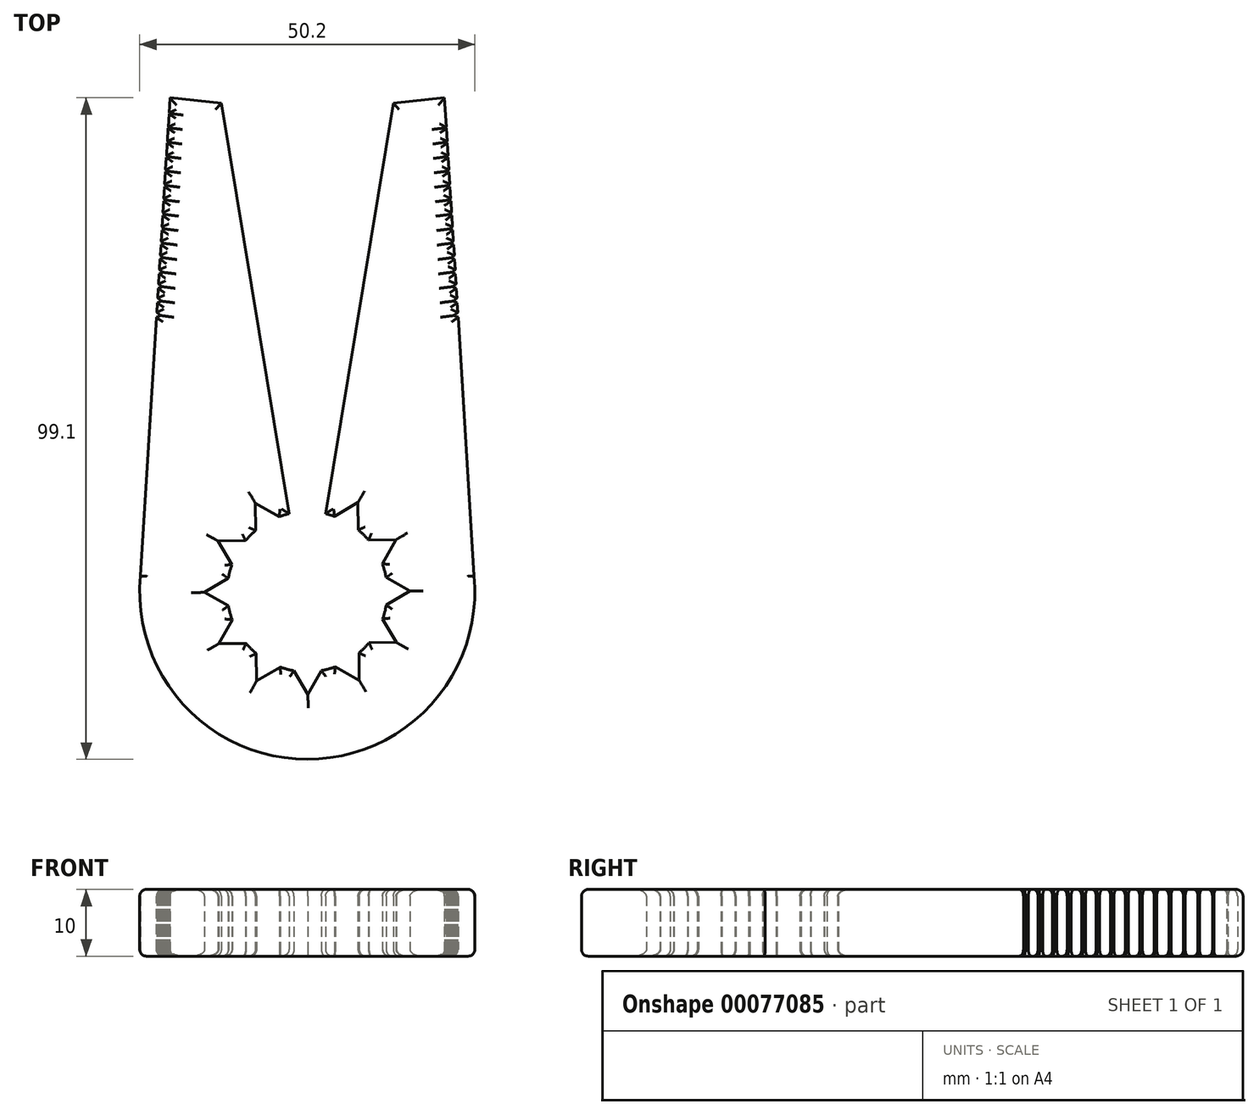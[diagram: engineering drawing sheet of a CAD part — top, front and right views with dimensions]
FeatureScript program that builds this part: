
annotation { "Feature Type Name" : "Feature", "Feature Type Description" : "" }
export const myFeature = defineFeature(function(context is Context, id is Id, definition is map)
    precondition{}
    {
        {
            var Q0;
            Q0=qCreatedBy(makeId("Top.planeOp"),FACE);
            var sketch = newSketch(context, id + "F0", { "sketchPlane" : qUnion([Q0])});
            skLineSegment(sketch, "E0", {"start": v(-12.9, 73.17) * mm, "end": v(-20.56, 74) * mm});
            skLineSegment(sketch, "E1", {"start": v(-20.56, 74) * mm, "end": v(-21.27, 62.5) * mm});
            skLineSegment(sketch, "E2", {"start": v(0, 72.49) * mm, "end": v(0, 12) * mm, "construction": true});
            skArc(sketch, "E3.trimOffspring", {"start": v(-25, 2.38) * mm, "mid": v(-18.57, -16.89) * mm, "end": v(0, -25.1) * mm});
            skArc(sketch, "E4.MirrorCS", {"start": v(25, 2.38) * mm, "mid": v(18.57, -16.89) * mm, "end": v(0, -25.1) * mm});
            skLineSegment(sketch, "E5.MirrorCS", {"start": v(20.56, 74) * mm, "end": v(21.27, 62.5) * mm});
            skLineSegment(sketch, "E6.MirrorCS", {"start": v(12.9, 73.17) * mm, "end": v(20.56, 74) * mm});
            skLineSegment(sketch, "E7.MirrorCS", {"start": v(2.74, 11.68) * mm, "end": v(12.9, 73.17) * mm});
            skLineSegment(sketch, "E8.trimOffspring", {"start": v(-22.3, 45.9) * mm, "end": v(-25, 2.38) * mm});
            skLineSegment(sketch, "E9.trimOffspring", {"start": v(22.3, 45.9) * mm, "end": v(25, 2.38) * mm});
            skLineSegment(sketch, "E10", {"start": v(-2.74, 11.68) * mm, "end": v(-12.9, 73.17) * mm});
            skPoint(sketch, "E11.orphan", {"position": v(3.63, 13.56) * mm});
            skLineSegment(sketch, "E12.trimOffspring", {"start": v(0, 10.98) * mm, "end": v(0, -73.22) * mm, "construction": true});
            skArc(sketch, "E13", {"start": v(-7.74, 9.17) * mm, "mid": v(-8.53, 8.44) * mm, "end": v(-9.25, 7.64) * mm});
            skLineSegment(sketch, "E14.0", {"start": v(-15.38, -0.1) * mm, "end": v(-11.83, 2) * mm});
            skLineSegment(sketch, "E14.2", {"start": v(-11.81, -2.12) * mm, "end": v(-15.38, -0.1) * mm});
            skPoint(sketch, "E14.0.midPoint", {"position": v(-10.66, 2.69) * mm});
            skPoint(sketch, "E14.1.start.orphan", {"position": v(-5.94, 5.48) * mm});
            skPoint(sketch, "E15.1.0", {"position": v(-10.58, -3) * mm});
            skLineSegment(sketch, "E15.1.1", {"start": v(-13.27, -7.78) * mm, "end": v(-11.25, -4.19) * mm});
            skLineSegment(sketch, "E15.1.2", {"start": v(-9.17, -7.74) * mm, "end": v(-13.27, -7.78) * mm});
            skPoint(sketch, "E15.2.0", {"position": v(-7.66, -7.89) * mm});
            skLineSegment(sketch, "E15.2.1", {"start": v(-7.6, -13.37) * mm, "end": v(-7.64, -9.25) * mm});
            skLineSegment(sketch, "E15.2.2", {"start": v(-4.07, -11.29) * mm, "end": v(-7.6, -13.37) * mm});
            skPoint(sketch, "E15.3.0", {"position": v(-2.69, -10.66) * mm});
            skLineSegment(sketch, "E15.3.1", {"start": v(0.1, -15.38) * mm, "end": v(-2, -11.83) * mm});
            skLineSegment(sketch, "E15.3.2", {"start": v(2.12, -11.81) * mm, "end": v(0.1, -15.38) * mm});
            skPoint(sketch, "E15.4.0", {"position": v(3, -10.58) * mm});
            skLineSegment(sketch, "E15.4.1", {"start": v(7.78, -13.27) * mm, "end": v(4.19, -11.25) * mm});
            skLineSegment(sketch, "E15.4.2", {"start": v(7.74, -9.17) * mm, "end": v(7.78, -13.27) * mm});
            skPoint(sketch, "E15.5.0", {"position": v(7.89, -7.66) * mm});
            skLineSegment(sketch, "E15.5.1", {"start": v(13.37, -7.6) * mm, "end": v(9.25, -7.64) * mm});
            skLineSegment(sketch, "E15.5.2", {"start": v(11.29, -4.07) * mm, "end": v(13.37, -7.6) * mm});
            skPoint(sketch, "E15.6.0", {"position": v(10.66, -2.69) * mm});
            skLineSegment(sketch, "E15.6.1", {"start": v(15.38, 0.1) * mm, "end": v(11.83, -2) * mm});
            skLineSegment(sketch, "E15.6.2", {"start": v(11.81, 2.12) * mm, "end": v(15.38, 0.1) * mm});
            skPoint(sketch, "E15.7.0", {"position": v(10.58, 3) * mm});
            skLineSegment(sketch, "E15.7.1", {"start": v(13.27, 7.78) * mm, "end": v(11.25, 4.19) * mm});
            skLineSegment(sketch, "E15.7.2", {"start": v(9.17, 7.74) * mm, "end": v(13.27, 7.78) * mm});
            skPoint(sketch, "E15.8.0", {"position": v(7.66, 7.89) * mm});
            skLineSegment(sketch, "E15.8.1", {"start": v(7.6, 13.37) * mm, "end": v(7.64, 9.25) * mm});
            skLineSegment(sketch, "E15.8.2", {"start": v(4.07, 11.29) * mm, "end": v(7.6, 13.37) * mm});
            skPoint(sketch, "E15.9.0", {"position": v(2.69, 10.66) * mm});
            skLineSegment(sketch, "E15.9.1", {"start": v(-0.1, 15.38) * mm, "end": v(0, 15.2) * mm});
            skPoint(sketch, "E15.10.0", {"position": v(-3, 10.58) * mm});
            skLineSegment(sketch, "E15.10.1", {"start": v(-7.78, 13.27) * mm, "end": v(-4.19, 11.25) * mm});
            skLineSegment(sketch, "E15.10.2", {"start": v(-7.74, 9.17) * mm, "end": v(-7.78, 13.27) * mm});
            skPoint(sketch, "E15.11.0", {"position": v(-7.89, 7.66) * mm});
            skLineSegment(sketch, "E15.11.1", {"start": v(-13.37, 7.6) * mm, "end": v(-9.25, 7.64) * mm});
            skLineSegment(sketch, "E15.11.2", {"start": v(-11.29, 4.07) * mm, "end": v(-13.37, 7.6) * mm});
            skArc(sketch, "E16.trimOffspring", {"start": v(-11.29, 4.07) * mm, "mid": v(-11.6, 3.05) * mm, "end": v(-11.83, 2) * mm});
            skArc(sketch, "E17.trimOffspring", {"start": v(-11.81, -2.12) * mm, "mid": v(-11.58, -3.16) * mm, "end": v(-11.25, -4.19) * mm});
            skArc(sketch, "E18.trimOffspring", {"start": v(-9.17, -7.74) * mm, "mid": v(-8.44, -8.53) * mm, "end": v(-7.64, -9.25) * mm});
            skArc(sketch, "E19.trimOffspring", {"start": v(-4.07, -11.29) * mm, "mid": v(-3.05, -11.6) * mm, "end": v(-2, -11.83) * mm});
            skArc(sketch, "E20.trimOffspring", {"start": v(2.12, -11.81) * mm, "mid": v(3.16, -11.58) * mm, "end": v(4.19, -11.25) * mm});
            skArc(sketch, "E21.trimOffspring", {"start": v(7.74, -9.17) * mm, "mid": v(8.53, -8.44) * mm, "end": v(9.25, -7.64) * mm});
            skArc(sketch, "E22.trimOffspring", {"start": v(11.29, -4.07) * mm, "mid": v(11.6, -3.05) * mm, "end": v(11.83, -2) * mm});
            skArc(sketch, "E23.trimOffspring", {"start": v(11.81, 2.12) * mm, "mid": v(11.58, 3.16) * mm, "end": v(11.25, 4.19) * mm});
            skArc(sketch, "E24.trimOffspring", {"start": v(9.17, 7.74) * mm, "mid": v(8.44, 8.53) * mm, "end": v(7.64, 9.25) * mm});
            skArc(sketch, "E25.trimOffspring", {"start": v(4.07, 11.29) * mm, "mid": v(3.41, 11.5) * mm, "end": v(2.74, 11.68) * mm});
            skArc(sketch, "E26.trimOffspring", {"start": v(-2.74, 11.68) * mm, "mid": v(-3.47, 11.49) * mm, "end": v(-4.19, 11.25) * mm});
            skPoint(sketch, "E27.orphan", {"position": v(2, 11.83) * mm});
            skLineSegment(sketch, "E28", {"start": v(-21.27, 62.5) * mm, "end": v(-22.3, 45.9) * mm});
            skLineSegment(sketch, "E29", {"start": v(21.27, 62.5) * mm, "end": v(22.3, 45.9) * mm});
            skSolve(sketch);
        }
        {
            var Q0;
            Q0=makeQuery(id+"F0.imprint","IMPRINT",FACE,{"disambiguationData":[TD([[makeQuery(id+"F0.imprint","IMPRINT",EDGE,{"derivedFrom":sQuery(id+"F0.wireOp",EDGE,"E0")}),1.0]])]});
            extrude(context, id + "F1", {"entities" : qUnion([Q0]), "depth" : 10 * mm});
        }
        {
            var Q0;
            Q0=qCreatedBy(makeId("Top.planeOp"),FACE);
            var sketch = newSketch(context, id + "F2", { "sketchPlane" : qUnion([Q0])});
            skCircle(sketch, "E30.cCircle", {"center": v(-30.95, 42.52) * mm, "radius": 4.54 * mm, "construction": true});
            skLineSegment(sketch, "E30.0", {"start": v(-21.95, 41.38) * mm, "end": v(-36.45, 35.3) * mm});
            skLineSegment(sketch, "E30.1", {"start": v(-36.45, 35.3) * mm, "end": v(-34.46, 50.9) * mm});
            skLineSegment(sketch, "E30.2", {"start": v(-34.46, 50.9) * mm, "end": v(-21.95, 41.38) * mm});
            skPoint(sketch, "E30.0.midPoint", {"position": v(-29.2, 38.34) * mm});
            skLineSegment(sketch, "E31.1.0.0", {"start": v(-21.85, 43.54) * mm, "end": v(-36.35, 37.46) * mm});
            skCircle(sketch, "E31.1.0.1", {"center": v(-30.86, 44.69) * mm, "radius": 4.54 * mm, "construction": true});
            skPoint(sketch, "E31.1.0.2", {"position": v(-29.1, 40.5) * mm});
            skLineSegment(sketch, "E31.1.0.3", {"start": v(-34.37, 53.06) * mm, "end": v(-21.85, 43.54) * mm});
            skLineSegment(sketch, "E31.1.0.4", {"start": v(-36.35, 37.46) * mm, "end": v(-34.37, 53.06) * mm});
            skLineSegment(sketch, "E31.2.0.0", {"start": v(-21.75, 45.7) * mm, "end": v(-36.25, 39.62) * mm});
            skCircle(sketch, "E31.2.0.1", {"center": v(-30.76, 46.85) * mm, "radius": 4.54 * mm, "construction": true});
            skPoint(sketch, "E31.2.0.2", {"position": v(-29, 42.66) * mm});
            skLineSegment(sketch, "E31.2.0.3", {"start": v(-34.27, 55.22) * mm, "end": v(-21.75, 45.7) * mm});
            skLineSegment(sketch, "E31.2.0.4", {"start": v(-36.25, 39.62) * mm, "end": v(-34.27, 55.22) * mm});
            skLineSegment(sketch, "E31.3.0.0", {"start": v(-21.65, 47.87) * mm, "end": v(-36.16, 41.79) * mm});
            skCircle(sketch, "E31.3.0.1", {"center": v(-30.66, 49.01) * mm, "radius": 4.54 * mm, "construction": true});
            skPoint(sketch, "E31.3.0.2", {"position": v(-28.9, 44.83) * mm});
            skLineSegment(sketch, "E31.3.0.3", {"start": v(-34.17, 57.39) * mm, "end": v(-21.65, 47.87) * mm});
            skLineSegment(sketch, "E31.3.0.4", {"start": v(-36.16, 41.79) * mm, "end": v(-34.17, 57.39) * mm});
            skLineSegment(sketch, "E31.4.0.0", {"start": v(-21.55, 50.03) * mm, "end": v(-36.06, 43.95) * mm});
            skCircle(sketch, "E31.4.0.1", {"center": v(-30.56, 51.18) * mm, "radius": 4.54 * mm, "construction": true});
            skPoint(sketch, "E31.4.0.2", {"position": v(-28.8, 46.99) * mm});
            skLineSegment(sketch, "E31.4.0.3", {"start": v(-34.07, 59.55) * mm, "end": v(-21.55, 50.03) * mm});
            skLineSegment(sketch, "E31.4.0.4", {"start": v(-36.06, 43.95) * mm, "end": v(-34.07, 59.55) * mm});
            skLineSegment(sketch, "E31.5.0.0", {"start": v(-21.46, 52.2) * mm, "end": v(-35.96, 46.11) * mm});
            skCircle(sketch, "E31.5.0.1", {"center": v(-30.46, 53.34) * mm, "radius": 4.54 * mm, "construction": true});
            skPoint(sketch, "E31.5.0.2", {"position": v(-28.7, 49.15) * mm});
            skLineSegment(sketch, "E31.5.0.3", {"start": v(-33.98, 61.71) * mm, "end": v(-21.46, 52.2) * mm});
            skLineSegment(sketch, "E31.5.0.4", {"start": v(-35.96, 46.11) * mm, "end": v(-33.98, 61.71) * mm});
            skLineSegment(sketch, "E31.6.0.0", {"start": v(-21.36, 54.36) * mm, "end": v(-35.86, 48.27) * mm});
            skCircle(sketch, "E31.6.0.1", {"center": v(-30.37, 55.5) * mm, "radius": 4.54 * mm, "construction": true});
            skPoint(sketch, "E31.6.0.2", {"position": v(-28.61, 51.32) * mm});
            skLineSegment(sketch, "E31.6.0.3", {"start": v(-33.88, 63.88) * mm, "end": v(-21.36, 54.36) * mm});
            skLineSegment(sketch, "E31.6.0.4", {"start": v(-35.86, 48.27) * mm, "end": v(-33.88, 63.88) * mm});
            skLineSegment(sketch, "E31.7.0.0", {"start": v(-21.26, 56.52) * mm, "end": v(-35.76, 50.44) * mm});
            skCircle(sketch, "E31.7.0.1", {"center": v(-30.27, 57.67) * mm, "radius": 4.54 * mm, "construction": true});
            skPoint(sketch, "E31.7.0.2", {"position": v(-28.51, 53.48) * mm});
            skLineSegment(sketch, "E31.7.0.3", {"start": v(-33.78, 66.04) * mm, "end": v(-21.26, 56.52) * mm});
            skLineSegment(sketch, "E31.7.0.4", {"start": v(-35.76, 50.44) * mm, "end": v(-33.78, 66.04) * mm});
            skLineSegment(sketch, "E31.8.0.0", {"start": v(-21.16, 58.68) * mm, "end": v(-35.67, 52.6) * mm});
            skCircle(sketch, "E31.8.0.1", {"center": v(-30.17, 59.83) * mm, "radius": 4.54 * mm, "construction": true});
            skPoint(sketch, "E31.8.0.2", {"position": v(-28.41, 55.64) * mm});
            skLineSegment(sketch, "E31.8.0.3", {"start": v(-33.68, 68.2) * mm, "end": v(-21.16, 58.68) * mm});
            skLineSegment(sketch, "E31.8.0.4", {"start": v(-35.67, 52.6) * mm, "end": v(-33.68, 68.2) * mm});
            skLineSegment(sketch, "E31.9.0.0", {"start": v(-21.07, 60.85) * mm, "end": v(-35.57, 54.76) * mm});
            skCircle(sketch, "E31.9.0.1", {"center": v(-30.07, 62) * mm, "radius": 4.54 * mm, "construction": true});
            skPoint(sketch, "E31.9.0.2", {"position": v(-28.32, 57.8) * mm});
            skLineSegment(sketch, "E31.9.0.3", {"start": v(-33.58, 70.37) * mm, "end": v(-21.07, 60.85) * mm});
            skLineSegment(sketch, "E31.9.0.4", {"start": v(-35.57, 54.76) * mm, "end": v(-33.58, 70.37) * mm});
            skLineSegment(sketch, "E31.10.0.0", {"start": v(-20.97, 63.01) * mm, "end": v(-35.47, 56.93) * mm});
            skCircle(sketch, "E31.10.0.1", {"center": v(-29.98, 64.16) * mm, "radius": 4.54 * mm, "construction": true});
            skPoint(sketch, "E31.10.0.2", {"position": v(-28.22, 59.97) * mm});
            skLineSegment(sketch, "E31.10.0.3", {"start": v(-33.49, 72.53) * mm, "end": v(-20.97, 63.01) * mm});
            skLineSegment(sketch, "E31.10.0.4", {"start": v(-35.47, 56.93) * mm, "end": v(-33.49, 72.53) * mm});
            skLineSegment(sketch, "E31.11.0.0", {"start": v(-20.87, 65.17) * mm, "end": v(-35.37, 59.1) * mm});
            skCircle(sketch, "E31.11.0.1", {"center": v(-29.88, 66.32) * mm, "radius": 4.54 * mm, "construction": true});
            skPoint(sketch, "E31.11.0.2", {"position": v(-28.12, 62.13) * mm});
            skLineSegment(sketch, "E31.11.0.3", {"start": v(-33.39, 74.7) * mm, "end": v(-20.87, 65.17) * mm});
            skLineSegment(sketch, "E31.11.0.4", {"start": v(-35.37, 59.1) * mm, "end": v(-33.39, 74.7) * mm});
            skLineSegment(sketch, "E31.12.0.0", {"start": v(-20.77, 67.34) * mm, "end": v(-35.28, 61.25) * mm});
            skCircle(sketch, "E31.12.0.1", {"center": v(-29.78, 68.48) * mm, "radius": 4.54 * mm, "construction": true});
            skPoint(sketch, "E31.12.0.2", {"position": v(-28.02, 64.3) * mm});
            skLineSegment(sketch, "E31.12.0.3", {"start": v(-33.3, 76.86) * mm, "end": v(-20.77, 67.34) * mm});
            skLineSegment(sketch, "E31.12.0.4", {"start": v(-35.28, 61.25) * mm, "end": v(-33.3, 76.86) * mm});
            skLineSegment(sketch, "E31.13.0.0", {"start": v(-20.67, 69.5) * mm, "end": v(-35.18, 63.42) * mm});
            skCircle(sketch, "E31.13.0.1", {"center": v(-29.68, 70.65) * mm, "radius": 4.54 * mm, "construction": true});
            skPoint(sketch, "E31.13.0.2", {"position": v(-27.93, 66.46) * mm});
            skLineSegment(sketch, "E31.13.0.3", {"start": v(-33.2, 79.02) * mm, "end": v(-20.67, 69.5) * mm});
            skLineSegment(sketch, "E31.13.0.4", {"start": v(-35.18, 63.42) * mm, "end": v(-33.2, 79.02) * mm});
            skLineSegment(sketch, "E31.14.0.0", {"start": v(-20.58, 71.66) * mm, "end": v(-35.08, 65.58) * mm});
            skCircle(sketch, "E31.14.0.1", {"center": v(-29.58, 72.8) * mm, "radius": 4.54 * mm, "construction": true});
            skPoint(sketch, "E31.14.0.2", {"position": v(-27.83, 68.62) * mm});
            skLineSegment(sketch, "E31.14.0.3", {"start": v(-33.1, 81.18) * mm, "end": v(-20.58, 71.66) * mm});
            skLineSegment(sketch, "E31.14.0.4", {"start": v(-35.08, 65.58) * mm, "end": v(-33.1, 81.18) * mm});
            skLineSegment(sketch, "E31.direction1", {"start": v(-36.45, 35.3) * mm, "end": v(-36.35, 37.46) * mm, "construction": true});
            skLineSegment(sketch, "E32.MirrorCS", {"start": v(36.45, 35.3) * mm, "end": v(36.35, 37.46) * mm, "construction": true});
            skLineSegment(sketch, "E33.MirrorCS", {"start": v(36.25, 39.62) * mm, "end": v(34.27, 55.22) * mm});
            skLineSegment(sketch, "E34.MirrorCS", {"start": v(36.35, 37.46) * mm, "end": v(34.37, 53.06) * mm});
            skLineSegment(sketch, "E35.MirrorCS", {"start": v(36.16, 41.79) * mm, "end": v(34.17, 57.39) * mm});
            skLineSegment(sketch, "E36.MirrorCS", {"start": v(35.96, 46.11) * mm, "end": v(33.98, 61.71) * mm});
            skLineSegment(sketch, "E37.MirrorCS", {"start": v(35.57, 54.76) * mm, "end": v(33.58, 70.37) * mm});
            skLineSegment(sketch, "E38.MirrorCS", {"start": v(35.18, 63.42) * mm, "end": v(33.2, 79.02) * mm});
            skLineSegment(sketch, "E39.MirrorCS", {"start": v(35.28, 61.25) * mm, "end": v(33.3, 76.86) * mm});
            skLineSegment(sketch, "E40.MirrorCS", {"start": v(36.06, 43.95) * mm, "end": v(34.07, 59.55) * mm});
            skLineSegment(sketch, "E41.MirrorCS", {"start": v(35.67, 52.6) * mm, "end": v(33.68, 68.2) * mm});
            skLineSegment(sketch, "E42.MirrorCS", {"start": v(35.37, 59.1) * mm, "end": v(33.39, 74.7) * mm});
            skLineSegment(sketch, "E43.MirrorCS", {"start": v(35.76, 50.44) * mm, "end": v(33.78, 66.04) * mm});
            skLineSegment(sketch, "E44.MirrorCS", {"start": v(35.47, 56.93) * mm, "end": v(33.49, 72.53) * mm});
            skLineSegment(sketch, "E45.MirrorCS", {"start": v(35.86, 48.27) * mm, "end": v(33.88, 63.88) * mm});
            skLineSegment(sketch, "E46.MirrorCS", {"start": v(36.45, 35.3) * mm, "end": v(34.46, 50.9) * mm});
            skPoint(sketch, "E47.MirrorP", {"position": v(28.32, 57.8) * mm});
            skPoint(sketch, "E48.MirrorP", {"position": v(29.2, 38.34) * mm});
            skPoint(sketch, "E49.MirrorP", {"position": v(28.41, 55.64) * mm});
            skLineSegment(sketch, "E50.MirrorCS", {"start": v(33.88, 63.88) * mm, "end": v(21.36, 54.36) * mm});
            skLineSegment(sketch, "E51.MirrorCS", {"start": v(33.49, 72.53) * mm, "end": v(20.97, 63.01) * mm});
            skPoint(sketch, "E52.MirrorP", {"position": v(28.61, 51.32) * mm});
            skPoint(sketch, "E53.MirrorP", {"position": v(27.83, 68.62) * mm});
            skLineSegment(sketch, "E54.MirrorCS", {"start": v(21.65, 47.87) * mm, "end": v(36.16, 41.79) * mm});
            skCircle(sketch, "E55.MirrorC", {"center": v(30.37, 55.5) * mm, "radius": 4.54 * mm, "construction": true});
            skCircle(sketch, "E56.MirrorC", {"center": v(29.98, 64.16) * mm, "radius": 4.54 * mm, "construction": true});
            skCircle(sketch, "E57.MirrorC", {"center": v(29.58, 72.8) * mm, "radius": 4.54 * mm, "construction": true});
            skLineSegment(sketch, "E58.MirrorCS", {"start": v(34.27, 55.22) * mm, "end": v(21.75, 45.7) * mm});
            skCircle(sketch, "E59.MirrorC", {"center": v(30.76, 46.85) * mm, "radius": 4.54 * mm, "construction": true});
            skLineSegment(sketch, "E60.MirrorCS", {"start": v(21.75, 45.7) * mm, "end": v(36.25, 39.62) * mm});
            skLineSegment(sketch, "E61.MirrorCS", {"start": v(34.37, 53.06) * mm, "end": v(21.85, 43.54) * mm});
            skCircle(sketch, "E62.MirrorC", {"center": v(30.86, 44.69) * mm, "radius": 4.54 * mm, "construction": true});
            skLineSegment(sketch, "E63.MirrorCS", {"start": v(21.85, 43.54) * mm, "end": v(36.35, 37.46) * mm});
            skLineSegment(sketch, "E64.MirrorCS", {"start": v(34.46, 50.9) * mm, "end": v(21.95, 41.38) * mm});
            skLineSegment(sketch, "E65.MirrorCS", {"start": v(21.95, 41.38) * mm, "end": v(36.45, 35.3) * mm});
            skCircle(sketch, "E66.MirrorC", {"center": v(30.95, 42.52) * mm, "radius": 4.54 * mm, "construction": true});
            skLineSegment(sketch, "E67.MirrorCS", {"start": v(34.17, 57.39) * mm, "end": v(21.65, 47.87) * mm});
            skCircle(sketch, "E68.MirrorC", {"center": v(30.66, 49.01) * mm, "radius": 4.54 * mm, "construction": true});
            skLineSegment(sketch, "E69.MirrorCS", {"start": v(21.36, 54.36) * mm, "end": v(35.86, 48.27) * mm});
            skLineSegment(sketch, "E70.MirrorCS", {"start": v(20.97, 63.01) * mm, "end": v(35.47, 56.93) * mm});
            skPoint(sketch, "E71.MirrorP", {"position": v(28.7, 49.15) * mm});
            skPoint(sketch, "E72.MirrorP", {"position": v(27.93, 66.46) * mm});
            skLineSegment(sketch, "E73.MirrorCS", {"start": v(33.2, 79.02) * mm, "end": v(20.67, 69.5) * mm});
            skLineSegment(sketch, "E74.MirrorCS", {"start": v(33.98, 61.71) * mm, "end": v(21.46, 52.2) * mm});
            skLineSegment(sketch, "E75.MirrorCS", {"start": v(33.58, 70.37) * mm, "end": v(21.07, 60.85) * mm});
            skCircle(sketch, "E76.MirrorC", {"center": v(29.68, 70.65) * mm, "radius": 4.54 * mm, "construction": true});
            skCircle(sketch, "E77.MirrorC", {"center": v(30.46, 53.34) * mm, "radius": 4.54 * mm, "construction": true});
            skCircle(sketch, "E78.MirrorC", {"center": v(30.07, 62) * mm, "radius": 4.54 * mm, "construction": true});
            skPoint(sketch, "E79.MirrorP", {"position": v(28.8, 46.99) * mm});
            skPoint(sketch, "E80.MirrorP", {"position": v(28.02, 64.3) * mm});
            skLineSegment(sketch, "E81.MirrorCS", {"start": v(20.67, 69.5) * mm, "end": v(35.18, 63.42) * mm});
            skLineSegment(sketch, "E82.MirrorCS", {"start": v(21.46, 52.2) * mm, "end": v(35.96, 46.11) * mm});
            skLineSegment(sketch, "E83.MirrorCS", {"start": v(21.07, 60.85) * mm, "end": v(35.57, 54.76) * mm});
            skPoint(sketch, "E84.MirrorP", {"position": v(28.9, 44.83) * mm});
            skPoint(sketch, "E85.MirrorP", {"position": v(28.12, 62.13) * mm});
            skLineSegment(sketch, "E86.MirrorCS", {"start": v(33.3, 76.86) * mm, "end": v(20.77, 67.34) * mm});
            skLineSegment(sketch, "E87.MirrorCS", {"start": v(34.07, 59.55) * mm, "end": v(21.55, 50.03) * mm});
            skLineSegment(sketch, "E88.MirrorCS", {"start": v(33.68, 68.2) * mm, "end": v(21.16, 58.68) * mm});
            skCircle(sketch, "E89.MirrorC", {"center": v(29.78, 68.48) * mm, "radius": 4.54 * mm, "construction": true});
            skCircle(sketch, "E90.MirrorC", {"center": v(30.56, 51.18) * mm, "radius": 4.54 * mm, "construction": true});
            skCircle(sketch, "E91.MirrorC", {"center": v(30.17, 59.83) * mm, "radius": 4.54 * mm, "construction": true});
            skPoint(sketch, "E92.MirrorP", {"position": v(29, 42.66) * mm});
            skPoint(sketch, "E93.MirrorP", {"position": v(28.22, 59.97) * mm});
            skLineSegment(sketch, "E94.MirrorCS", {"start": v(21.55, 50.03) * mm, "end": v(36.06, 43.95) * mm});
            skLineSegment(sketch, "E95.MirrorCS", {"start": v(21.16, 58.68) * mm, "end": v(35.67, 52.6) * mm});
            skLineSegment(sketch, "E96.MirrorCS", {"start": v(20.77, 67.34) * mm, "end": v(35.28, 61.25) * mm});
            skPoint(sketch, "E97.MirrorP", {"position": v(29.1, 40.5) * mm});
            skLineSegment(sketch, "E98.MirrorCS", {"start": v(33.39, 74.7) * mm, "end": v(20.87, 65.17) * mm});
            skLineSegment(sketch, "E99.MirrorCS", {"start": v(33.78, 66.04) * mm, "end": v(21.26, 56.52) * mm});
            skLineSegment(sketch, "E100.MirrorCS", {"start": v(21.26, 56.52) * mm, "end": v(35.76, 50.44) * mm});
            skLineSegment(sketch, "E101.MirrorCS", {"start": v(20.87, 65.17) * mm, "end": v(35.37, 59.1) * mm});
            skPoint(sketch, "E102.MirrorP", {"position": v(28.51, 53.48) * mm});
            skCircle(sketch, "E103.MirrorC", {"center": v(29.88, 66.32) * mm, "radius": 4.54 * mm, "construction": true});
            skLineSegment(sketch, "E104.MirrorCS", {"start": v(35.08, 65.58) * mm, "end": v(33.1, 81.18) * mm});
            skCircle(sketch, "E105.MirrorC", {"center": v(30.27, 57.67) * mm, "radius": 4.54 * mm, "construction": true});
            skSolve(sketch);
        }
        {
            var Q0;
            {var subQ0=sQuery(id+"F2.wireOp",EDGE,"E31.14.0.0");var subQ1=sQuery(id+"F2.wireOp",EDGE,"E31.11.0.3");var subQ2=makeQuery(id+"F2.imprint","INTERSECT",VERTEX,{"derivedFrom":[subQ1,subQ0]});Q0=makeQuery(id+"F2.imprint","IMPRINT",FACE,{"disambiguationData":[TD([[makeQuery(id+"F2.imprint","IMPRINT",EDGE,{"disambiguationData":[TD([[subQ2,-1.0]])],"derivedFrom":subQ1}),1.0]])]});}
            var Q1;
            {var subQ0=sQuery(id+"F2.wireOp",EDGE,"E31.9.0.0");var subQ1=sQuery(id+"F2.wireOp",EDGE,"E31.6.0.3");var subQ2=makeQuery(id+"F2.imprint","INTERSECT",VERTEX,{"derivedFrom":[subQ1,subQ0]});Q1=makeQuery(id+"F2.imprint","IMPRINT",FACE,{"disambiguationData":[TD([[makeQuery(id+"F2.imprint","IMPRINT",EDGE,{"disambiguationData":[TD([[subQ2,-1.0]])],"derivedFrom":subQ1}),1.0]])]});}
            var Q2;
            {var subQ0=sQuery(id+"F2.wireOp",EDGE,"E31.5.0.0");var subQ1=sQuery(id+"F2.wireOp",EDGE,"E31.2.0.3");var subQ2=makeQuery(id+"F2.imprint","INTERSECT",VERTEX,{"derivedFrom":[subQ1,subQ0]});Q2=makeQuery(id+"F2.imprint","IMPRINT",FACE,{"disambiguationData":[TD([[makeQuery(id+"F2.imprint","IMPRINT",EDGE,{"disambiguationData":[TD([[subQ2,-1.0]])],"derivedFrom":subQ1}),1.0]])]});}
            var Q3;
            {var subQ0=sQuery(id+"F2.wireOp",EDGE,"E31.7.0.0");var subQ1=sQuery(id+"F2.wireOp",EDGE,"E31.4.0.3");var subQ2=makeQuery(id+"F2.imprint","INTERSECT",VERTEX,{"derivedFrom":[subQ1,subQ0]});Q3=makeQuery(id+"F2.imprint","IMPRINT",FACE,{"disambiguationData":[TD([[makeQuery(id+"F2.imprint","IMPRINT",EDGE,{"disambiguationData":[TD([[subQ2,-1.0]])],"derivedFrom":subQ1}),1.0]])]});}
            var Q4;
            {var subQ0=sQuery(id+"F2.wireOp",EDGE,"E31.5.0.0");var subQ1=sQuery(id+"F2.wireOp",EDGE,"E31.4.0.3");var subQ2=makeQuery(id+"F2.imprint","INTERSECT",VERTEX,{"derivedFrom":[subQ1,subQ0]});Q4=makeQuery(id+"F2.imprint","IMPRINT",FACE,{"disambiguationData":[TD([[makeQuery(id+"F2.imprint","IMPRINT",EDGE,{"disambiguationData":[TD([[subQ2,1.0]])],"derivedFrom":subQ1}),1.0]])]});}
            var Q5;
            {var subQ0=sQuery(id+"F2.wireOp",EDGE,"E31.11.0.0");var subQ1=sQuery(id+"F2.wireOp",EDGE,"E31.8.0.3");var subQ2=makeQuery(id+"F2.imprint","INTERSECT",VERTEX,{"derivedFrom":[subQ1,subQ0]});Q5=makeQuery(id+"F2.imprint","IMPRINT",FACE,{"disambiguationData":[TD([[makeQuery(id+"F2.imprint","IMPRINT",EDGE,{"disambiguationData":[TD([[subQ2,-1.0]])],"derivedFrom":subQ1}),1.0]])]});}
            var Q6;
            {var subQ0=sQuery(id+"F2.wireOp",EDGE,"E31.12.0.0");var subQ1=sQuery(id+"F2.wireOp",EDGE,"E31.11.0.3");var subQ2=makeQuery(id+"F2.imprint","INTERSECT",VERTEX,{"derivedFrom":[subQ1,subQ0]});Q6=makeQuery(id+"F2.imprint","IMPRINT",FACE,{"disambiguationData":[TD([[makeQuery(id+"F2.imprint","IMPRINT",EDGE,{"disambiguationData":[TD([[subQ2,1.0]])],"derivedFrom":subQ1}),1.0]])]});}
            var Q7;
            {var subQ0=sQuery(id+"F2.wireOp",EDGE,"E31.12.0.4");var subQ1=sQuery(id+"F2.wireOp",EDGE,"E31.12.0.3");var subQ2=makeQuery(id+"F2.imprint","INTERSECT",VERTEX,{"derivedFrom":[subQ1,subQ0]});Q7=makeQuery(id+"F2.imprint","IMPRINT",FACE,{"disambiguationData":[TD([[makeQuery(id+"F2.imprint","IMPRINT",EDGE,{"disambiguationData":[TD([[subQ2,-1.0]])],"derivedFrom":subQ1}),1.0]])]});}
            var Q8;
            {var subQ0=sQuery(id+"F2.wireOp",EDGE,"E31.13.0.0");var subQ1=sQuery(id+"F2.wireOp",EDGE,"E31.12.0.3");var subQ2=makeQuery(id+"F2.imprint","INTERSECT",VERTEX,{"derivedFrom":[subQ1,subQ0]});Q8=makeQuery(id+"F2.imprint","IMPRINT",FACE,{"disambiguationData":[TD([[makeQuery(id+"F2.imprint","IMPRINT",EDGE,{"disambiguationData":[TD([[subQ2,1.0]])],"derivedFrom":subQ1}),1.0]])]});}
            var Q9;
            {var subQ0=sQuery(id+"F2.wireOp",EDGE,"E31.8.0.0");var subQ1=sQuery(id+"F2.wireOp",EDGE,"E31.5.0.3");var subQ2=makeQuery(id+"F2.imprint","INTERSECT",VERTEX,{"derivedFrom":[subQ1,subQ0]});Q9=makeQuery(id+"F2.imprint","IMPRINT",FACE,{"disambiguationData":[TD([[makeQuery(id+"F2.imprint","IMPRINT",EDGE,{"disambiguationData":[TD([[subQ2,-1.0]])],"derivedFrom":subQ1}),1.0]])]});}
            var Q10;
            {var subQ0=sQuery(id+"F2.wireOp",EDGE,"E31.6.0.0");var subQ1=sQuery(id+"F2.wireOp",EDGE,"E31.3.0.3");var subQ2=makeQuery(id+"F2.imprint","INTERSECT",VERTEX,{"derivedFrom":[subQ1,subQ0]});Q10=makeQuery(id+"F2.imprint","IMPRINT",FACE,{"disambiguationData":[TD([[makeQuery(id+"F2.imprint","IMPRINT",EDGE,{"disambiguationData":[TD([[subQ2,-1.0]])],"derivedFrom":subQ1}),1.0]])]});}
            var Q11;
            {var subQ0=sQuery(id+"F2.wireOp",EDGE,"E31.12.0.0");var subQ1=sQuery(id+"F2.wireOp",EDGE,"E31.9.0.3");var subQ2=makeQuery(id+"F2.imprint","INTERSECT",VERTEX,{"derivedFrom":[subQ1,subQ0]});Q11=makeQuery(id+"F2.imprint","IMPRINT",FACE,{"disambiguationData":[TD([[makeQuery(id+"F2.imprint","IMPRINT",EDGE,{"disambiguationData":[TD([[subQ2,-1.0]])],"derivedFrom":subQ1}),1.0]])]});}
            var Q12;
            {var subQ0=sQuery(id+"F2.wireOp",EDGE,"E30.0");Q12=makeQuery(id+"F2.imprint","IMPRINT",FACE,{"disambiguationData":[TD([[makeQuery(id+"F2.imprint","IMPRINT",EDGE,{"derivedFrom":subQ0}),-1.0]])]});}
            var Q13;
            {var subQ0=sQuery(id+"F2.wireOp",EDGE,"E31.14.0.3");Q13=makeQuery(id+"F2.imprint","IMPRINT",FACE,{"disambiguationData":[TD([[makeQuery(id+"F2.imprint","IMPRINT",EDGE,{"derivedFrom":subQ0}),-1.0]])]});}
            var Q14;
            {var subQ0=sQuery(id+"F2.wireOp",EDGE,"E31.4.0.0");var subQ1=sQuery(id+"F2.wireOp",EDGE,"E30.2");var subQ2=makeQuery(id+"F2.imprint","INTERSECT",VERTEX,{"derivedFrom":[subQ1,subQ0]});Q14=makeQuery(id+"F2.imprint","IMPRINT",FACE,{"disambiguationData":[TD([[makeQuery(id+"F2.imprint","IMPRINT",EDGE,{"disambiguationData":[TD([[subQ2,-1.0]])],"derivedFrom":subQ1}),1.0]])]});}
            var Q15;
            {var subQ0=sQuery(id+"F2.wireOp",EDGE,"E31.12.0.0");var subQ1=sQuery(id+"F2.wireOp",EDGE,"E31.8.0.3");var subQ2=makeQuery(id+"F2.imprint","INTERSECT",VERTEX,{"derivedFrom":[subQ1,subQ0]});Q15=makeQuery(id+"F2.imprint","IMPRINT",FACE,{"disambiguationData":[TD([[makeQuery(id+"F2.imprint","IMPRINT",EDGE,{"disambiguationData":[TD([[subQ2,-1.0]])],"derivedFrom":subQ1}),1.0]])]});}
            var Q16;
            {var subQ0=sQuery(id+"F2.wireOp",EDGE,"E31.10.0.0");var subQ1=sQuery(id+"F2.wireOp",EDGE,"E31.9.0.3");var subQ2=makeQuery(id+"F2.imprint","INTERSECT",VERTEX,{"derivedFrom":[subQ1,subQ0]});Q16=makeQuery(id+"F2.imprint","IMPRINT",FACE,{"disambiguationData":[TD([[makeQuery(id+"F2.imprint","IMPRINT",EDGE,{"disambiguationData":[TD([[subQ2,1.0]])],"derivedFrom":subQ1}),1.0]])]});}
            var Q17;
            {var subQ0=sQuery(id+"F2.wireOp",EDGE,"E31.4.0.4");var subQ1=sQuery(id+"F2.wireOp",EDGE,"E31.4.0.3");var subQ2=makeQuery(id+"F2.imprint","INTERSECT",VERTEX,{"derivedFrom":[subQ1,subQ0]});Q17=makeQuery(id+"F2.imprint","IMPRINT",FACE,{"disambiguationData":[TD([[makeQuery(id+"F2.imprint","IMPRINT",EDGE,{"disambiguationData":[TD([[subQ2,-1.0]])],"derivedFrom":subQ1}),1.0]])]});}
            var Q18;
            {var subQ8=sQuery(id+"F2.wireOp",EDGE,"E31.6.0.3");var subQ10=sQuery(id+"F2.wireOp",EDGE,"E31.6.0.4");var subQ11=makeQuery(id+"F2.imprint","INTERSECT",VERTEX,{"derivedFrom":[subQ8,subQ10]});Q18=makeQuery(id+"F2.imprint","IMPRINT",FACE,{"disambiguationData":[TD([[makeQuery(id+"F2.imprint","IMPRINT",EDGE,{"disambiguationData":[TD([[subQ11,-1.0]])],"derivedFrom":subQ8}),1.0]])]});}
            var Q19;
            {var subQ6=sQuery(id+"F2.wireOp",EDGE,"E31.11.0.4");var subQ7=sQuery(id+"F2.wireOp",EDGE,"E31.11.0.3");var subQ8=makeQuery(id+"F2.imprint","INTERSECT",VERTEX,{"derivedFrom":[subQ7,subQ6]});Q19=makeQuery(id+"F2.imprint","IMPRINT",FACE,{"disambiguationData":[TD([[makeQuery(id+"F2.imprint","IMPRINT",EDGE,{"disambiguationData":[TD([[subQ8,-1.0]])],"derivedFrom":subQ7}),1.0]])]});}
            var Q20;
            {var subQ0=sQuery(id+"F2.wireOp",EDGE,"E31.11.0.0");var subQ1=sQuery(id+"F2.wireOp",EDGE,"E31.10.0.3");var subQ2=makeQuery(id+"F2.imprint","INTERSECT",VERTEX,{"derivedFrom":[subQ1,subQ0]});Q20=makeQuery(id+"F2.imprint","IMPRINT",FACE,{"disambiguationData":[TD([[makeQuery(id+"F2.imprint","IMPRINT",EDGE,{"disambiguationData":[TD([[subQ2,1.0]])],"derivedFrom":subQ1}),1.0]])]});}
            var Q21;
            {var subQ7=sQuery(id+"F2.wireOp",EDGE,"E31.5.0.4");var subQ8=sQuery(id+"F2.wireOp",EDGE,"E31.5.0.3");var subQ9=makeQuery(id+"F2.imprint","INTERSECT",VERTEX,{"derivedFrom":[subQ8,subQ7]});Q21=makeQuery(id+"F2.imprint","IMPRINT",FACE,{"disambiguationData":[TD([[makeQuery(id+"F2.imprint","IMPRINT",EDGE,{"disambiguationData":[TD([[subQ9,-1.0]])],"derivedFrom":subQ8}),1.0]])]});}
            var Q22;
            {var subQ5=sQuery(id+"F2.wireOp",EDGE,"E31.3.0.4");var subQ6=sQuery(id+"F2.wireOp",EDGE,"E31.3.0.3");var subQ7=makeQuery(id+"F2.imprint","INTERSECT",VERTEX,{"derivedFrom":[subQ6,subQ5]});Q22=makeQuery(id+"F2.imprint","IMPRINT",FACE,{"disambiguationData":[TD([[makeQuery(id+"F2.imprint","IMPRINT",EDGE,{"disambiguationData":[TD([[subQ7,-1.0]])],"derivedFrom":subQ6}),1.0]])]});}
            var Q23;
            {var subQ0=sQuery(id+"F2.wireOp",EDGE,"E31.8.0.0");var subQ1=sQuery(id+"F2.wireOp",EDGE,"E31.4.0.3");var subQ2=makeQuery(id+"F2.imprint","INTERSECT",VERTEX,{"derivedFrom":[subQ1,subQ0]});Q23=makeQuery(id+"F2.imprint","IMPRINT",FACE,{"disambiguationData":[TD([[makeQuery(id+"F2.imprint","IMPRINT",EDGE,{"disambiguationData":[TD([[subQ2,-1.0]])],"derivedFrom":subQ1}),1.0]])]});}
            var Q24;
            {var subQ0=sQuery(id+"F2.wireOp",EDGE,"E31.10.0.0");var subQ1=sQuery(id+"F2.wireOp",EDGE,"E31.6.0.3");var subQ2=makeQuery(id+"F2.imprint","INTERSECT",VERTEX,{"derivedFrom":[subQ1,subQ0]});Q24=makeQuery(id+"F2.imprint","IMPRINT",FACE,{"disambiguationData":[TD([[makeQuery(id+"F2.imprint","IMPRINT",EDGE,{"disambiguationData":[TD([[subQ2,-1.0]])],"derivedFrom":subQ1}),1.0]])]});}
            var Q25;
            {var subQ0=sQuery(id+"F2.wireOp",EDGE,"E31.13.0.0");var subQ1=sQuery(id+"F2.wireOp",EDGE,"E31.10.0.3");var subQ2=makeQuery(id+"F2.imprint","INTERSECT",VERTEX,{"derivedFrom":[subQ1,subQ0]});Q25=makeQuery(id+"F2.imprint","IMPRINT",FACE,{"disambiguationData":[TD([[makeQuery(id+"F2.imprint","IMPRINT",EDGE,{"disambiguationData":[TD([[subQ2,-1.0]])],"derivedFrom":subQ1}),1.0]])]});}
            var Q26;
            {var subQ0=sQuery(id+"F2.wireOp",EDGE,"E31.5.0.0");var subQ1=sQuery(id+"F2.wireOp",EDGE,"E30.1");var subQ2=makeQuery(id+"F2.imprint","INTERSECT",VERTEX,{"derivedFrom":[subQ1,subQ0]});Q26=makeQuery(id+"F2.imprint","IMPRINT",FACE,{"disambiguationData":[TD([[makeQuery(id+"F2.imprint","IMPRINT",EDGE,{"disambiguationData":[TD([[subQ2,-1.0]])],"derivedFrom":subQ1}),-1.0]])]});}
            var Q27;
            {var subQ0=sQuery(id+"F2.wireOp",EDGE,"E31.6.0.0");var subQ1=sQuery(id+"F2.wireOp",EDGE,"E31.2.0.3");var subQ2=makeQuery(id+"F2.imprint","INTERSECT",VERTEX,{"derivedFrom":[subQ1,subQ0]});Q27=makeQuery(id+"F2.imprint","IMPRINT",FACE,{"disambiguationData":[TD([[makeQuery(id+"F2.imprint","IMPRINT",EDGE,{"disambiguationData":[TD([[subQ2,-1.0]])],"derivedFrom":subQ1}),1.0]])]});}
            var Q28;
            {var subQ0=sQuery(id+"F2.wireOp",EDGE,"E31.9.0.0");var subQ1=sQuery(id+"F2.wireOp",EDGE,"E31.4.0.3");var subQ2=makeQuery(id+"F2.imprint","INTERSECT",VERTEX,{"derivedFrom":[subQ1,subQ0]});Q28=makeQuery(id+"F2.imprint","IMPRINT",FACE,{"disambiguationData":[TD([[makeQuery(id+"F2.imprint","IMPRINT",EDGE,{"disambiguationData":[TD([[subQ2,-1.0]])],"derivedFrom":subQ1}),1.0]])]});}
            var Q29;
            {var subQ0=sQuery(id+"F2.wireOp",EDGE,"E31.11.0.0");var subQ1=sQuery(id+"F2.wireOp",EDGE,"E31.6.0.3");var subQ2=makeQuery(id+"F2.imprint","INTERSECT",VERTEX,{"derivedFrom":[subQ1,subQ0]});Q29=makeQuery(id+"F2.imprint","IMPRINT",FACE,{"disambiguationData":[TD([[makeQuery(id+"F2.imprint","IMPRINT",EDGE,{"disambiguationData":[TD([[subQ2,-1.0]])],"derivedFrom":subQ1}),1.0]])]});}
            var Q30;
            {var subQ0=sQuery(id+"F2.wireOp",EDGE,"E31.14.0.0");var subQ1=sQuery(id+"F2.wireOp",EDGE,"E31.10.0.3");var subQ2=makeQuery(id+"F2.imprint","INTERSECT",VERTEX,{"derivedFrom":[subQ1,subQ0]});Q30=makeQuery(id+"F2.imprint","IMPRINT",FACE,{"disambiguationData":[TD([[makeQuery(id+"F2.imprint","IMPRINT",EDGE,{"disambiguationData":[TD([[subQ2,-1.0]])],"derivedFrom":subQ1}),1.0]])]});}
            var Q31;
            {var subQ0=sQuery(id+"F2.wireOp",EDGE,"E31.9.0.0");var subQ1=sQuery(id+"F2.wireOp",EDGE,"E31.8.0.3");var subQ2=makeQuery(id+"F2.imprint","INTERSECT",VERTEX,{"derivedFrom":[subQ1,subQ0]});Q31=makeQuery(id+"F2.imprint","IMPRINT",FACE,{"disambiguationData":[TD([[makeQuery(id+"F2.imprint","IMPRINT",EDGE,{"disambiguationData":[TD([[subQ2,1.0]])],"derivedFrom":subQ1}),1.0]])]});}
            var Q32;
            {var subQ0=sQuery(id+"F2.wireOp",EDGE,"E31.3.0.0");var subQ1=sQuery(id+"F2.wireOp",EDGE,"E30.2");var subQ2=makeQuery(id+"F2.imprint","INTERSECT",VERTEX,{"derivedFrom":[subQ1,subQ0]});Q32=makeQuery(id+"F2.imprint","IMPRINT",FACE,{"disambiguationData":[TD([[makeQuery(id+"F2.imprint","IMPRINT",EDGE,{"disambiguationData":[TD([[subQ2,-1.0]])],"derivedFrom":subQ1}),1.0]])]});}
            var Q33;
            {var subQ0=sQuery(id+"F2.wireOp",EDGE,"E31.6.0.0");var subQ1=sQuery(id+"F2.wireOp",EDGE,"E31.5.0.3");var subQ2=makeQuery(id+"F2.imprint","INTERSECT",VERTEX,{"derivedFrom":[subQ1,subQ0]});Q33=makeQuery(id+"F2.imprint","IMPRINT",FACE,{"disambiguationData":[TD([[makeQuery(id+"F2.imprint","IMPRINT",EDGE,{"disambiguationData":[TD([[subQ2,1.0]])],"derivedFrom":subQ1}),1.0]])]});}
            var Q34;
            {var subQ0=sQuery(id+"F2.wireOp",EDGE,"E31.11.0.0");var subQ1=sQuery(id+"F2.wireOp",EDGE,"E31.5.0.3");var subQ2=makeQuery(id+"F2.imprint","INTERSECT",VERTEX,{"derivedFrom":[subQ1,subQ0]});Q34=makeQuery(id+"F2.imprint","IMPRINT",FACE,{"disambiguationData":[TD([[makeQuery(id+"F2.imprint","IMPRINT",EDGE,{"disambiguationData":[TD([[subQ2,-1.0]])],"derivedFrom":subQ1}),1.0]])]});}
            var Q35;
            {var subQ0=sQuery(id+"F2.wireOp",EDGE,"E31.12.0.0");var subQ1=sQuery(id+"F2.wireOp",EDGE,"E31.7.0.3");var subQ2=makeQuery(id+"F2.imprint","INTERSECT",VERTEX,{"derivedFrom":[subQ1,subQ0]});Q35=makeQuery(id+"F2.imprint","IMPRINT",FACE,{"disambiguationData":[TD([[makeQuery(id+"F2.imprint","IMPRINT",EDGE,{"disambiguationData":[TD([[subQ2,-1.0]])],"derivedFrom":subQ1}),1.0]])]});}
            var Q36;
            {var subQ0=sQuery(id+"F2.wireOp",EDGE,"E31.10.0.0");var subQ1=sQuery(id+"F2.wireOp",EDGE,"E31.5.0.3");var subQ2=makeQuery(id+"F2.imprint","INTERSECT",VERTEX,{"derivedFrom":[subQ1,subQ0]});Q36=makeQuery(id+"F2.imprint","IMPRINT",FACE,{"disambiguationData":[TD([[makeQuery(id+"F2.imprint","IMPRINT",EDGE,{"disambiguationData":[TD([[subQ2,-1.0]])],"derivedFrom":subQ1}),1.0]])]});}
            var Q37;
            {var subQ0=sQuery(id+"F2.wireOp",EDGE,"E31.11.0.0");var subQ1=sQuery(id+"F2.wireOp",EDGE,"E31.7.0.3");var subQ2=makeQuery(id+"F2.imprint","INTERSECT",VERTEX,{"derivedFrom":[subQ1,subQ0]});Q37=makeQuery(id+"F2.imprint","IMPRINT",FACE,{"disambiguationData":[TD([[makeQuery(id+"F2.imprint","IMPRINT",EDGE,{"disambiguationData":[TD([[subQ2,-1.0]])],"derivedFrom":subQ1}),1.0]])]});}
            var Q38;
            {var subQ0=sQuery(id+"F2.wireOp",EDGE,"E31.9.0.0");var subQ1=sQuery(id+"F2.wireOp",EDGE,"E31.5.0.3");var subQ2=makeQuery(id+"F2.imprint","INTERSECT",VERTEX,{"derivedFrom":[subQ1,subQ0]});Q38=makeQuery(id+"F2.imprint","IMPRINT",FACE,{"disambiguationData":[TD([[makeQuery(id+"F2.imprint","IMPRINT",EDGE,{"disambiguationData":[TD([[subQ2,-1.0]])],"derivedFrom":subQ1}),1.0]])]});}
            var Q39;
            {var subQ0=sQuery(id+"F2.wireOp",EDGE,"E31.10.0.0");var subQ1=sQuery(id+"F2.wireOp",EDGE,"E31.7.0.3");var subQ2=makeQuery(id+"F2.imprint","INTERSECT",VERTEX,{"derivedFrom":[subQ1,subQ0]});Q39=makeQuery(id+"F2.imprint","IMPRINT",FACE,{"disambiguationData":[TD([[makeQuery(id+"F2.imprint","IMPRINT",EDGE,{"disambiguationData":[TD([[subQ2,-1.0]])],"derivedFrom":subQ1}),1.0]])]});}
            var Q40;
            {var subQ0=sQuery(id+"F2.wireOp",EDGE,"E31.4.0.0");var subQ1=sQuery(id+"F2.wireOp",EDGE,"E31.1.0.3");var subQ2=makeQuery(id+"F2.imprint","INTERSECT",VERTEX,{"derivedFrom":[subQ1,subQ0]});Q40=makeQuery(id+"F2.imprint","IMPRINT",FACE,{"disambiguationData":[TD([[makeQuery(id+"F2.imprint","IMPRINT",EDGE,{"disambiguationData":[TD([[subQ2,-1.0]])],"derivedFrom":subQ1}),1.0]])]});}
            var Q41;
            {var subQ0=sQuery(id+"F2.wireOp",EDGE,"E31.1.0.0");var subQ1=sQuery(id+"F2.wireOp",EDGE,"E30.1");var subQ2=makeQuery(id+"F2.imprint","INTERSECT",VERTEX,{"derivedFrom":[subQ1,subQ0]});Q41=makeQuery(id+"F2.imprint","IMPRINT",FACE,{"disambiguationData":[TD([[makeQuery(id+"F2.imprint","IMPRINT",EDGE,{"disambiguationData":[TD([[subQ2,-1.0]])],"derivedFrom":subQ1}),-1.0]])]});}
            var Q42;
            {var subQ0=sQuery(id+"F2.wireOp",EDGE,"E31.7.0.0");var subQ1=sQuery(id+"F2.wireOp",EDGE,"E31.6.0.3");var subQ2=makeQuery(id+"F2.imprint","INTERSECT",VERTEX,{"derivedFrom":[subQ1,subQ0]});Q42=makeQuery(id+"F2.imprint","IMPRINT",FACE,{"disambiguationData":[TD([[makeQuery(id+"F2.imprint","IMPRINT",EDGE,{"disambiguationData":[TD([[subQ2,1.0]])],"derivedFrom":subQ1}),1.0]])]});}
            var Q43;
            {var subQ0=sQuery(id+"F2.wireOp",EDGE,"E31.2.0.0");var subQ1=sQuery(id+"F2.wireOp",EDGE,"E30.1");var subQ2=makeQuery(id+"F2.imprint","INTERSECT",VERTEX,{"derivedFrom":[subQ1,subQ0]});Q43=makeQuery(id+"F2.imprint","IMPRINT",FACE,{"disambiguationData":[TD([[makeQuery(id+"F2.imprint","IMPRINT",EDGE,{"disambiguationData":[TD([[subQ2,-1.0]])],"derivedFrom":subQ1}),-1.0]])]});}
            var Q44;
            {var subQ0=sQuery(id+"F2.wireOp",EDGE,"E31.3.0.0");var subQ1=sQuery(id+"F2.wireOp",EDGE,"E30.1");var subQ2=makeQuery(id+"F2.imprint","INTERSECT",VERTEX,{"derivedFrom":[subQ1,subQ0]});Q44=makeQuery(id+"F2.imprint","IMPRINT",FACE,{"disambiguationData":[TD([[makeQuery(id+"F2.imprint","IMPRINT",EDGE,{"disambiguationData":[TD([[subQ2,-1.0]])],"derivedFrom":subQ1}),-1.0]])]});}
            var Q45;
            {var subQ0=sQuery(id+"F2.wireOp",EDGE,"E31.8.0.0");var subQ1=sQuery(id+"F2.wireOp",EDGE,"E31.7.0.3");var subQ2=makeQuery(id+"F2.imprint","INTERSECT",VERTEX,{"derivedFrom":[subQ1,subQ0]});Q45=makeQuery(id+"F2.imprint","IMPRINT",FACE,{"disambiguationData":[TD([[makeQuery(id+"F2.imprint","IMPRINT",EDGE,{"disambiguationData":[TD([[subQ2,1.0]])],"derivedFrom":subQ1}),1.0]])]});}
            var Q46;
            {var subQ5=sQuery(id+"F2.wireOp",EDGE,"E30.2");var subQ6=sQuery(id+"F2.wireOp",EDGE,"E30.1");var subQ7=makeQuery(id+"F2.imprint","INTERSECT",VERTEX,{"derivedFrom":[subQ6,subQ5]});Q46=makeQuery(id+"F2.imprint","IMPRINT",FACE,{"disambiguationData":[TD([[makeQuery(id+"F2.imprint","IMPRINT",EDGE,{"disambiguationData":[TD([[subQ7,1.0]])],"derivedFrom":subQ6}),1.0]])]});}
            var Q47;
            {var subQ0=sQuery(id+"F2.wireOp",EDGE,"E31.4.0.0");var subQ1=sQuery(id+"F2.wireOp",EDGE,"E30.1");var subQ2=makeQuery(id+"F2.imprint","INTERSECT",VERTEX,{"derivedFrom":[subQ1,subQ0]});Q47=makeQuery(id+"F2.imprint","IMPRINT",FACE,{"disambiguationData":[TD([[makeQuery(id+"F2.imprint","IMPRINT",EDGE,{"disambiguationData":[TD([[subQ2,-1.0]])],"derivedFrom":subQ1}),-1.0]])]});}
            var Q48;
            {var subQ0=sQuery(id+"F2.wireOp",EDGE,"E31.4.0.0");var subQ1=sQuery(id+"F2.wireOp",EDGE,"E31.3.0.3");var subQ2=makeQuery(id+"F2.imprint","INTERSECT",VERTEX,{"derivedFrom":[subQ1,subQ0]});Q48=makeQuery(id+"F2.imprint","IMPRINT",FACE,{"disambiguationData":[TD([[makeQuery(id+"F2.imprint","IMPRINT",EDGE,{"disambiguationData":[TD([[subQ2,1.0]])],"derivedFrom":subQ1}),1.0]])]});}
            var Q49;
            {var subQ0=sQuery(id+"F2.wireOp",EDGE,"E31.1.0.0");var subQ1=sQuery(id+"F2.wireOp",EDGE,"E30.2");var subQ2=makeQuery(id+"F2.imprint","INTERSECT",VERTEX,{"derivedFrom":[subQ1,subQ0]});Q49=makeQuery(id+"F2.imprint","IMPRINT",FACE,{"disambiguationData":[TD([[makeQuery(id+"F2.imprint","IMPRINT",EDGE,{"disambiguationData":[TD([[subQ2,1.0]])],"derivedFrom":subQ1}),1.0]])]});}
            var Q50;
            {var subQ0=sQuery(id+"F2.wireOp",EDGE,"E31.2.0.0");var subQ1=sQuery(id+"F2.wireOp",EDGE,"E31.1.0.3");var subQ2=makeQuery(id+"F2.imprint","INTERSECT",VERTEX,{"derivedFrom":[subQ1,subQ0]});Q50=makeQuery(id+"F2.imprint","IMPRINT",FACE,{"disambiguationData":[TD([[makeQuery(id+"F2.imprint","IMPRINT",EDGE,{"disambiguationData":[TD([[subQ2,1.0]])],"derivedFrom":subQ1}),1.0]])]});}
            var Q51;
            {var subQ0=sQuery(id+"F2.wireOp",EDGE,"E31.3.0.0");var subQ1=sQuery(id+"F2.wireOp",EDGE,"E31.2.0.3");var subQ2=makeQuery(id+"F2.imprint","INTERSECT",VERTEX,{"derivedFrom":[subQ1,subQ0]});Q51=makeQuery(id+"F2.imprint","IMPRINT",FACE,{"disambiguationData":[TD([[makeQuery(id+"F2.imprint","IMPRINT",EDGE,{"disambiguationData":[TD([[subQ2,1.0]])],"derivedFrom":subQ1}),1.0]])]});}
            var Q52;
            {var subQ0=sQuery(id+"F2.wireOp",EDGE,"E31.5.0.0");var subQ1=sQuery(id+"F2.wireOp",EDGE,"E30.2");var subQ2=makeQuery(id+"F2.imprint","INTERSECT",VERTEX,{"derivedFrom":[subQ1,subQ0]});Q52=makeQuery(id+"F2.imprint","IMPRINT",FACE,{"disambiguationData":[TD([[makeQuery(id+"F2.imprint","IMPRINT",EDGE,{"disambiguationData":[TD([[subQ2,-1.0]])],"derivedFrom":subQ1}),1.0]])]});}
            var Q53;
            {var subQ0=sQuery(id+"F2.wireOp",EDGE,"E31.6.0.0");var subQ1=sQuery(id+"F2.wireOp",EDGE,"E30.2");var subQ2=makeQuery(id+"F2.imprint","INTERSECT",VERTEX,{"derivedFrom":[subQ1,subQ0]});Q53=makeQuery(id+"F2.imprint","IMPRINT",FACE,{"disambiguationData":[TD([[makeQuery(id+"F2.imprint","IMPRINT",EDGE,{"disambiguationData":[TD([[subQ2,-1.0]])],"derivedFrom":subQ1}),1.0]])]});}
            var Q54;
            {var subQ0=sQuery(id+"F2.wireOp",EDGE,"E31.13.0.0");var subQ1=sQuery(id+"F2.wireOp",EDGE,"E31.8.0.3");var subQ2=makeQuery(id+"F2.imprint","INTERSECT",VERTEX,{"derivedFrom":[subQ1,subQ0]});Q54=makeQuery(id+"F2.imprint","IMPRINT",FACE,{"disambiguationData":[TD([[makeQuery(id+"F2.imprint","IMPRINT",EDGE,{"disambiguationData":[TD([[subQ2,-1.0]])],"derivedFrom":subQ1}),1.0]])]});}
            var Q55;
            {var subQ8=sQuery(id+"F2.wireOp",EDGE,"E31.2.0.4");var subQ9=sQuery(id+"F2.wireOp",EDGE,"E31.2.0.3");var subQ10=makeQuery(id+"F2.imprint","INTERSECT",VERTEX,{"derivedFrom":[subQ9,subQ8]});Q55=makeQuery(id+"F2.imprint","IMPRINT",FACE,{"disambiguationData":[TD([[makeQuery(id+"F2.imprint","IMPRINT",EDGE,{"disambiguationData":[TD([[subQ10,-1.0]])],"derivedFrom":subQ9}),1.0]])]});}
            var Q56;
            {var subQ0=sQuery(id+"F2.wireOp",EDGE,"E31.14.0.0");var subQ1=sQuery(id+"F2.wireOp",EDGE,"E31.8.0.3");var subQ2=makeQuery(id+"F2.imprint","INTERSECT",VERTEX,{"derivedFrom":[subQ1,subQ0]});Q56=makeQuery(id+"F2.imprint","IMPRINT",FACE,{"disambiguationData":[TD([[makeQuery(id+"F2.imprint","IMPRINT",EDGE,{"disambiguationData":[TD([[subQ2,-1.0]])],"derivedFrom":subQ1}),1.0]])]});}
            var Q57;
            {var subQ0=sQuery(id+"F2.wireOp",EDGE,"E31.7.0.0");var subQ1=sQuery(id+"F2.wireOp",EDGE,"E31.2.0.3");var subQ2=makeQuery(id+"F2.imprint","INTERSECT",VERTEX,{"derivedFrom":[subQ1,subQ0]});Q57=makeQuery(id+"F2.imprint","IMPRINT",FACE,{"disambiguationData":[TD([[makeQuery(id+"F2.imprint","IMPRINT",EDGE,{"disambiguationData":[TD([[subQ2,-1.0]])],"derivedFrom":subQ1}),1.0]])]});}
            var Q58;
            {var subQ5=sQuery(id+"F2.wireOp",EDGE,"E31.7.0.4");var subQ6=sQuery(id+"F2.wireOp",EDGE,"E31.7.0.3");var subQ7=makeQuery(id+"F2.imprint","INTERSECT",VERTEX,{"derivedFrom":[subQ6,subQ5]});Q58=makeQuery(id+"F2.imprint","IMPRINT",FACE,{"disambiguationData":[TD([[makeQuery(id+"F2.imprint","IMPRINT",EDGE,{"disambiguationData":[TD([[subQ7,-1.0]])],"derivedFrom":subQ6}),1.0]])]});}
            var Q59;
            {var subQ0=sQuery(id+"F2.wireOp",EDGE,"E31.5.0.4");var subQ1=sQuery(id+"F2.wireOp",EDGE,"E31.5.0.3");var subQ2=makeQuery(id+"F2.imprint","INTERSECT",VERTEX,{"derivedFrom":[subQ1,subQ0]});Q59=makeQuery(id+"F2.imprint","IMPRINT",FACE,{"disambiguationData":[TD([[makeQuery(id+"F2.imprint","IMPRINT",EDGE,{"disambiguationData":[TD([[subQ2,-1.0]])],"derivedFrom":subQ1}),-1.0]])]});}
            var Q60;
            {var subQ0=sQuery(id+"F2.wireOp",EDGE,"E31.9.0.0");var subQ1=sQuery(id+"F2.wireOp",EDGE,"E31.3.0.3");var subQ2=makeQuery(id+"F2.imprint","INTERSECT",VERTEX,{"derivedFrom":[subQ1,subQ0]});Q60=makeQuery(id+"F2.imprint","IMPRINT",FACE,{"disambiguationData":[TD([[makeQuery(id+"F2.imprint","IMPRINT",EDGE,{"disambiguationData":[TD([[subQ2,-1.0]])],"derivedFrom":subQ1}),1.0]])]});}
            var Q61;
            {var subQ0=sQuery(id+"F2.wireOp",EDGE,"E31.7.0.0");var subQ1=sQuery(id+"F2.wireOp",EDGE,"E31.1.0.3");var subQ2=makeQuery(id+"F2.imprint","INTERSECT",VERTEX,{"derivedFrom":[subQ1,subQ0]});Q61=makeQuery(id+"F2.imprint","IMPRINT",FACE,{"disambiguationData":[TD([[makeQuery(id+"F2.imprint","IMPRINT",EDGE,{"disambiguationData":[TD([[subQ2,-1.0]])],"derivedFrom":subQ1}),1.0]])]});}
            var Q62;
            {var subQ0=sQuery(id+"F2.wireOp",EDGE,"E31.13.0.0");var subQ1=sQuery(id+"F2.wireOp",EDGE,"E31.7.0.3");var subQ2=makeQuery(id+"F2.imprint","INTERSECT",VERTEX,{"derivedFrom":[subQ1,subQ0]});Q62=makeQuery(id+"F2.imprint","IMPRINT",FACE,{"disambiguationData":[TD([[makeQuery(id+"F2.imprint","IMPRINT",EDGE,{"disambiguationData":[TD([[subQ2,-1.0]])],"derivedFrom":subQ1}),1.0]])]});}
            var Q63;
            {var subQ0=sQuery(id+"F2.wireOp",EDGE,"E31.8.0.0");var subQ1=sQuery(id+"F2.wireOp",EDGE,"E31.3.0.3");var subQ2=makeQuery(id+"F2.imprint","INTERSECT",VERTEX,{"derivedFrom":[subQ1,subQ0]});Q63=makeQuery(id+"F2.imprint","IMPRINT",FACE,{"disambiguationData":[TD([[makeQuery(id+"F2.imprint","IMPRINT",EDGE,{"disambiguationData":[TD([[subQ2,-1.0]])],"derivedFrom":subQ1}),1.0]])]});}
            var Q64;
            {var subQ0=sQuery(id+"F2.wireOp",EDGE,"E31.6.0.0");var subQ1=sQuery(id+"F2.wireOp",EDGE,"E31.1.0.3");var subQ2=makeQuery(id+"F2.imprint","INTERSECT",VERTEX,{"derivedFrom":[subQ1,subQ0]});Q64=makeQuery(id+"F2.imprint","IMPRINT",FACE,{"disambiguationData":[TD([[makeQuery(id+"F2.imprint","IMPRINT",EDGE,{"disambiguationData":[TD([[subQ2,-1.0]])],"derivedFrom":subQ1}),1.0]])]});}
            var Q65;
            {var subQ6=sQuery(id+"F2.wireOp",EDGE,"E31.9.0.4");var subQ7=sQuery(id+"F2.wireOp",EDGE,"E31.9.0.3");var subQ8=makeQuery(id+"F2.imprint","INTERSECT",VERTEX,{"derivedFrom":[subQ7,subQ6]});Q65=makeQuery(id+"F2.imprint","IMPRINT",FACE,{"disambiguationData":[TD([[makeQuery(id+"F2.imprint","IMPRINT",EDGE,{"disambiguationData":[TD([[subQ8,-1.0]])],"derivedFrom":subQ7}),1.0]])]});}
            var Q66;
            {var subQ0=sQuery(id+"F2.wireOp",EDGE,"E31.7.0.0");var subQ1=sQuery(id+"F2.wireOp",EDGE,"E31.3.0.3");var subQ2=makeQuery(id+"F2.imprint","INTERSECT",VERTEX,{"derivedFrom":[subQ1,subQ0]});Q66=makeQuery(id+"F2.imprint","IMPRINT",FACE,{"disambiguationData":[TD([[makeQuery(id+"F2.imprint","IMPRINT",EDGE,{"disambiguationData":[TD([[subQ2,-1.0]])],"derivedFrom":subQ1}),1.0]])]});}
            var Q67;
            {var subQ0=sQuery(id+"F2.wireOp",EDGE,"E31.5.0.0");var subQ1=sQuery(id+"F2.wireOp",EDGE,"E31.1.0.3");var subQ2=makeQuery(id+"F2.imprint","INTERSECT",VERTEX,{"derivedFrom":[subQ1,subQ0]});Q67=makeQuery(id+"F2.imprint","IMPRINT",FACE,{"disambiguationData":[TD([[makeQuery(id+"F2.imprint","IMPRINT",EDGE,{"disambiguationData":[TD([[subQ2,-1.0]])],"derivedFrom":subQ1}),1.0]])]});}
            var Q68;
            {var subQ0=sQuery(id+"F2.wireOp",EDGE,"E31.14.0.0");var subQ1=sQuery(id+"F2.wireOp",EDGE,"E31.9.0.3");var subQ2=makeQuery(id+"F2.imprint","INTERSECT",VERTEX,{"derivedFrom":[subQ1,subQ0]});Q68=makeQuery(id+"F2.imprint","IMPRINT",FACE,{"disambiguationData":[TD([[makeQuery(id+"F2.imprint","IMPRINT",EDGE,{"disambiguationData":[TD([[subQ2,-1.0]])],"derivedFrom":subQ1}),1.0]])]});}
            var Q69;
            {var subQ0=sQuery(id+"F2.wireOp",EDGE,"E31.13.0.0");var subQ1=sQuery(id+"F2.wireOp",EDGE,"E31.9.0.3");var subQ2=makeQuery(id+"F2.imprint","INTERSECT",VERTEX,{"derivedFrom":[subQ1,subQ0]});Q69=makeQuery(id+"F2.imprint","IMPRINT",FACE,{"disambiguationData":[TD([[makeQuery(id+"F2.imprint","IMPRINT",EDGE,{"disambiguationData":[TD([[subQ2,-1.0]])],"derivedFrom":subQ1}),1.0]])]});}
            var Q70;
            {var subQ0=sQuery(id+"F2.wireOp",EDGE,"E31.7.0.4");var subQ1=sQuery(id+"F2.wireOp",EDGE,"E31.7.0.3");var subQ2=makeQuery(id+"F2.imprint","INTERSECT",VERTEX,{"derivedFrom":[subQ1,subQ0]});Q70=makeQuery(id+"F2.imprint","IMPRINT",FACE,{"disambiguationData":[TD([[makeQuery(id+"F2.imprint","IMPRINT",EDGE,{"disambiguationData":[TD([[subQ2,-1.0]])],"derivedFrom":subQ1}),-1.0]])]});}
            var Q71;
            {var subQ6=sQuery(id+"F2.wireOp",EDGE,"E31.8.0.4");var subQ7=sQuery(id+"F2.wireOp",EDGE,"E31.8.0.3");var subQ8=makeQuery(id+"F2.imprint","INTERSECT",VERTEX,{"derivedFrom":[subQ7,subQ6]});Q71=makeQuery(id+"F2.imprint","IMPRINT",FACE,{"disambiguationData":[TD([[makeQuery(id+"F2.imprint","IMPRINT",EDGE,{"disambiguationData":[TD([[subQ8,-1.0]])],"derivedFrom":subQ7}),1.0]])]});}
            var Q72;
            {var subQ0=sQuery(id+"F2.wireOp",EDGE,"E31.12.0.0");var subQ1=sQuery(id+"F2.wireOp",EDGE,"E31.6.0.3");var subQ2=makeQuery(id+"F2.imprint","INTERSECT",VERTEX,{"derivedFrom":[subQ1,subQ0]});Q72=makeQuery(id+"F2.imprint","IMPRINT",FACE,{"disambiguationData":[TD([[makeQuery(id+"F2.imprint","IMPRINT",EDGE,{"disambiguationData":[TD([[subQ2,-1.0]])],"derivedFrom":subQ1}),1.0]])]});}
            var Q73;
            {var subQ0=sQuery(id+"F2.wireOp",EDGE,"E31.10.0.0");var subQ1=sQuery(id+"F2.wireOp",EDGE,"E31.4.0.3");var subQ2=makeQuery(id+"F2.imprint","INTERSECT",VERTEX,{"derivedFrom":[subQ1,subQ0]});Q73=makeQuery(id+"F2.imprint","IMPRINT",FACE,{"disambiguationData":[TD([[makeQuery(id+"F2.imprint","IMPRINT",EDGE,{"disambiguationData":[TD([[subQ2,-1.0]])],"derivedFrom":subQ1}),1.0]])]});}
            var Q74;
            {var subQ0=sQuery(id+"F2.wireOp",EDGE,"E31.8.0.0");var subQ1=sQuery(id+"F2.wireOp",EDGE,"E31.2.0.3");var subQ2=makeQuery(id+"F2.imprint","INTERSECT",VERTEX,{"derivedFrom":[subQ1,subQ0]});Q74=makeQuery(id+"F2.imprint","IMPRINT",FACE,{"disambiguationData":[TD([[makeQuery(id+"F2.imprint","IMPRINT",EDGE,{"disambiguationData":[TD([[subQ2,-1.0]])],"derivedFrom":subQ1}),1.0]])]});}
            var Q75;
            {var subQ0=sQuery(id+"F2.wireOp",EDGE,"E31.10.0.4");var subQ1=sQuery(id+"F2.wireOp",EDGE,"E31.10.0.3");var subQ2=makeQuery(id+"F2.imprint","INTERSECT",VERTEX,{"derivedFrom":[subQ1,subQ0]});Q75=makeQuery(id+"F2.imprint","IMPRINT",FACE,{"disambiguationData":[TD([[makeQuery(id+"F2.imprint","IMPRINT",EDGE,{"disambiguationData":[TD([[subQ2,-1.0]])],"derivedFrom":subQ1}),1.0]])]});}
            var Q76;
            {var subQ5=sQuery(id+"F2.wireOp",EDGE,"E31.1.0.4");var subQ10=sQuery(id+"F2.wireOp",EDGE,"E31.1.0.3");var subQ11=makeQuery(id+"F2.imprint","INTERSECT",VERTEX,{"derivedFrom":[subQ10,subQ5]});Q76=makeQuery(id+"F2.imprint","IMPRINT",FACE,{"disambiguationData":[TD([[makeQuery(id+"F2.imprint","IMPRINT",EDGE,{"disambiguationData":[TD([[subQ11,-1.0]])],"derivedFrom":subQ10}),1.0]])]});}
            var Q77;
            {var subQ0=sQuery(id+"F2.wireOp",EDGE,"E30.2");var subQ1=sQuery(id+"F2.wireOp",EDGE,"E30.1");var subQ2=makeQuery(id+"F2.imprint","INTERSECT",VERTEX,{"derivedFrom":[subQ1,subQ0]});Q77=makeQuery(id+"F2.imprint","IMPRINT",FACE,{"disambiguationData":[TD([[makeQuery(id+"F2.imprint","IMPRINT",EDGE,{"disambiguationData":[TD([[subQ2,1.0]])],"derivedFrom":subQ1}),-1.0]])]});}
            var Q78;
            {var subQ0=sQuery(id+"F2.wireOp",EDGE,"E31.1.0.4");var subQ1=sQuery(id+"F2.wireOp",EDGE,"E31.1.0.3");var subQ2=makeQuery(id+"F2.imprint","INTERSECT",VERTEX,{"derivedFrom":[subQ1,subQ0]});Q78=makeQuery(id+"F2.imprint","IMPRINT",FACE,{"disambiguationData":[TD([[makeQuery(id+"F2.imprint","IMPRINT",EDGE,{"disambiguationData":[TD([[subQ2,-1.0]])],"derivedFrom":subQ1}),-1.0]])]});}
            var Q79;
            {var subQ0=sQuery(id+"F2.wireOp",EDGE,"E31.11.0.0");var subQ1=sQuery(id+"F2.wireOp",EDGE,"E31.10.0.4");var subQ2=makeQuery(id+"F2.imprint","INTERSECT",VERTEX,{"derivedFrom":[subQ1,subQ0]});Q79=makeQuery(id+"F2.imprint","IMPRINT",FACE,{"disambiguationData":[TD([[makeQuery(id+"F2.imprint","IMPRINT",EDGE,{"disambiguationData":[TD([[subQ2,-1.0]])],"derivedFrom":subQ1}),1.0]])]});}
            var Q80;
            {var subQ0=sQuery(id+"F2.wireOp",EDGE,"E31.4.0.4");var subQ1=sQuery(id+"F2.wireOp",EDGE,"E31.4.0.3");var subQ2=makeQuery(id+"F2.imprint","INTERSECT",VERTEX,{"derivedFrom":[subQ1,subQ0]});Q80=makeQuery(id+"F2.imprint","IMPRINT",FACE,{"disambiguationData":[TD([[makeQuery(id+"F2.imprint","IMPRINT",EDGE,{"disambiguationData":[TD([[subQ2,-1.0]])],"derivedFrom":subQ1}),-1.0]])]});}
            var Q81;
            {var subQ0=sQuery(id+"F2.wireOp",EDGE,"E31.6.0.4");var subQ1=sQuery(id+"F2.wireOp",EDGE,"E31.6.0.3");var subQ2=makeQuery(id+"F2.imprint","INTERSECT",VERTEX,{"derivedFrom":[subQ1,subQ0]});Q81=makeQuery(id+"F2.imprint","IMPRINT",FACE,{"disambiguationData":[TD([[makeQuery(id+"F2.imprint","IMPRINT",EDGE,{"disambiguationData":[TD([[subQ2,-1.0]])],"derivedFrom":subQ1}),-1.0]])]});}
            var Q82;
            {var subQ0=sQuery(id+"F2.wireOp",EDGE,"E31.7.0.0");var subQ1=sQuery(id+"F2.wireOp",EDGE,"E31.6.0.4");var subQ2=makeQuery(id+"F2.imprint","INTERSECT",VERTEX,{"derivedFrom":[subQ1,subQ0]});Q82=makeQuery(id+"F2.imprint","IMPRINT",FACE,{"disambiguationData":[TD([[makeQuery(id+"F2.imprint","IMPRINT",EDGE,{"disambiguationData":[TD([[subQ2,-1.0]])],"derivedFrom":subQ1}),1.0]])]});}
            var Q83;
            {var subQ0=sQuery(id+"F2.wireOp",EDGE,"E31.8.0.0");var subQ1=sQuery(id+"F2.wireOp",EDGE,"E31.7.0.4");var subQ2=makeQuery(id+"F2.imprint","INTERSECT",VERTEX,{"derivedFrom":[subQ1,subQ0]});Q83=makeQuery(id+"F2.imprint","IMPRINT",FACE,{"disambiguationData":[TD([[makeQuery(id+"F2.imprint","IMPRINT",EDGE,{"disambiguationData":[TD([[subQ2,-1.0]])],"derivedFrom":subQ1}),1.0]])]});}
            var Q84;
            {var subQ0=sQuery(id+"F2.wireOp",EDGE,"E31.8.0.4");var subQ1=sQuery(id+"F2.wireOp",EDGE,"E31.8.0.3");var subQ2=makeQuery(id+"F2.imprint","INTERSECT",VERTEX,{"derivedFrom":[subQ1,subQ0]});Q84=makeQuery(id+"F2.imprint","IMPRINT",FACE,{"disambiguationData":[TD([[makeQuery(id+"F2.imprint","IMPRINT",EDGE,{"disambiguationData":[TD([[subQ2,-1.0]])],"derivedFrom":subQ1}),-1.0]])]});}
            var Q85;
            {var subQ0=sQuery(id+"F2.wireOp",EDGE,"E31.3.0.4");var subQ1=sQuery(id+"F2.wireOp",EDGE,"E31.3.0.3");var subQ2=makeQuery(id+"F2.imprint","INTERSECT",VERTEX,{"derivedFrom":[subQ1,subQ0]});Q85=makeQuery(id+"F2.imprint","IMPRINT",FACE,{"disambiguationData":[TD([[makeQuery(id+"F2.imprint","IMPRINT",EDGE,{"disambiguationData":[TD([[subQ2,-1.0]])],"derivedFrom":subQ1}),-1.0]])]});}
            var Q86;
            {var subQ0=sQuery(id+"F2.wireOp",EDGE,"E31.1.0.0");var subQ1=sQuery(id+"F2.wireOp",EDGE,"E30.1");var subQ2=makeQuery(id+"F2.imprint","INTERSECT",VERTEX,{"derivedFrom":[subQ1,subQ0]});Q86=makeQuery(id+"F2.imprint","IMPRINT",FACE,{"disambiguationData":[TD([[makeQuery(id+"F2.imprint","IMPRINT",EDGE,{"disambiguationData":[TD([[subQ2,-1.0]])],"derivedFrom":subQ1}),1.0]])]});}
            var Q87;
            {var subQ0=sQuery(id+"F2.wireOp",EDGE,"E31.2.0.4");var subQ1=sQuery(id+"F2.wireOp",EDGE,"E31.2.0.3");var subQ2=makeQuery(id+"F2.imprint","INTERSECT",VERTEX,{"derivedFrom":[subQ1,subQ0]});Q87=makeQuery(id+"F2.imprint","IMPRINT",FACE,{"disambiguationData":[TD([[makeQuery(id+"F2.imprint","IMPRINT",EDGE,{"disambiguationData":[TD([[subQ2,-1.0]])],"derivedFrom":subQ1}),-1.0]])]});}
            var Q88;
            {var subQ0=sQuery(id+"F2.wireOp",EDGE,"E31.5.0.0");var subQ1=sQuery(id+"F2.wireOp",EDGE,"E30.1");var subQ2=makeQuery(id+"F2.imprint","INTERSECT",VERTEX,{"derivedFrom":[subQ1,subQ0]});Q88=makeQuery(id+"F2.imprint","IMPRINT",FACE,{"disambiguationData":[TD([[makeQuery(id+"F2.imprint","IMPRINT",EDGE,{"disambiguationData":[TD([[subQ2,-1.0]])],"derivedFrom":subQ1}),1.0]])]});}
            var Q89;
            {var subQ0=sQuery(id+"F2.wireOp",EDGE,"E31.6.0.0");var subQ1=sQuery(id+"F2.wireOp",EDGE,"E31.2.0.4");var subQ2=makeQuery(id+"F2.imprint","INTERSECT",VERTEX,{"derivedFrom":[subQ1,subQ0]});Q89=makeQuery(id+"F2.imprint","IMPRINT",FACE,{"disambiguationData":[TD([[makeQuery(id+"F2.imprint","IMPRINT",EDGE,{"disambiguationData":[TD([[subQ2,-1.0]])],"derivedFrom":subQ1}),1.0]])]});}
            var Q90;
            {var subQ0=sQuery(id+"F2.wireOp",EDGE,"E31.5.0.0");var subQ1=sQuery(id+"F2.wireOp",EDGE,"E31.4.0.4");var subQ2=makeQuery(id+"F2.imprint","INTERSECT",VERTEX,{"derivedFrom":[subQ1,subQ0]});Q90=makeQuery(id+"F2.imprint","IMPRINT",FACE,{"disambiguationData":[TD([[makeQuery(id+"F2.imprint","IMPRINT",EDGE,{"disambiguationData":[TD([[subQ2,-1.0]])],"derivedFrom":subQ1}),1.0]])]});}
            var Q91;
            {var subQ0=sQuery(id+"F2.wireOp",EDGE,"E31.7.0.0");var subQ1=sQuery(id+"F2.wireOp",EDGE,"E31.4.0.4");var subQ2=makeQuery(id+"F2.imprint","INTERSECT",VERTEX,{"derivedFrom":[subQ1,subQ0]});Q91=makeQuery(id+"F2.imprint","IMPRINT",FACE,{"disambiguationData":[TD([[makeQuery(id+"F2.imprint","IMPRINT",EDGE,{"disambiguationData":[TD([[subQ2,-1.0]])],"derivedFrom":subQ1}),1.0]])]});}
            var Q92;
            {var subQ0=sQuery(id+"F2.wireOp",EDGE,"E31.10.0.0");var subQ1=sQuery(id+"F2.wireOp",EDGE,"E31.8.0.4");var subQ2=makeQuery(id+"F2.imprint","INTERSECT",VERTEX,{"derivedFrom":[subQ1,subQ0]});Q92=makeQuery(id+"F2.imprint","IMPRINT",FACE,{"disambiguationData":[TD([[makeQuery(id+"F2.imprint","IMPRINT",EDGE,{"disambiguationData":[TD([[subQ2,-1.0]])],"derivedFrom":subQ1}),1.0]])]});}
            var Q93;
            {var subQ0=sQuery(id+"F2.wireOp",EDGE,"E31.5.0.0");var subQ1=sQuery(id+"F2.wireOp",EDGE,"E31.2.0.4");var subQ2=makeQuery(id+"F2.imprint","INTERSECT",VERTEX,{"derivedFrom":[subQ1,subQ0]});Q93=makeQuery(id+"F2.imprint","IMPRINT",FACE,{"disambiguationData":[TD([[makeQuery(id+"F2.imprint","IMPRINT",EDGE,{"disambiguationData":[TD([[subQ2,-1.0]])],"derivedFrom":subQ1}),1.0]])]});}
            var Q94;
            {var subQ0=sQuery(id+"F2.wireOp",EDGE,"E31.6.0.0");var subQ1=sQuery(id+"F2.wireOp",EDGE,"E31.4.0.4");var subQ2=makeQuery(id+"F2.imprint","INTERSECT",VERTEX,{"derivedFrom":[subQ1,subQ0]});Q94=makeQuery(id+"F2.imprint","IMPRINT",FACE,{"disambiguationData":[TD([[makeQuery(id+"F2.imprint","IMPRINT",EDGE,{"disambiguationData":[TD([[subQ2,-1.0]])],"derivedFrom":subQ1}),1.0]])]});}
            var Q95;
            {var subQ0=sQuery(id+"F2.wireOp",EDGE,"E31.8.0.0");var subQ1=sQuery(id+"F2.wireOp",EDGE,"E31.6.0.4");var subQ2=makeQuery(id+"F2.imprint","INTERSECT",VERTEX,{"derivedFrom":[subQ1,subQ0]});Q95=makeQuery(id+"F2.imprint","IMPRINT",FACE,{"disambiguationData":[TD([[makeQuery(id+"F2.imprint","IMPRINT",EDGE,{"disambiguationData":[TD([[subQ2,-1.0]])],"derivedFrom":subQ1}),1.0]])]});}
            var Q96;
            {var subQ0=sQuery(id+"F2.wireOp",EDGE,"E31.4.0.0");var subQ1=sQuery(id+"F2.wireOp",EDGE,"E31.2.0.4");var subQ2=makeQuery(id+"F2.imprint","INTERSECT",VERTEX,{"derivedFrom":[subQ1,subQ0]});Q96=makeQuery(id+"F2.imprint","IMPRINT",FACE,{"disambiguationData":[TD([[makeQuery(id+"F2.imprint","IMPRINT",EDGE,{"disambiguationData":[TD([[subQ2,-1.0]])],"derivedFrom":subQ1}),1.0]])]});}
            var Q97;
            {var subQ0=sQuery(id+"F2.wireOp",EDGE,"E31.10.0.0");var subQ1=sQuery(id+"F2.wireOp",EDGE,"E31.9.0.4");var subQ2=makeQuery(id+"F2.imprint","INTERSECT",VERTEX,{"derivedFrom":[subQ1,subQ0]});Q97=makeQuery(id+"F2.imprint","IMPRINT",FACE,{"disambiguationData":[TD([[makeQuery(id+"F2.imprint","IMPRINT",EDGE,{"disambiguationData":[TD([[subQ2,-1.0]])],"derivedFrom":subQ1}),1.0]])]});}
            var Q98;
            {var subQ0=sQuery(id+"F2.wireOp",EDGE,"E31.9.0.0");var subQ1=sQuery(id+"F2.wireOp",EDGE,"E31.8.0.4");var subQ2=makeQuery(id+"F2.imprint","INTERSECT",VERTEX,{"derivedFrom":[subQ1,subQ0]});Q98=makeQuery(id+"F2.imprint","IMPRINT",FACE,{"disambiguationData":[TD([[makeQuery(id+"F2.imprint","IMPRINT",EDGE,{"disambiguationData":[TD([[subQ2,-1.0]])],"derivedFrom":subQ1}),1.0]])]});}
            var Q99;
            {var subQ0=sQuery(id+"F2.wireOp",EDGE,"E31.4.0.0");var subQ1=sQuery(id+"F2.wireOp",EDGE,"E30.1");var subQ2=makeQuery(id+"F2.imprint","INTERSECT",VERTEX,{"derivedFrom":[subQ1,subQ0]});Q99=makeQuery(id+"F2.imprint","IMPRINT",FACE,{"disambiguationData":[TD([[makeQuery(id+"F2.imprint","IMPRINT",EDGE,{"disambiguationData":[TD([[subQ2,-1.0]])],"derivedFrom":subQ1}),1.0]])]});}
            var Q100;
            {var subQ0=sQuery(id+"F2.wireOp",EDGE,"E31.12.0.0");var subQ1=sQuery(id+"F2.wireOp",EDGE,"E31.8.0.4");var subQ2=makeQuery(id+"F2.imprint","INTERSECT",VERTEX,{"derivedFrom":[subQ1,subQ0]});Q100=makeQuery(id+"F2.imprint","IMPRINT",FACE,{"disambiguationData":[TD([[makeQuery(id+"F2.imprint","IMPRINT",EDGE,{"disambiguationData":[TD([[subQ2,-1.0]])],"derivedFrom":subQ1}),1.0]])]});}
            var Q101;
            {var subQ0=sQuery(id+"F2.wireOp",EDGE,"E31.11.0.0");var subQ1=sQuery(id+"F2.wireOp",EDGE,"E31.6.0.4");var subQ2=makeQuery(id+"F2.imprint","INTERSECT",VERTEX,{"derivedFrom":[subQ1,subQ0]});Q101=makeQuery(id+"F2.imprint","IMPRINT",FACE,{"disambiguationData":[TD([[makeQuery(id+"F2.imprint","IMPRINT",EDGE,{"disambiguationData":[TD([[subQ2,-1.0]])],"derivedFrom":subQ1}),1.0]])]});}
            var Q102;
            {var subQ0=sQuery(id+"F2.wireOp",EDGE,"E31.9.0.0");var subQ1=sQuery(id+"F2.wireOp",EDGE,"E31.4.0.4");var subQ2=makeQuery(id+"F2.imprint","INTERSECT",VERTEX,{"derivedFrom":[subQ1,subQ0]});Q102=makeQuery(id+"F2.imprint","IMPRINT",FACE,{"disambiguationData":[TD([[makeQuery(id+"F2.imprint","IMPRINT",EDGE,{"disambiguationData":[TD([[subQ2,-1.0]])],"derivedFrom":subQ1}),1.0]])]});}
            var Q103;
            {var subQ0=sQuery(id+"F2.wireOp",EDGE,"E31.13.0.0");var subQ1=sQuery(id+"F2.wireOp",EDGE,"E31.8.0.4");var subQ2=makeQuery(id+"F2.imprint","INTERSECT",VERTEX,{"derivedFrom":[subQ1,subQ0]});Q103=makeQuery(id+"F2.imprint","IMPRINT",FACE,{"disambiguationData":[TD([[makeQuery(id+"F2.imprint","IMPRINT",EDGE,{"disambiguationData":[TD([[subQ2,-1.0]])],"derivedFrom":subQ1}),1.0]])]});}
            var Q104;
            {var subQ0=sQuery(id+"F2.wireOp",EDGE,"E31.7.0.0");var subQ1=sQuery(id+"F2.wireOp",EDGE,"E31.5.0.4");var subQ2=makeQuery(id+"F2.imprint","INTERSECT",VERTEX,{"derivedFrom":[subQ1,subQ0]});Q104=makeQuery(id+"F2.imprint","IMPRINT",FACE,{"disambiguationData":[TD([[makeQuery(id+"F2.imprint","IMPRINT",EDGE,{"disambiguationData":[TD([[subQ2,-1.0]])],"derivedFrom":subQ1}),1.0]])]});}
            var Q105;
            {var subQ0=sQuery(id+"F2.wireOp",EDGE,"E31.3.0.0");var subQ1=sQuery(id+"F2.wireOp",EDGE,"E31.1.0.4");var subQ2=makeQuery(id+"F2.imprint","INTERSECT",VERTEX,{"derivedFrom":[subQ1,subQ0]});Q105=makeQuery(id+"F2.imprint","IMPRINT",FACE,{"disambiguationData":[TD([[makeQuery(id+"F2.imprint","IMPRINT",EDGE,{"disambiguationData":[TD([[subQ2,-1.0]])],"derivedFrom":subQ1}),1.0]])]});}
            var Q106;
            {var subQ0=sQuery(id+"F2.wireOp",EDGE,"E31.2.0.0");var subQ1=sQuery(id+"F2.wireOp",EDGE,"E30.1");var subQ2=makeQuery(id+"F2.imprint","INTERSECT",VERTEX,{"derivedFrom":[subQ1,subQ0]});Q106=makeQuery(id+"F2.imprint","IMPRINT",FACE,{"disambiguationData":[TD([[makeQuery(id+"F2.imprint","IMPRINT",EDGE,{"disambiguationData":[TD([[subQ2,-1.0]])],"derivedFrom":subQ1}),1.0]])]});}
            var Q107;
            {var subQ0=sQuery(id+"F2.wireOp",EDGE,"E31.12.0.0");var subQ1=sQuery(id+"F2.wireOp",EDGE,"E31.7.0.4");var subQ2=makeQuery(id+"F2.imprint","INTERSECT",VERTEX,{"derivedFrom":[subQ1,subQ0]});Q107=makeQuery(id+"F2.imprint","IMPRINT",FACE,{"disambiguationData":[TD([[makeQuery(id+"F2.imprint","IMPRINT",EDGE,{"disambiguationData":[TD([[subQ2,-1.0]])],"derivedFrom":subQ1}),1.0]])]});}
            var Q108;
            {var subQ0=sQuery(id+"F2.wireOp",EDGE,"E31.10.0.0");var subQ1=sQuery(id+"F2.wireOp",EDGE,"E31.5.0.4");var subQ2=makeQuery(id+"F2.imprint","INTERSECT",VERTEX,{"derivedFrom":[subQ1,subQ0]});Q108=makeQuery(id+"F2.imprint","IMPRINT",FACE,{"disambiguationData":[TD([[makeQuery(id+"F2.imprint","IMPRINT",EDGE,{"disambiguationData":[TD([[subQ2,-1.0]])],"derivedFrom":subQ1}),1.0]])]});}
            var Q109;
            {var subQ0=sQuery(id+"F2.wireOp",EDGE,"E31.12.0.0");var subQ1=sQuery(id+"F2.wireOp",EDGE,"E31.10.0.4");var subQ2=makeQuery(id+"F2.imprint","INTERSECT",VERTEX,{"derivedFrom":[subQ1,subQ0]});Q109=makeQuery(id+"F2.imprint","IMPRINT",FACE,{"disambiguationData":[TD([[makeQuery(id+"F2.imprint","IMPRINT",EDGE,{"disambiguationData":[TD([[subQ2,-1.0]])],"derivedFrom":subQ1}),1.0]])]});}
            var Q110;
            {var subQ0=sQuery(id+"F2.wireOp",EDGE,"E31.10.0.0");var subQ1=sQuery(id+"F2.wireOp",EDGE,"E31.6.0.4");var subQ2=makeQuery(id+"F2.imprint","INTERSECT",VERTEX,{"derivedFrom":[subQ1,subQ0]});Q110=makeQuery(id+"F2.imprint","IMPRINT",FACE,{"disambiguationData":[TD([[makeQuery(id+"F2.imprint","IMPRINT",EDGE,{"disambiguationData":[TD([[subQ2,-1.0]])],"derivedFrom":subQ1}),1.0]])]});}
            var Q111;
            {var subQ0=sQuery(id+"F2.wireOp",EDGE,"E31.11.0.0");var subQ1=sQuery(id+"F2.wireOp",EDGE,"E31.8.0.4");var subQ2=makeQuery(id+"F2.imprint","INTERSECT",VERTEX,{"derivedFrom":[subQ1,subQ0]});Q111=makeQuery(id+"F2.imprint","IMPRINT",FACE,{"disambiguationData":[TD([[makeQuery(id+"F2.imprint","IMPRINT",EDGE,{"disambiguationData":[TD([[subQ2,-1.0]])],"derivedFrom":subQ1}),1.0]])]});}
            var Q112;
            {var subQ0=sQuery(id+"F2.wireOp",EDGE,"E31.8.0.0");var subQ1=sQuery(id+"F2.wireOp",EDGE,"E31.4.0.4");var subQ2=makeQuery(id+"F2.imprint","INTERSECT",VERTEX,{"derivedFrom":[subQ1,subQ0]});Q112=makeQuery(id+"F2.imprint","IMPRINT",FACE,{"disambiguationData":[TD([[makeQuery(id+"F2.imprint","IMPRINT",EDGE,{"disambiguationData":[TD([[subQ2,-1.0]])],"derivedFrom":subQ1}),1.0]])]});}
            var Q113;
            {var subQ0=sQuery(id+"F2.wireOp",EDGE,"E31.9.0.0");var subQ1=sQuery(id+"F2.wireOp",EDGE,"E31.6.0.4");var subQ2=makeQuery(id+"F2.imprint","INTERSECT",VERTEX,{"derivedFrom":[subQ1,subQ0]});Q113=makeQuery(id+"F2.imprint","IMPRINT",FACE,{"disambiguationData":[TD([[makeQuery(id+"F2.imprint","IMPRINT",EDGE,{"disambiguationData":[TD([[subQ2,-1.0]])],"derivedFrom":subQ1}),1.0]])]});}
            var Q114;
            {var subQ0=sQuery(id+"F2.wireOp",EDGE,"E31.13.0.0");var subQ1=sQuery(id+"F2.wireOp",EDGE,"E31.10.0.4");var subQ2=makeQuery(id+"F2.imprint","INTERSECT",VERTEX,{"derivedFrom":[subQ1,subQ0]});Q114=makeQuery(id+"F2.imprint","IMPRINT",FACE,{"disambiguationData":[TD([[makeQuery(id+"F2.imprint","IMPRINT",EDGE,{"disambiguationData":[TD([[subQ2,-1.0]])],"derivedFrom":subQ1}),1.0]])]});}
            var Q115;
            {var subQ0=sQuery(id+"F2.wireOp",EDGE,"E31.7.0.0");var subQ1=sQuery(id+"F2.wireOp",EDGE,"E31.2.0.4");var subQ2=makeQuery(id+"F2.imprint","INTERSECT",VERTEX,{"derivedFrom":[subQ1,subQ0]});Q115=makeQuery(id+"F2.imprint","IMPRINT",FACE,{"disambiguationData":[TD([[makeQuery(id+"F2.imprint","IMPRINT",EDGE,{"disambiguationData":[TD([[subQ2,-1.0]])],"derivedFrom":subQ1}),1.0]])]});}
            var Q116;
            {var subQ0=sQuery(id+"F2.wireOp",EDGE,"E31.6.0.0");var subQ1=sQuery(id+"F2.wireOp",EDGE,"E31.5.0.4");var subQ2=makeQuery(id+"F2.imprint","INTERSECT",VERTEX,{"derivedFrom":[subQ1,subQ0]});Q116=makeQuery(id+"F2.imprint","IMPRINT",FACE,{"disambiguationData":[TD([[makeQuery(id+"F2.imprint","IMPRINT",EDGE,{"disambiguationData":[TD([[subQ2,-1.0]])],"derivedFrom":subQ1}),1.0]])]});}
            var Q117;
            {var subQ0=sQuery(id+"F2.wireOp",EDGE,"E31.9.0.0");var subQ1=sQuery(id+"F2.wireOp",EDGE,"E31.7.0.4");var subQ2=makeQuery(id+"F2.imprint","INTERSECT",VERTEX,{"derivedFrom":[subQ1,subQ0]});Q117=makeQuery(id+"F2.imprint","IMPRINT",FACE,{"disambiguationData":[TD([[makeQuery(id+"F2.imprint","IMPRINT",EDGE,{"disambiguationData":[TD([[subQ2,-1.0]])],"derivedFrom":subQ1}),1.0]])]});}
            var Q118;
            {var subQ0=sQuery(id+"F2.wireOp",EDGE,"E31.5.0.0");var subQ1=sQuery(id+"F2.wireOp",EDGE,"E31.3.0.4");var subQ2=makeQuery(id+"F2.imprint","INTERSECT",VERTEX,{"derivedFrom":[subQ1,subQ0]});Q118=makeQuery(id+"F2.imprint","IMPRINT",FACE,{"disambiguationData":[TD([[makeQuery(id+"F2.imprint","IMPRINT",EDGE,{"disambiguationData":[TD([[subQ2,-1.0]])],"derivedFrom":subQ1}),1.0]])]});}
            var Q119;
            {var subQ0=sQuery(id+"F2.wireOp",EDGE,"E31.6.0.0");var subQ1=sQuery(id+"F2.wireOp",EDGE,"E31.3.0.4");var subQ2=makeQuery(id+"F2.imprint","INTERSECT",VERTEX,{"derivedFrom":[subQ1,subQ0]});Q119=makeQuery(id+"F2.imprint","IMPRINT",FACE,{"disambiguationData":[TD([[makeQuery(id+"F2.imprint","IMPRINT",EDGE,{"disambiguationData":[TD([[subQ2,-1.0]])],"derivedFrom":subQ1}),1.0]])]});}
            var Q120;
            {var subQ0=sQuery(id+"F2.wireOp",EDGE,"E31.4.0.0");var subQ1=sQuery(id+"F2.wireOp",EDGE,"E31.1.0.4");var subQ2=makeQuery(id+"F2.imprint","INTERSECT",VERTEX,{"derivedFrom":[subQ1,subQ0]});Q120=makeQuery(id+"F2.imprint","IMPRINT",FACE,{"disambiguationData":[TD([[makeQuery(id+"F2.imprint","IMPRINT",EDGE,{"disambiguationData":[TD([[subQ2,-1.0]])],"derivedFrom":subQ1}),1.0]])]});}
            var Q121;
            {var subQ0=sQuery(id+"F2.wireOp",EDGE,"E31.11.0.0");var subQ1=sQuery(id+"F2.wireOp",EDGE,"E31.7.0.4");var subQ2=makeQuery(id+"F2.imprint","INTERSECT",VERTEX,{"derivedFrom":[subQ1,subQ0]});Q121=makeQuery(id+"F2.imprint","IMPRINT",FACE,{"disambiguationData":[TD([[makeQuery(id+"F2.imprint","IMPRINT",EDGE,{"disambiguationData":[TD([[subQ2,-1.0]])],"derivedFrom":subQ1}),1.0]])]});}
            var Q122;
            {var subQ0=sQuery(id+"F2.wireOp",EDGE,"E31.5.0.0");var subQ1=sQuery(id+"F2.wireOp",EDGE,"E31.1.0.4");var subQ2=makeQuery(id+"F2.imprint","INTERSECT",VERTEX,{"derivedFrom":[subQ1,subQ0]});Q122=makeQuery(id+"F2.imprint","IMPRINT",FACE,{"disambiguationData":[TD([[makeQuery(id+"F2.imprint","IMPRINT",EDGE,{"disambiguationData":[TD([[subQ2,-1.0]])],"derivedFrom":subQ1}),1.0]])]});}
            var Q123;
            {var subQ0=sQuery(id+"F2.wireOp",EDGE,"E31.3.0.0");var subQ1=sQuery(id+"F2.wireOp",EDGE,"E30.1");var subQ2=makeQuery(id+"F2.imprint","INTERSECT",VERTEX,{"derivedFrom":[subQ1,subQ0]});Q123=makeQuery(id+"F2.imprint","IMPRINT",FACE,{"disambiguationData":[TD([[makeQuery(id+"F2.imprint","IMPRINT",EDGE,{"disambiguationData":[TD([[subQ2,-1.0]])],"derivedFrom":subQ1}),1.0]])]});}
            var Q124;
            {var subQ0=sQuery(id+"F2.wireOp",EDGE,"E31.13.0.0");var subQ1=sQuery(id+"F2.wireOp",EDGE,"E31.9.0.4");var subQ2=makeQuery(id+"F2.imprint","INTERSECT",VERTEX,{"derivedFrom":[subQ1,subQ0]});Q124=makeQuery(id+"F2.imprint","IMPRINT",FACE,{"disambiguationData":[TD([[makeQuery(id+"F2.imprint","IMPRINT",EDGE,{"disambiguationData":[TD([[subQ2,-1.0]])],"derivedFrom":subQ1}),1.0]])]});}
            var Q125;
            {var subQ0=sQuery(id+"F2.wireOp",EDGE,"E31.4.0.0");var subQ1=sQuery(id+"F2.wireOp",EDGE,"E31.3.0.4");var subQ2=makeQuery(id+"F2.imprint","INTERSECT",VERTEX,{"derivedFrom":[subQ1,subQ0]});Q125=makeQuery(id+"F2.imprint","IMPRINT",FACE,{"disambiguationData":[TD([[makeQuery(id+"F2.imprint","IMPRINT",EDGE,{"disambiguationData":[TD([[subQ2,-1.0]])],"derivedFrom":subQ1}),1.0]])]});}
            var Q126;
            {var subQ0=sQuery(id+"F2.wireOp",EDGE,"E31.2.0.0");var subQ1=sQuery(id+"F2.wireOp",EDGE,"E31.1.0.4");var subQ2=makeQuery(id+"F2.imprint","INTERSECT",VERTEX,{"derivedFrom":[subQ1,subQ0]});Q126=makeQuery(id+"F2.imprint","IMPRINT",FACE,{"disambiguationData":[TD([[makeQuery(id+"F2.imprint","IMPRINT",EDGE,{"disambiguationData":[TD([[subQ2,-1.0]])],"derivedFrom":subQ1}),1.0]])]});}
            var Q127;
            {var subQ0=sQuery(id+"F2.wireOp",EDGE,"E31.13.0.0");var subQ1=sQuery(id+"F2.wireOp",EDGE,"E31.11.0.4");var subQ2=makeQuery(id+"F2.imprint","INTERSECT",VERTEX,{"derivedFrom":[subQ1,subQ0]});Q127=makeQuery(id+"F2.imprint","IMPRINT",FACE,{"disambiguationData":[TD([[makeQuery(id+"F2.imprint","IMPRINT",EDGE,{"disambiguationData":[TD([[subQ2,-1.0]])],"derivedFrom":subQ1}),1.0]])]});}
            var Q128;
            {var subQ0=sQuery(id+"F2.wireOp",EDGE,"E31.12.0.0");var subQ1=sQuery(id+"F2.wireOp",EDGE,"E31.11.0.4");var subQ2=makeQuery(id+"F2.imprint","INTERSECT",VERTEX,{"derivedFrom":[subQ1,subQ0]});Q128=makeQuery(id+"F2.imprint","IMPRINT",FACE,{"disambiguationData":[TD([[makeQuery(id+"F2.imprint","IMPRINT",EDGE,{"disambiguationData":[TD([[subQ2,-1.0]])],"derivedFrom":subQ1}),1.0]])]});}
            var Q129;
            {var subQ0=sQuery(id+"F2.wireOp",EDGE,"E31.10.0.0");var subQ1=sQuery(id+"F2.wireOp",EDGE,"E31.7.0.4");var subQ2=makeQuery(id+"F2.imprint","INTERSECT",VERTEX,{"derivedFrom":[subQ1,subQ0]});Q129=makeQuery(id+"F2.imprint","IMPRINT",FACE,{"disambiguationData":[TD([[makeQuery(id+"F2.imprint","IMPRINT",EDGE,{"disambiguationData":[TD([[subQ2,-1.0]])],"derivedFrom":subQ1}),1.0]])]});}
            var Q130;
            {var subQ0=sQuery(id+"F2.wireOp",EDGE,"E31.8.0.0");var subQ1=sQuery(id+"F2.wireOp",EDGE,"E31.5.0.4");var subQ2=makeQuery(id+"F2.imprint","INTERSECT",VERTEX,{"derivedFrom":[subQ1,subQ0]});Q130=makeQuery(id+"F2.imprint","IMPRINT",FACE,{"disambiguationData":[TD([[makeQuery(id+"F2.imprint","IMPRINT",EDGE,{"disambiguationData":[TD([[subQ2,-1.0]])],"derivedFrom":subQ1}),1.0]])]});}
            var Q131;
            {var subQ0=sQuery(id+"F2.wireOp",EDGE,"E31.11.0.0");var subQ1=sQuery(id+"F2.wireOp",EDGE,"E31.9.0.4");var subQ2=makeQuery(id+"F2.imprint","INTERSECT",VERTEX,{"derivedFrom":[subQ1,subQ0]});Q131=makeQuery(id+"F2.imprint","IMPRINT",FACE,{"disambiguationData":[TD([[makeQuery(id+"F2.imprint","IMPRINT",EDGE,{"disambiguationData":[TD([[subQ2,-1.0]])],"derivedFrom":subQ1}),1.0]])]});}
            var Q132;
            {var subQ0=sQuery(id+"F2.wireOp",EDGE,"E31.9.0.0");var subQ1=sQuery(id+"F2.wireOp",EDGE,"E31.5.0.4");var subQ2=makeQuery(id+"F2.imprint","INTERSECT",VERTEX,{"derivedFrom":[subQ1,subQ0]});Q132=makeQuery(id+"F2.imprint","IMPRINT",FACE,{"disambiguationData":[TD([[makeQuery(id+"F2.imprint","IMPRINT",EDGE,{"disambiguationData":[TD([[subQ2,-1.0]])],"derivedFrom":subQ1}),1.0]])]});}
            var Q133;
            {var subQ0=sQuery(id+"F2.wireOp",EDGE,"E31.7.0.0");var subQ1=sQuery(id+"F2.wireOp",EDGE,"E31.3.0.4");var subQ2=makeQuery(id+"F2.imprint","INTERSECT",VERTEX,{"derivedFrom":[subQ1,subQ0]});Q133=makeQuery(id+"F2.imprint","IMPRINT",FACE,{"disambiguationData":[TD([[makeQuery(id+"F2.imprint","IMPRINT",EDGE,{"disambiguationData":[TD([[subQ2,-1.0]])],"derivedFrom":subQ1}),1.0]])]});}
            var Q134;
            {var subQ0=sQuery(id+"F2.wireOp",EDGE,"E31.6.0.0");var subQ1=sQuery(id+"F2.wireOp",EDGE,"E31.1.0.4");var subQ2=makeQuery(id+"F2.imprint","INTERSECT",VERTEX,{"derivedFrom":[subQ1,subQ0]});Q134=makeQuery(id+"F2.imprint","IMPRINT",FACE,{"disambiguationData":[TD([[makeQuery(id+"F2.imprint","IMPRINT",EDGE,{"disambiguationData":[TD([[subQ2,-1.0]])],"derivedFrom":subQ1}),1.0]])]});}
            var Q135;
            {var subQ0=sQuery(id+"F2.wireOp",EDGE,"E31.3.0.0");var subQ1=sQuery(id+"F2.wireOp",EDGE,"E31.2.0.4");var subQ2=makeQuery(id+"F2.imprint","INTERSECT",VERTEX,{"derivedFrom":[subQ1,subQ0]});Q135=makeQuery(id+"F2.imprint","IMPRINT",FACE,{"disambiguationData":[TD([[makeQuery(id+"F2.imprint","IMPRINT",EDGE,{"disambiguationData":[TD([[subQ2,-1.0]])],"derivedFrom":subQ1}),1.0]])]});}
            var Q136;
            {var subQ0=sQuery(id+"F2.wireOp",EDGE,"E31.13.0.0");var subQ1=sQuery(id+"F2.wireOp",EDGE,"E31.12.0.4");var subQ2=makeQuery(id+"F2.imprint","INTERSECT",VERTEX,{"derivedFrom":[subQ1,subQ0]});Q136=makeQuery(id+"F2.imprint","IMPRINT",FACE,{"disambiguationData":[TD([[makeQuery(id+"F2.imprint","IMPRINT",EDGE,{"disambiguationData":[TD([[subQ2,-1.0]])],"derivedFrom":subQ1}),1.0]])]});}
            var Q137;
            {var subQ0=sQuery(id+"F2.wireOp",EDGE,"E31.12.0.0");var subQ1=sQuery(id+"F2.wireOp",EDGE,"E31.9.0.4");var subQ2=makeQuery(id+"F2.imprint","INTERSECT",VERTEX,{"derivedFrom":[subQ1,subQ0]});Q137=makeQuery(id+"F2.imprint","IMPRINT",FACE,{"disambiguationData":[TD([[makeQuery(id+"F2.imprint","IMPRINT",EDGE,{"disambiguationData":[TD([[subQ2,-1.0]])],"derivedFrom":subQ1}),1.0]])]});}
            var Q138;
            {var subQ0=sQuery(id+"F2.wireOp",EDGE,"E31.8.0.0");var subQ1=sQuery(id+"F2.wireOp",EDGE,"E31.3.0.4");var subQ2=makeQuery(id+"F2.imprint","INTERSECT",VERTEX,{"derivedFrom":[subQ1,subQ0]});Q138=makeQuery(id+"F2.imprint","IMPRINT",FACE,{"disambiguationData":[TD([[makeQuery(id+"F2.imprint","IMPRINT",EDGE,{"disambiguationData":[TD([[subQ2,-1.0]])],"derivedFrom":subQ1}),1.0]])]});}
            var Q139;
            {var subQ0=sQuery(id+"F2.wireOp",EDGE,"E75.MirrorCS");var subQ1=sQuery(id+"F2.wireOp",EDGE,"E70.MirrorCS");var subQ2=makeQuery(id+"F2.imprint","INTERSECT",VERTEX,{"derivedFrom":[subQ1,subQ0]});Q139=makeQuery(id+"F2.imprint","IMPRINT",FACE,{"disambiguationData":[TD([[makeQuery(id+"F2.imprint","IMPRINT",EDGE,{"disambiguationData":[TD([[subQ2,-1.0]])],"derivedFrom":subQ1}),1.0]])]});}
            var Q140;
            {var subQ0=sQuery(id+"F2.wireOp",EDGE,"E69.MirrorCS");var subQ1=sQuery(id+"F2.wireOp",EDGE,"E67.MirrorCS");var subQ2=makeQuery(id+"F2.imprint","INTERSECT",VERTEX,{"derivedFrom":[subQ1,subQ0]});Q140=makeQuery(id+"F2.imprint","IMPRINT",FACE,{"disambiguationData":[TD([[makeQuery(id+"F2.imprint","IMPRINT",EDGE,{"disambiguationData":[TD([[subQ2,-1.0]])],"derivedFrom":subQ1}),-1.0]])]});}
            var Q141;
            {var subQ0=sQuery(id+"F2.wireOp",EDGE,"E61.MirrorCS");var subQ1=sQuery(id+"F2.wireOp",EDGE,"E60.MirrorCS");var subQ2=makeQuery(id+"F2.imprint","INTERSECT",VERTEX,{"derivedFrom":[subQ1,subQ0]});Q141=makeQuery(id+"F2.imprint","IMPRINT",FACE,{"disambiguationData":[TD([[makeQuery(id+"F2.imprint","IMPRINT",EDGE,{"disambiguationData":[TD([[subQ2,-1.0]])],"derivedFrom":subQ1}),-1.0]])]});}
            var Q142;
            {var subQ0=sQuery(id+"F2.wireOp",EDGE,"E74.MirrorCS");var subQ1=sQuery(id+"F2.wireOp",EDGE,"E69.MirrorCS");var subQ2=makeQuery(id+"F2.imprint","INTERSECT",VERTEX,{"derivedFrom":[subQ1,subQ0]});Q142=makeQuery(id+"F2.imprint","IMPRINT",FACE,{"disambiguationData":[TD([[makeQuery(id+"F2.imprint","IMPRINT",EDGE,{"disambiguationData":[TD([[subQ2,-1.0]])],"derivedFrom":subQ1}),1.0]])]});}
            var Q143;
            {var subQ0=sQuery(id+"F2.wireOp",EDGE,"E63.MirrorCS");var subQ1=sQuery(id+"F2.wireOp",EDGE,"E46.MirrorCS");var subQ2=makeQuery(id+"F2.imprint","INTERSECT",VERTEX,{"derivedFrom":[subQ1,subQ0]});Q143=makeQuery(id+"F2.imprint","IMPRINT",FACE,{"disambiguationData":[TD([[makeQuery(id+"F2.imprint","IMPRINT",EDGE,{"disambiguationData":[TD([[subQ2,-1.0]])],"derivedFrom":subQ1}),1.0]])]});}
            var Q144;
            {var subQ0=sQuery(id+"F2.wireOp",EDGE,"E70.MirrorCS");var subQ1=sQuery(id+"F2.wireOp",EDGE,"E51.MirrorCS");var subQ2=makeQuery(id+"F2.imprint","INTERSECT",VERTEX,{"derivedFrom":[subQ1,subQ0]});Q144=makeQuery(id+"F2.imprint","IMPRINT",FACE,{"disambiguationData":[TD([[makeQuery(id+"F2.imprint","IMPRINT",EDGE,{"disambiguationData":[TD([[subQ2,1.0]])],"derivedFrom":subQ1}),1.0]])]});}
            var Q145;
            {var subQ0=sQuery(id+"F2.wireOp",EDGE,"E101.MirrorCS");var subQ1=sQuery(id+"F2.wireOp",EDGE,"E51.MirrorCS");var subQ2=makeQuery(id+"F2.imprint","INTERSECT",VERTEX,{"derivedFrom":[subQ1,subQ0]});Q145=makeQuery(id+"F2.imprint","IMPRINT",FACE,{"disambiguationData":[TD([[makeQuery(id+"F2.imprint","IMPRINT",EDGE,{"disambiguationData":[TD([[subQ2,1.0]])],"derivedFrom":subQ1}),-1.0]])]});}
            var Q146;
            {var subQ0=sQuery(id+"F2.wireOp",EDGE,"E88.MirrorCS");var subQ1=sQuery(id+"F2.wireOp",EDGE,"E70.MirrorCS");var subQ2=makeQuery(id+"F2.imprint","INTERSECT",VERTEX,{"derivedFrom":[subQ1,subQ0]});Q146=makeQuery(id+"F2.imprint","IMPRINT",FACE,{"disambiguationData":[TD([[makeQuery(id+"F2.imprint","IMPRINT",EDGE,{"disambiguationData":[TD([[subQ2,-1.0]])],"derivedFrom":subQ1}),-1.0]])]});}
            var Q147;
            {var subQ0=sQuery(id+"F2.wireOp",EDGE,"E100.MirrorCS");var subQ1=sQuery(id+"F2.wireOp",EDGE,"E50.MirrorCS");var subQ2=makeQuery(id+"F2.imprint","INTERSECT",VERTEX,{"derivedFrom":[subQ1,subQ0]});Q147=makeQuery(id+"F2.imprint","IMPRINT",FACE,{"disambiguationData":[TD([[makeQuery(id+"F2.imprint","IMPRINT",EDGE,{"disambiguationData":[TD([[subQ2,1.0]])],"derivedFrom":subQ1}),1.0]])]});}
            var Q148;
            {var subQ4=sQuery(id+"F2.wireOp",EDGE,"E38.MirrorCS");Q148=makeQuery(id+"F2.imprint","IMPRINT",FACE,{"disambiguationData":[TD([[makeQuery(id+"F2.imprint","IMPRINT",EDGE,{"derivedFrom":subQ4}),1.0]])]});}
            var Q149;
            {var subQ0=sQuery(id+"F2.wireOp",EDGE,"E65.MirrorCS");Q149=makeQuery(id+"F2.imprint","IMPRINT",FACE,{"disambiguationData":[TD([[makeQuery(id+"F2.imprint","IMPRINT",EDGE,{"derivedFrom":subQ0}),1.0]])]});}
            var Q150;
            {var subQ0=sQuery(id+"F2.wireOp",EDGE,"E67.MirrorCS");var subQ1=sQuery(id+"F2.wireOp",EDGE,"E54.MirrorCS");var subQ2=makeQuery(id+"F2.imprint","INTERSECT",VERTEX,{"derivedFrom":[subQ1,subQ0]});Q150=makeQuery(id+"F2.imprint","IMPRINT",FACE,{"disambiguationData":[TD([[makeQuery(id+"F2.imprint","IMPRINT",EDGE,{"disambiguationData":[TD([[subQ2,-1.0]])],"derivedFrom":subQ1}),1.0]])]});}
            var Q151;
            {var subQ0=sQuery(id+"F2.wireOp",EDGE,"E94.MirrorCS");var subQ1=sQuery(id+"F2.wireOp",EDGE,"E67.MirrorCS");var subQ2=makeQuery(id+"F2.imprint","INTERSECT",VERTEX,{"derivedFrom":[subQ1,subQ0]});Q151=makeQuery(id+"F2.imprint","IMPRINT",FACE,{"disambiguationData":[TD([[makeQuery(id+"F2.imprint","IMPRINT",EDGE,{"disambiguationData":[TD([[subQ2,1.0]])],"derivedFrom":subQ1}),-1.0]])]});}
            var Q152;
            {var subQ0=sQuery(id+"F2.wireOp",EDGE,"E101.MirrorCS");var subQ1=sQuery(id+"F2.wireOp",EDGE,"E51.MirrorCS");var subQ2=makeQuery(id+"F2.imprint","INTERSECT",VERTEX,{"derivedFrom":[subQ1,subQ0]});Q152=makeQuery(id+"F2.imprint","IMPRINT",FACE,{"disambiguationData":[TD([[makeQuery(id+"F2.imprint","IMPRINT",EDGE,{"disambiguationData":[TD([[subQ2,1.0]])],"derivedFrom":subQ1}),1.0]])]});}
            var Q153;
            {var subQ0=sQuery(id+"F2.wireOp",EDGE,"E60.MirrorCS");var subQ1=sQuery(id+"F2.wireOp",EDGE,"E46.MirrorCS");var subQ2=makeQuery(id+"F2.imprint","INTERSECT",VERTEX,{"derivedFrom":[subQ1,subQ0]});Q153=makeQuery(id+"F2.imprint","IMPRINT",FACE,{"disambiguationData":[TD([[makeQuery(id+"F2.imprint","IMPRINT",EDGE,{"disambiguationData":[TD([[subQ2,-1.0]])],"derivedFrom":subQ1}),1.0]])]});}
            var Q154;
            {var subQ0=sQuery(id+"F2.wireOp",EDGE,"E61.MirrorCS");var subQ1=sQuery(id+"F2.wireOp",EDGE,"E54.MirrorCS");var subQ2=makeQuery(id+"F2.imprint","INTERSECT",VERTEX,{"derivedFrom":[subQ1,subQ0]});Q154=makeQuery(id+"F2.imprint","IMPRINT",FACE,{"disambiguationData":[TD([[makeQuery(id+"F2.imprint","IMPRINT",EDGE,{"disambiguationData":[TD([[subQ2,-1.0]])],"derivedFrom":subQ1}),-1.0]])]});}
            var Q155;
            {var subQ0=sQuery(id+"F2.wireOp",EDGE,"E58.MirrorCS");var subQ1=sQuery(id+"F2.wireOp",EDGE,"E54.MirrorCS");var subQ2=makeQuery(id+"F2.imprint","INTERSECT",VERTEX,{"derivedFrom":[subQ1,subQ0]});Q155=makeQuery(id+"F2.imprint","IMPRINT",FACE,{"disambiguationData":[TD([[makeQuery(id+"F2.imprint","IMPRINT",EDGE,{"disambiguationData":[TD([[subQ2,-1.0]])],"derivedFrom":subQ1}),-1.0]])]});}
            var Q156;
            {var subQ0=sQuery(id+"F2.wireOp",EDGE,"E100.MirrorCS");var subQ1=sQuery(id+"F2.wireOp",EDGE,"E67.MirrorCS");var subQ2=makeQuery(id+"F2.imprint","INTERSECT",VERTEX,{"derivedFrom":[subQ1,subQ0]});Q156=makeQuery(id+"F2.imprint","IMPRINT",FACE,{"disambiguationData":[TD([[makeQuery(id+"F2.imprint","IMPRINT",EDGE,{"disambiguationData":[TD([[subQ2,-1.0]])],"derivedFrom":subQ1}),-1.0]])]});}
            var Q157;
            {var subQ0=sQuery(id+"F2.wireOp",EDGE,"E81.MirrorCS");var subQ1=sQuery(id+"F2.wireOp",EDGE,"E51.MirrorCS");var subQ2=makeQuery(id+"F2.imprint","INTERSECT",VERTEX,{"derivedFrom":[subQ1,subQ0]});Q157=makeQuery(id+"F2.imprint","IMPRINT",FACE,{"disambiguationData":[TD([[makeQuery(id+"F2.imprint","IMPRINT",EDGE,{"disambiguationData":[TD([[subQ2,-1.0]])],"derivedFrom":subQ1}),-1.0]])]});}
            var Q158;
            {var subQ0=sQuery(id+"F2.wireOp",EDGE,"E54.MirrorCS");var subQ1=sQuery(id+"F2.wireOp",EDGE,"E46.MirrorCS");var subQ2=makeQuery(id+"F2.imprint","INTERSECT",VERTEX,{"derivedFrom":[subQ1,subQ0]});Q158=makeQuery(id+"F2.imprint","IMPRINT",FACE,{"disambiguationData":[TD([[makeQuery(id+"F2.imprint","IMPRINT",EDGE,{"disambiguationData":[TD([[subQ2,-1.0]])],"derivedFrom":subQ1}),1.0]])]});}
            var Q159;
            {var subQ0=sQuery(id+"F2.wireOp",EDGE,"E75.MirrorCS");var subQ1=sQuery(id+"F2.wireOp",EDGE,"E37.MirrorCS");var subQ2=makeQuery(id+"F2.imprint","INTERSECT",VERTEX,{"derivedFrom":[subQ1,subQ0]});Q159=makeQuery(id+"F2.imprint","IMPRINT",FACE,{"disambiguationData":[TD([[makeQuery(id+"F2.imprint","IMPRINT",EDGE,{"disambiguationData":[TD([[subQ2,1.0]])],"derivedFrom":subQ1}),1.0]])]});}
            var Q160;
            {var subQ0=sQuery(id+"F2.wireOp",EDGE,"E74.MirrorCS");var subQ1=sQuery(id+"F2.wireOp",EDGE,"E69.MirrorCS");var subQ2=makeQuery(id+"F2.imprint","INTERSECT",VERTEX,{"derivedFrom":[subQ1,subQ0]});Q160=makeQuery(id+"F2.imprint","IMPRINT",FACE,{"disambiguationData":[TD([[makeQuery(id+"F2.imprint","IMPRINT",EDGE,{"disambiguationData":[TD([[subQ2,-1.0]])],"derivedFrom":subQ1}),-1.0]])]});}
            var Q161;
            {var subQ0=sQuery(id+"F2.wireOp",EDGE,"E94.MirrorCS");var subQ1=sQuery(id+"F2.wireOp",EDGE,"E46.MirrorCS");var subQ2=makeQuery(id+"F2.imprint","INTERSECT",VERTEX,{"derivedFrom":[subQ1,subQ0]});Q161=makeQuery(id+"F2.imprint","IMPRINT",FACE,{"disambiguationData":[TD([[makeQuery(id+"F2.imprint","IMPRINT",EDGE,{"disambiguationData":[TD([[subQ2,-1.0]])],"derivedFrom":subQ1}),1.0]])]});}
            var Q162;
            {var subQ0=sQuery(id+"F2.wireOp",EDGE,"E82.MirrorCS");var subQ1=sQuery(id+"F2.wireOp",EDGE,"E46.MirrorCS");var subQ2=makeQuery(id+"F2.imprint","INTERSECT",VERTEX,{"derivedFrom":[subQ1,subQ0]});Q162=makeQuery(id+"F2.imprint","IMPRINT",FACE,{"disambiguationData":[TD([[makeQuery(id+"F2.imprint","IMPRINT",EDGE,{"disambiguationData":[TD([[subQ2,-1.0]])],"derivedFrom":subQ1}),1.0]])]});}
            var Q163;
            {var subQ1=sQuery(id+"F2.wireOp",EDGE,"E39.MirrorCS");var subQ5=sQuery(id+"F2.wireOp",EDGE,"E86.MirrorCS");var subQ6=makeQuery(id+"F2.imprint","INTERSECT",VERTEX,{"derivedFrom":[subQ1,subQ5]});Q163=makeQuery(id+"F2.imprint","IMPRINT",FACE,{"disambiguationData":[TD([[makeQuery(id+"F2.imprint","IMPRINT",EDGE,{"disambiguationData":[TD([[subQ6,1.0]])],"derivedFrom":subQ1}),1.0]])]});}
            var Q164;
            {var subQ3=sQuery(id+"F2.wireOp",EDGE,"E69.MirrorCS");var subQ10=sQuery(id+"F2.wireOp",EDGE,"E34.MirrorCS");var subQ11=makeQuery(id+"F2.imprint","INTERSECT",VERTEX,{"derivedFrom":[subQ10,subQ3]});Q164=makeQuery(id+"F2.imprint","IMPRINT",FACE,{"disambiguationData":[TD([[makeQuery(id+"F2.imprint","IMPRINT",EDGE,{"disambiguationData":[TD([[subQ11,-1.0]])],"derivedFrom":subQ10}),1.0]])]});}
            var Q165;
            {var subQ0=sQuery(id+"F2.wireOp",EDGE,"E88.MirrorCS");var subQ1=sQuery(id+"F2.wireOp",EDGE,"E83.MirrorCS");var subQ2=makeQuery(id+"F2.imprint","INTERSECT",VERTEX,{"derivedFrom":[subQ1,subQ0]});Q165=makeQuery(id+"F2.imprint","IMPRINT",FACE,{"disambiguationData":[TD([[makeQuery(id+"F2.imprint","IMPRINT",EDGE,{"disambiguationData":[TD([[subQ2,-1.0]])],"derivedFrom":subQ1}),-1.0]])]});}
            var Q166;
            {var subQ0=sQuery(id+"F2.wireOp",EDGE,"E95.MirrorCS");var subQ1=sQuery(id+"F2.wireOp",EDGE,"E74.MirrorCS");var subQ2=makeQuery(id+"F2.imprint","INTERSECT",VERTEX,{"derivedFrom":[subQ1,subQ0]});Q166=makeQuery(id+"F2.imprint","IMPRINT",FACE,{"disambiguationData":[TD([[makeQuery(id+"F2.imprint","IMPRINT",EDGE,{"disambiguationData":[TD([[subQ2,-1.0]])],"derivedFrom":subQ1}),1.0]])]});}
            var Q167;
            {var subQ0=sQuery(id+"F2.wireOp",EDGE,"E88.MirrorCS");var subQ1=sQuery(id+"F2.wireOp",EDGE,"E81.MirrorCS");var subQ2=makeQuery(id+"F2.imprint","INTERSECT",VERTEX,{"derivedFrom":[subQ1,subQ0]});Q167=makeQuery(id+"F2.imprint","IMPRINT",FACE,{"disambiguationData":[TD([[makeQuery(id+"F2.imprint","IMPRINT",EDGE,{"disambiguationData":[TD([[subQ2,-1.0]])],"derivedFrom":subQ1}),-1.0]])]});}
            var Q168;
            {var subQ0=sQuery(id+"F2.wireOp",EDGE,"E82.MirrorCS");var subQ1=sQuery(id+"F2.wireOp",EDGE,"E58.MirrorCS");var subQ2=makeQuery(id+"F2.imprint","INTERSECT",VERTEX,{"derivedFrom":[subQ1,subQ0]});Q168=makeQuery(id+"F2.imprint","IMPRINT",FACE,{"disambiguationData":[TD([[makeQuery(id+"F2.imprint","IMPRINT",EDGE,{"disambiguationData":[TD([[subQ2,-1.0]])],"derivedFrom":subQ1}),-1.0]])]});}
            var Q169;
            {var subQ0=sQuery(id+"F2.wireOp",EDGE,"E83.MirrorCS");var subQ1=sQuery(id+"F2.wireOp",EDGE,"E50.MirrorCS");var subQ2=makeQuery(id+"F2.imprint","INTERSECT",VERTEX,{"derivedFrom":[subQ1,subQ0]});Q169=makeQuery(id+"F2.imprint","IMPRINT",FACE,{"disambiguationData":[TD([[makeQuery(id+"F2.imprint","IMPRINT",EDGE,{"disambiguationData":[TD([[subQ2,-1.0]])],"derivedFrom":subQ1}),1.0]])]});}
            var Q170;
            {var subQ0=sQuery(id+"F2.wireOp",EDGE,"E100.MirrorCS");var subQ1=sQuery(id+"F2.wireOp",EDGE,"E50.MirrorCS");var subQ2=makeQuery(id+"F2.imprint","INTERSECT",VERTEX,{"derivedFrom":[subQ1,subQ0]});Q170=makeQuery(id+"F2.imprint","IMPRINT",FACE,{"disambiguationData":[TD([[makeQuery(id+"F2.imprint","IMPRINT",EDGE,{"disambiguationData":[TD([[subQ2,1.0]])],"derivedFrom":subQ1}),-1.0]])]});}
            var Q171;
            {var subQ0=sQuery(id+"F2.wireOp",EDGE,"E83.MirrorCS");var subQ1=sQuery(id+"F2.wireOp",EDGE,"E50.MirrorCS");var subQ2=makeQuery(id+"F2.imprint","INTERSECT",VERTEX,{"derivedFrom":[subQ1,subQ0]});Q171=makeQuery(id+"F2.imprint","IMPRINT",FACE,{"disambiguationData":[TD([[makeQuery(id+"F2.imprint","IMPRINT",EDGE,{"disambiguationData":[TD([[subQ2,-1.0]])],"derivedFrom":subQ1}),-1.0]])]});}
            var Q172;
            {var subQ0=sQuery(id+"F2.wireOp",EDGE,"E69.MirrorCS");var subQ1=sQuery(id+"F2.wireOp",EDGE,"E50.MirrorCS");var subQ2=makeQuery(id+"F2.imprint","INTERSECT",VERTEX,{"derivedFrom":[subQ1,subQ0]});Q172=makeQuery(id+"F2.imprint","IMPRINT",FACE,{"disambiguationData":[TD([[makeQuery(id+"F2.imprint","IMPRINT",EDGE,{"disambiguationData":[TD([[subQ2,1.0]])],"derivedFrom":subQ1}),1.0]])]});}
            var Q173;
            {var subQ0=sQuery(id+"F2.wireOp",EDGE,"E58.MirrorCS");var subQ1=sQuery(id+"F2.wireOp",EDGE,"E54.MirrorCS");var subQ2=makeQuery(id+"F2.imprint","INTERSECT",VERTEX,{"derivedFrom":[subQ1,subQ0]});Q173=makeQuery(id+"F2.imprint","IMPRINT",FACE,{"disambiguationData":[TD([[makeQuery(id+"F2.imprint","IMPRINT",EDGE,{"disambiguationData":[TD([[subQ2,-1.0]])],"derivedFrom":subQ1}),1.0]])]});}
            var Q174;
            {var subQ0=sQuery(id+"F2.wireOp",EDGE,"E95.MirrorCS");var subQ1=sQuery(id+"F2.wireOp",EDGE,"E67.MirrorCS");var subQ2=makeQuery(id+"F2.imprint","INTERSECT",VERTEX,{"derivedFrom":[subQ1,subQ0]});Q174=makeQuery(id+"F2.imprint","IMPRINT",FACE,{"disambiguationData":[TD([[makeQuery(id+"F2.imprint","IMPRINT",EDGE,{"disambiguationData":[TD([[subQ2,-1.0]])],"derivedFrom":subQ1}),-1.0]])]});}
            var Q175;
            {var subQ0=sQuery(id+"F2.wireOp",EDGE,"E81.MirrorCS");var subQ1=sQuery(id+"F2.wireOp",EDGE,"E51.MirrorCS");var subQ2=makeQuery(id+"F2.imprint","INTERSECT",VERTEX,{"derivedFrom":[subQ1,subQ0]});Q175=makeQuery(id+"F2.imprint","IMPRINT",FACE,{"disambiguationData":[TD([[makeQuery(id+"F2.imprint","IMPRINT",EDGE,{"disambiguationData":[TD([[subQ2,-1.0]])],"derivedFrom":subQ1}),1.0]])]});}
            var Q176;
            {var subQ0=sQuery(id+"F2.wireOp",EDGE,"E61.MirrorCS");var subQ1=sQuery(id+"F2.wireOp",EDGE,"E54.MirrorCS");var subQ2=makeQuery(id+"F2.imprint","INTERSECT",VERTEX,{"derivedFrom":[subQ1,subQ0]});Q176=makeQuery(id+"F2.imprint","IMPRINT",FACE,{"disambiguationData":[TD([[makeQuery(id+"F2.imprint","IMPRINT",EDGE,{"disambiguationData":[TD([[subQ2,-1.0]])],"derivedFrom":subQ1}),1.0]])]});}
            var Q177;
            {var subQ0=sQuery(id+"F2.wireOp",EDGE,"E95.MirrorCS");var subQ1=sQuery(id+"F2.wireOp",EDGE,"E58.MirrorCS");var subQ2=makeQuery(id+"F2.imprint","INTERSECT",VERTEX,{"derivedFrom":[subQ1,subQ0]});Q177=makeQuery(id+"F2.imprint","IMPRINT",FACE,{"disambiguationData":[TD([[makeQuery(id+"F2.imprint","IMPRINT",EDGE,{"disambiguationData":[TD([[subQ2,-1.0]])],"derivedFrom":subQ1}),-1.0]])]});}
            var Q178;
            {var subQ6=sQuery(id+"F2.wireOp",EDGE,"E75.MirrorCS");var subQ7=sQuery(id+"F2.wireOp",EDGE,"E37.MirrorCS");var subQ8=makeQuery(id+"F2.imprint","INTERSECT",VERTEX,{"derivedFrom":[subQ7,subQ6]});Q178=makeQuery(id+"F2.imprint","IMPRINT",FACE,{"disambiguationData":[TD([[makeQuery(id+"F2.imprint","IMPRINT",EDGE,{"disambiguationData":[TD([[subQ8,1.0]])],"derivedFrom":subQ7}),-1.0]])]});}
            var Q179;
            {var subQ3=sQuery(id+"F2.wireOp",EDGE,"E100.MirrorCS");var subQ10=sQuery(id+"F2.wireOp",EDGE,"E33.MirrorCS");var subQ11=makeQuery(id+"F2.imprint","INTERSECT",VERTEX,{"derivedFrom":[subQ10,subQ3]});Q179=makeQuery(id+"F2.imprint","IMPRINT",FACE,{"disambiguationData":[TD([[makeQuery(id+"F2.imprint","IMPRINT",EDGE,{"disambiguationData":[TD([[subQ11,-1.0]])],"derivedFrom":subQ10}),1.0]])]});}
            var Q180;
            {var subQ0=sQuery(id+"F2.wireOp",EDGE,"E88.MirrorCS");var subQ1=sQuery(id+"F2.wireOp",EDGE,"E70.MirrorCS");var subQ2=makeQuery(id+"F2.imprint","INTERSECT",VERTEX,{"derivedFrom":[subQ1,subQ0]});Q180=makeQuery(id+"F2.imprint","IMPRINT",FACE,{"disambiguationData":[TD([[makeQuery(id+"F2.imprint","IMPRINT",EDGE,{"disambiguationData":[TD([[subQ2,-1.0]])],"derivedFrom":subQ1}),1.0]])]});}
            var Q181;
            {var subQ0=sQuery(id+"F2.wireOp",EDGE,"E75.MirrorCS");var subQ1=sQuery(id+"F2.wireOp",EDGE,"E70.MirrorCS");var subQ2=makeQuery(id+"F2.imprint","INTERSECT",VERTEX,{"derivedFrom":[subQ1,subQ0]});Q181=makeQuery(id+"F2.imprint","IMPRINT",FACE,{"disambiguationData":[TD([[makeQuery(id+"F2.imprint","IMPRINT",EDGE,{"disambiguationData":[TD([[subQ2,-1.0]])],"derivedFrom":subQ1}),-1.0]])]});}
            var Q182;
            {var subQ0=sQuery(id+"F2.wireOp",EDGE,"E100.MirrorCS");var subQ1=sQuery(id+"F2.wireOp",EDGE,"E58.MirrorCS");var subQ2=makeQuery(id+"F2.imprint","INTERSECT",VERTEX,{"derivedFrom":[subQ1,subQ0]});Q182=makeQuery(id+"F2.imprint","IMPRINT",FACE,{"disambiguationData":[TD([[makeQuery(id+"F2.imprint","IMPRINT",EDGE,{"disambiguationData":[TD([[subQ2,-1.0]])],"derivedFrom":subQ1}),1.0]])]});}
            var Q183;
            {var subQ0=sQuery(id+"F2.wireOp",EDGE,"E74.MirrorCS");var subQ1=sQuery(id+"F2.wireOp",EDGE,"E70.MirrorCS");var subQ2=makeQuery(id+"F2.imprint","INTERSECT",VERTEX,{"derivedFrom":[subQ1,subQ0]});Q183=makeQuery(id+"F2.imprint","IMPRINT",FACE,{"disambiguationData":[TD([[makeQuery(id+"F2.imprint","IMPRINT",EDGE,{"disambiguationData":[TD([[subQ2,-1.0]])],"derivedFrom":subQ1}),-1.0]])]});}
            var Q184;
            {var subQ0=sQuery(id+"F2.wireOp",EDGE,"E86.MirrorCS");var subQ1=sQuery(id+"F2.wireOp",EDGE,"E81.MirrorCS");var subQ2=makeQuery(id+"F2.imprint","INTERSECT",VERTEX,{"derivedFrom":[subQ1,subQ0]});Q184=makeQuery(id+"F2.imprint","IMPRINT",FACE,{"disambiguationData":[TD([[makeQuery(id+"F2.imprint","IMPRINT",EDGE,{"disambiguationData":[TD([[subQ2,-1.0]])],"derivedFrom":subQ1}),-1.0]])]});}
            var Q185;
            {var subQ0=sQuery(id+"F2.wireOp",EDGE,"E100.MirrorCS");var subQ1=sQuery(id+"F2.wireOp",EDGE,"E58.MirrorCS");var subQ2=makeQuery(id+"F2.imprint","INTERSECT",VERTEX,{"derivedFrom":[subQ1,subQ0]});Q185=makeQuery(id+"F2.imprint","IMPRINT",FACE,{"disambiguationData":[TD([[makeQuery(id+"F2.imprint","IMPRINT",EDGE,{"disambiguationData":[TD([[subQ2,-1.0]])],"derivedFrom":subQ1}),-1.0]])]});}
            var Q186;
            {var subQ0=sQuery(id+"F2.wireOp",EDGE,"E96.MirrorCS");var subQ1=sQuery(id+"F2.wireOp",EDGE,"E50.MirrorCS");var subQ2=makeQuery(id+"F2.imprint","INTERSECT",VERTEX,{"derivedFrom":[subQ1,subQ0]});Q186=makeQuery(id+"F2.imprint","IMPRINT",FACE,{"disambiguationData":[TD([[makeQuery(id+"F2.imprint","IMPRINT",EDGE,{"disambiguationData":[TD([[subQ2,-1.0]])],"derivedFrom":subQ1}),-1.0]])]});}
            var Q187;
            {var subQ0=sQuery(id+"F2.wireOp",EDGE,"E83.MirrorCS");var subQ1=sQuery(id+"F2.wireOp",EDGE,"E74.MirrorCS");var subQ2=makeQuery(id+"F2.imprint","INTERSECT",VERTEX,{"derivedFrom":[subQ1,subQ0]});Q187=makeQuery(id+"F2.imprint","IMPRINT",FACE,{"disambiguationData":[TD([[makeQuery(id+"F2.imprint","IMPRINT",EDGE,{"disambiguationData":[TD([[subQ2,-1.0]])],"derivedFrom":subQ1}),1.0]])]});}
            var Q188;
            {var subQ0=sQuery(id+"F2.wireOp",EDGE,"E67.MirrorCS");var subQ1=sQuery(id+"F2.wireOp",EDGE,"E35.MirrorCS");var subQ2=makeQuery(id+"F2.imprint","INTERSECT",VERTEX,{"derivedFrom":[subQ1,subQ0]});Q188=makeQuery(id+"F2.imprint","IMPRINT",FACE,{"disambiguationData":[TD([[makeQuery(id+"F2.imprint","IMPRINT",EDGE,{"disambiguationData":[TD([[subQ2,1.0]])],"derivedFrom":subQ1}),-1.0]])]});}
            var Q189;
            {var subQ0=sQuery(id+"F2.wireOp",EDGE,"E69.MirrorCS");var subQ1=sQuery(id+"F2.wireOp",EDGE,"E58.MirrorCS");var subQ2=makeQuery(id+"F2.imprint","INTERSECT",VERTEX,{"derivedFrom":[subQ1,subQ0]});Q189=makeQuery(id+"F2.imprint","IMPRINT",FACE,{"disambiguationData":[TD([[makeQuery(id+"F2.imprint","IMPRINT",EDGE,{"disambiguationData":[TD([[subQ2,-1.0]])],"derivedFrom":subQ1}),1.0]])]});}
            var Q190;
            {var subQ0=sQuery(id+"F2.wireOp",EDGE,"E101.MirrorCS");var subQ1=sQuery(id+"F2.wireOp",EDGE,"E50.MirrorCS");var subQ2=makeQuery(id+"F2.imprint","INTERSECT",VERTEX,{"derivedFrom":[subQ1,subQ0]});Q190=makeQuery(id+"F2.imprint","IMPRINT",FACE,{"disambiguationData":[TD([[makeQuery(id+"F2.imprint","IMPRINT",EDGE,{"disambiguationData":[TD([[subQ2,-1.0]])],"derivedFrom":subQ1}),-1.0]])]});}
            var Q191;
            {var subQ0=sQuery(id+"F2.wireOp",EDGE,"E81.MirrorCS");var subQ1=sQuery(id+"F2.wireOp",EDGE,"E75.MirrorCS");var subQ2=makeQuery(id+"F2.imprint","INTERSECT",VERTEX,{"derivedFrom":[subQ1,subQ0]});Q191=makeQuery(id+"F2.imprint","IMPRINT",FACE,{"disambiguationData":[TD([[makeQuery(id+"F2.imprint","IMPRINT",EDGE,{"disambiguationData":[TD([[subQ2,-1.0]])],"derivedFrom":subQ1}),1.0]])]});}
            var Q192;
            {var subQ0=sQuery(id+"F2.wireOp",EDGE,"E69.MirrorCS");var subQ1=sQuery(id+"F2.wireOp",EDGE,"E58.MirrorCS");var subQ2=makeQuery(id+"F2.imprint","INTERSECT",VERTEX,{"derivedFrom":[subQ1,subQ0]});Q192=makeQuery(id+"F2.imprint","IMPRINT",FACE,{"disambiguationData":[TD([[makeQuery(id+"F2.imprint","IMPRINT",EDGE,{"disambiguationData":[TD([[subQ2,-1.0]])],"derivedFrom":subQ1}),-1.0]])]});}
            var Q193;
            {var subQ0=sQuery(id+"F2.wireOp",EDGE,"E101.MirrorCS");var subQ1=sQuery(id+"F2.wireOp",EDGE,"E50.MirrorCS");var subQ2=makeQuery(id+"F2.imprint","INTERSECT",VERTEX,{"derivedFrom":[subQ1,subQ0]});Q193=makeQuery(id+"F2.imprint","IMPRINT",FACE,{"disambiguationData":[TD([[makeQuery(id+"F2.imprint","IMPRINT",EDGE,{"disambiguationData":[TD([[subQ2,-1.0]])],"derivedFrom":subQ1}),1.0]])]});}
            var Q194;
            {var subQ0=sQuery(id+"F2.wireOp",EDGE,"E96.MirrorCS");var subQ1=sQuery(id+"F2.wireOp",EDGE,"E75.MirrorCS");var subQ2=makeQuery(id+"F2.imprint","INTERSECT",VERTEX,{"derivedFrom":[subQ1,subQ0]});Q194=makeQuery(id+"F2.imprint","IMPRINT",FACE,{"disambiguationData":[TD([[makeQuery(id+"F2.imprint","IMPRINT",EDGE,{"disambiguationData":[TD([[subQ2,-1.0]])],"derivedFrom":subQ1}),1.0]])]});}
            var Q195;
            {var subQ0=sQuery(id+"F2.wireOp",EDGE,"E82.MirrorCS");var subQ1=sQuery(id+"F2.wireOp",EDGE,"E58.MirrorCS");var subQ2=makeQuery(id+"F2.imprint","INTERSECT",VERTEX,{"derivedFrom":[subQ1,subQ0]});Q195=makeQuery(id+"F2.imprint","IMPRINT",FACE,{"disambiguationData":[TD([[makeQuery(id+"F2.imprint","IMPRINT",EDGE,{"disambiguationData":[TD([[subQ2,-1.0]])],"derivedFrom":subQ1}),1.0]])]});}
            var Q196;
            {var subQ0=sQuery(id+"F2.wireOp",EDGE,"E70.MirrorCS");var subQ1=sQuery(id+"F2.wireOp",EDGE,"E50.MirrorCS");var subQ2=makeQuery(id+"F2.imprint","INTERSECT",VERTEX,{"derivedFrom":[subQ1,subQ0]});Q196=makeQuery(id+"F2.imprint","IMPRINT",FACE,{"disambiguationData":[TD([[makeQuery(id+"F2.imprint","IMPRINT",EDGE,{"disambiguationData":[TD([[subQ2,-1.0]])],"derivedFrom":subQ1}),-1.0]])]});}
            var Q197;
            {var subQ0=sQuery(id+"F2.wireOp",EDGE,"E99.MirrorCS");var subQ1=sQuery(id+"F2.wireOp",EDGE,"E43.MirrorCS");var subQ2=makeQuery(id+"F2.imprint","INTERSECT",VERTEX,{"derivedFrom":[subQ1,subQ0]});Q197=makeQuery(id+"F2.imprint","IMPRINT",FACE,{"disambiguationData":[TD([[makeQuery(id+"F2.imprint","IMPRINT",EDGE,{"disambiguationData":[TD([[subQ2,1.0]])],"derivedFrom":subQ1}),1.0]])]});}
            var Q198;
            {var subQ3=sQuery(id+"F2.wireOp",EDGE,"E96.MirrorCS");var subQ6=sQuery(id+"F2.wireOp",EDGE,"E43.MirrorCS");var subQ11=makeQuery(id+"F2.imprint","INTERSECT",VERTEX,{"derivedFrom":[subQ6,subQ3]});Q198=makeQuery(id+"F2.imprint","IMPRINT",FACE,{"disambiguationData":[TD([[makeQuery(id+"F2.imprint","IMPRINT",EDGE,{"disambiguationData":[TD([[subQ11,-1.0]])],"derivedFrom":subQ6}),1.0]])]});}
            var Q199;
            {var subQ0=sQuery(id+"F2.wireOp",EDGE,"E70.MirrorCS");var subQ1=sQuery(id+"F2.wireOp",EDGE,"E50.MirrorCS");var subQ2=makeQuery(id+"F2.imprint","INTERSECT",VERTEX,{"derivedFrom":[subQ1,subQ0]});Q199=makeQuery(id+"F2.imprint","IMPRINT",FACE,{"disambiguationData":[TD([[makeQuery(id+"F2.imprint","IMPRINT",EDGE,{"disambiguationData":[TD([[subQ2,-1.0]])],"derivedFrom":subQ1}),1.0]])]});}
            var Q200;
            {var subQ1=sQuery(id+"F2.wireOp",EDGE,"E41.MirrorCS");var subQ5=sQuery(id+"F2.wireOp",EDGE,"E88.MirrorCS");var subQ6=makeQuery(id+"F2.imprint","INTERSECT",VERTEX,{"derivedFrom":[subQ1,subQ5]});Q200=makeQuery(id+"F2.imprint","IMPRINT",FACE,{"disambiguationData":[TD([[makeQuery(id+"F2.imprint","IMPRINT",EDGE,{"disambiguationData":[TD([[subQ6,1.0]])],"derivedFrom":subQ1}),1.0]])]});}
            var Q201;
            {var subQ0=sQuery(id+"F2.wireOp",EDGE,"E64.MirrorCS");var subQ1=sQuery(id+"F2.wireOp",EDGE,"E46.MirrorCS");var subQ2=makeQuery(id+"F2.imprint","INTERSECT",VERTEX,{"derivedFrom":[subQ1,subQ0]});Q201=makeQuery(id+"F2.imprint","IMPRINT",FACE,{"disambiguationData":[TD([[makeQuery(id+"F2.imprint","IMPRINT",EDGE,{"disambiguationData":[TD([[subQ2,1.0]])],"derivedFrom":subQ1}),1.0]])]});}
            var Q202;
            {var subQ0=sQuery(id+"F2.wireOp",EDGE,"E96.MirrorCS");var subQ1=sQuery(id+"F2.wireOp",EDGE,"E88.MirrorCS");var subQ2=makeQuery(id+"F2.imprint","INTERSECT",VERTEX,{"derivedFrom":[subQ1,subQ0]});Q202=makeQuery(id+"F2.imprint","IMPRINT",FACE,{"disambiguationData":[TD([[makeQuery(id+"F2.imprint","IMPRINT",EDGE,{"disambiguationData":[TD([[subQ2,-1.0]])],"derivedFrom":subQ1}),1.0]])]});}
            var Q203;
            {var subQ0=sQuery(id+"F2.wireOp",EDGE,"E69.MirrorCS");var subQ1=sQuery(id+"F2.wireOp",EDGE,"E61.MirrorCS");var subQ2=makeQuery(id+"F2.imprint","INTERSECT",VERTEX,{"derivedFrom":[subQ1,subQ0]});Q203=makeQuery(id+"F2.imprint","IMPRINT",FACE,{"disambiguationData":[TD([[makeQuery(id+"F2.imprint","IMPRINT",EDGE,{"disambiguationData":[TD([[subQ2,-1.0]])],"derivedFrom":subQ1}),1.0]])]});}
            var Q204;
            {var subQ0=sQuery(id+"F2.wireOp",EDGE,"E61.MirrorCS");var subQ1=sQuery(id+"F2.wireOp",EDGE,"E34.MirrorCS");var subQ2=makeQuery(id+"F2.imprint","INTERSECT",VERTEX,{"derivedFrom":[subQ1,subQ0]});Q204=makeQuery(id+"F2.imprint","IMPRINT",FACE,{"disambiguationData":[TD([[makeQuery(id+"F2.imprint","IMPRINT",EDGE,{"disambiguationData":[TD([[subQ2,1.0]])],"derivedFrom":subQ1}),1.0]])]});}
            var Q205;
            {var subQ6=sQuery(id+"F2.wireOp",EDGE,"E98.MirrorCS");var subQ8=sQuery(id+"F2.wireOp",EDGE,"E42.MirrorCS");var subQ9=makeQuery(id+"F2.imprint","INTERSECT",VERTEX,{"derivedFrom":[subQ8,subQ6]});Q205=makeQuery(id+"F2.imprint","IMPRINT",FACE,{"disambiguationData":[TD([[makeQuery(id+"F2.imprint","IMPRINT",EDGE,{"disambiguationData":[TD([[subQ9,1.0]])],"derivedFrom":subQ8}),1.0]])]});}
            var Q206;
            {var subQ0=sQuery(id+"F2.wireOp",EDGE,"E82.MirrorCS");var subQ1=sQuery(id+"F2.wireOp",EDGE,"E61.MirrorCS");var subQ2=makeQuery(id+"F2.imprint","INTERSECT",VERTEX,{"derivedFrom":[subQ1,subQ0]});Q206=makeQuery(id+"F2.imprint","IMPRINT",FACE,{"disambiguationData":[TD([[makeQuery(id+"F2.imprint","IMPRINT",EDGE,{"disambiguationData":[TD([[subQ2,-1.0]])],"derivedFrom":subQ1}),1.0]])]});}
            var Q207;
            {var subQ0=sQuery(id+"F2.wireOp",EDGE,"E83.MirrorCS");var subQ1=sQuery(id+"F2.wireOp",EDGE,"E67.MirrorCS");var subQ2=makeQuery(id+"F2.imprint","INTERSECT",VERTEX,{"derivedFrom":[subQ1,subQ0]});Q207=makeQuery(id+"F2.imprint","IMPRINT",FACE,{"disambiguationData":[TD([[makeQuery(id+"F2.imprint","IMPRINT",EDGE,{"disambiguationData":[TD([[subQ2,-1.0]])],"derivedFrom":subQ1}),-1.0]])]});}
            var Q208;
            {var subQ0=sQuery(id+"F2.wireOp",EDGE,"E94.MirrorCS");var subQ1=sQuery(id+"F2.wireOp",EDGE,"E34.MirrorCS");var subQ2=makeQuery(id+"F2.imprint","INTERSECT",VERTEX,{"derivedFrom":[subQ1,subQ0]});Q208=makeQuery(id+"F2.imprint","IMPRINT",FACE,{"disambiguationData":[TD([[makeQuery(id+"F2.imprint","IMPRINT",EDGE,{"disambiguationData":[TD([[subQ2,-1.0]])],"derivedFrom":subQ1}),1.0]])]});}
            var Q209;
            {var subQ0=sQuery(id+"F2.wireOp",EDGE,"E69.MirrorCS");var subQ1=sQuery(id+"F2.wireOp",EDGE,"E36.MirrorCS");var subQ2=makeQuery(id+"F2.imprint","INTERSECT",VERTEX,{"derivedFrom":[subQ1,subQ0]});Q209=makeQuery(id+"F2.imprint","IMPRINT",FACE,{"disambiguationData":[TD([[makeQuery(id+"F2.imprint","IMPRINT",EDGE,{"disambiguationData":[TD([[subQ2,-1.0]])],"derivedFrom":subQ1}),-1.0]])]});}
            var Q210;
            {var subQ0=sQuery(id+"F2.wireOp",EDGE,"E101.MirrorCS");var subQ1=sQuery(id+"F2.wireOp",EDGE,"E37.MirrorCS");var subQ2=makeQuery(id+"F2.imprint","INTERSECT",VERTEX,{"derivedFrom":[subQ1,subQ0]});Q210=makeQuery(id+"F2.imprint","IMPRINT",FACE,{"disambiguationData":[TD([[makeQuery(id+"F2.imprint","IMPRINT",EDGE,{"disambiguationData":[TD([[subQ2,-1.0]])],"derivedFrom":subQ1}),-1.0]])]});}
            var Q211;
            {var subQ0=sQuery(id+"F2.wireOp",EDGE,"E82.MirrorCS");var subQ1=sQuery(id+"F2.wireOp",EDGE,"E34.MirrorCS");var subQ2=makeQuery(id+"F2.imprint","INTERSECT",VERTEX,{"derivedFrom":[subQ1,subQ0]});Q211=makeQuery(id+"F2.imprint","IMPRINT",FACE,{"disambiguationData":[TD([[makeQuery(id+"F2.imprint","IMPRINT",EDGE,{"disambiguationData":[TD([[subQ2,-1.0]])],"derivedFrom":subQ1}),1.0]])]});}
            var Q212;
            {var subQ0=sQuery(id+"F2.wireOp",EDGE,"E74.MirrorCS");var subQ1=sQuery(id+"F2.wireOp",EDGE,"E36.MirrorCS");var subQ2=makeQuery(id+"F2.imprint","INTERSECT",VERTEX,{"derivedFrom":[subQ1,subQ0]});Q212=makeQuery(id+"F2.imprint","IMPRINT",FACE,{"disambiguationData":[TD([[makeQuery(id+"F2.imprint","IMPRINT",EDGE,{"disambiguationData":[TD([[subQ2,1.0]])],"derivedFrom":subQ1}),1.0]])]});}
            var Q213;
            {var subQ0=sQuery(id+"F2.wireOp",EDGE,"E54.MirrorCS");var subQ1=sQuery(id+"F2.wireOp",EDGE,"E34.MirrorCS");var subQ2=makeQuery(id+"F2.imprint","INTERSECT",VERTEX,{"derivedFrom":[subQ1,subQ0]});Q213=makeQuery(id+"F2.imprint","IMPRINT",FACE,{"disambiguationData":[TD([[makeQuery(id+"F2.imprint","IMPRINT",EDGE,{"disambiguationData":[TD([[subQ2,-1.0]])],"derivedFrom":subQ1}),1.0]])]});}
            var Q214;
            {var subQ0=sQuery(id+"F2.wireOp",EDGE,"E70.MirrorCS");var subQ1=sQuery(id+"F2.wireOp",EDGE,"E43.MirrorCS");var subQ2=makeQuery(id+"F2.imprint","INTERSECT",VERTEX,{"derivedFrom":[subQ1,subQ0]});Q214=makeQuery(id+"F2.imprint","IMPRINT",FACE,{"disambiguationData":[TD([[makeQuery(id+"F2.imprint","IMPRINT",EDGE,{"disambiguationData":[TD([[subQ2,-1.0]])],"derivedFrom":subQ1}),1.0]])]});}
            var Q215;
            {var subQ0=sQuery(id+"F2.wireOp",EDGE,"E82.MirrorCS");var subQ1=sQuery(id+"F2.wireOp",EDGE,"E36.MirrorCS");var subQ2=makeQuery(id+"F2.imprint","INTERSECT",VERTEX,{"derivedFrom":[subQ1,subQ0]});Q215=makeQuery(id+"F2.imprint","IMPRINT",FACE,{"disambiguationData":[TD([[makeQuery(id+"F2.imprint","IMPRINT",EDGE,{"disambiguationData":[TD([[subQ2,-1.0]])],"derivedFrom":subQ1}),1.0]])]});}
            var Q216;
            {var subQ0=sQuery(id+"F2.wireOp",EDGE,"E60.MirrorCS");var subQ1=sQuery(id+"F2.wireOp",EDGE,"E34.MirrorCS");var subQ2=makeQuery(id+"F2.imprint","INTERSECT",VERTEX,{"derivedFrom":[subQ1,subQ0]});Q216=makeQuery(id+"F2.imprint","IMPRINT",FACE,{"disambiguationData":[TD([[makeQuery(id+"F2.imprint","IMPRINT",EDGE,{"disambiguationData":[TD([[subQ2,-1.0]])],"derivedFrom":subQ1}),1.0]])]});}
            var Q217;
            {var subQ0=sQuery(id+"F2.wireOp",EDGE,"E69.MirrorCS");var subQ1=sQuery(id+"F2.wireOp",EDGE,"E35.MirrorCS");var subQ2=makeQuery(id+"F2.imprint","INTERSECT",VERTEX,{"derivedFrom":[subQ1,subQ0]});Q217=makeQuery(id+"F2.imprint","IMPRINT",FACE,{"disambiguationData":[TD([[makeQuery(id+"F2.imprint","IMPRINT",EDGE,{"disambiguationData":[TD([[subQ2,-1.0]])],"derivedFrom":subQ1}),-1.0]])]});}
            var Q218;
            {var subQ0=sQuery(id+"F2.wireOp",EDGE,"E96.MirrorCS");var subQ1=sQuery(id+"F2.wireOp",EDGE,"E39.MirrorCS");var subQ2=makeQuery(id+"F2.imprint","INTERSECT",VERTEX,{"derivedFrom":[subQ1,subQ0]});Q218=makeQuery(id+"F2.imprint","IMPRINT",FACE,{"disambiguationData":[TD([[makeQuery(id+"F2.imprint","IMPRINT",EDGE,{"disambiguationData":[TD([[subQ2,-1.0]])],"derivedFrom":subQ1}),1.0]])]});}
            var Q219;
            {var subQ0=sQuery(id+"F2.wireOp",EDGE,"E100.MirrorCS");var subQ1=sQuery(id+"F2.wireOp",EDGE,"E35.MirrorCS");var subQ2=makeQuery(id+"F2.imprint","INTERSECT",VERTEX,{"derivedFrom":[subQ1,subQ0]});Q219=makeQuery(id+"F2.imprint","IMPRINT",FACE,{"disambiguationData":[TD([[makeQuery(id+"F2.imprint","IMPRINT",EDGE,{"disambiguationData":[TD([[subQ2,-1.0]])],"derivedFrom":subQ1}),-1.0]])]});}
            var Q220;
            {var subQ0=sQuery(id+"F2.wireOp",EDGE,"E87.MirrorCS");var subQ1=sQuery(id+"F2.wireOp",EDGE,"E40.MirrorCS");var subQ2=makeQuery(id+"F2.imprint","INTERSECT",VERTEX,{"derivedFrom":[subQ1,subQ0]});Q220=makeQuery(id+"F2.imprint","IMPRINT",FACE,{"disambiguationData":[TD([[makeQuery(id+"F2.imprint","IMPRINT",EDGE,{"disambiguationData":[TD([[subQ2,1.0]])],"derivedFrom":subQ1}),1.0]])]});}
            var Q221;
            {var subQ0=sQuery(id+"F2.wireOp",EDGE,"E95.MirrorCS");var subQ1=sQuery(id+"F2.wireOp",EDGE,"E35.MirrorCS");var subQ2=makeQuery(id+"F2.imprint","INTERSECT",VERTEX,{"derivedFrom":[subQ1,subQ0]});Q221=makeQuery(id+"F2.imprint","IMPRINT",FACE,{"disambiguationData":[TD([[makeQuery(id+"F2.imprint","IMPRINT",EDGE,{"disambiguationData":[TD([[subQ2,-1.0]])],"derivedFrom":subQ1}),-1.0]])]});}
            var Q222;
            {var subQ5=sQuery(id+"F2.wireOp",EDGE,"E58.MirrorCS");var subQ6=sQuery(id+"F2.wireOp",EDGE,"E33.MirrorCS");var subQ7=makeQuery(id+"F2.imprint","INTERSECT",VERTEX,{"derivedFrom":[subQ6,subQ5]});Q222=makeQuery(id+"F2.imprint","IMPRINT",FACE,{"disambiguationData":[TD([[makeQuery(id+"F2.imprint","IMPRINT",EDGE,{"disambiguationData":[TD([[subQ7,1.0]])],"derivedFrom":subQ6}),-1.0]])]});}
            var Q223;
            {var subQ0=sQuery(id+"F2.wireOp",EDGE,"E70.MirrorCS");var subQ1=sQuery(id+"F2.wireOp",EDGE,"E36.MirrorCS");var subQ2=makeQuery(id+"F2.imprint","INTERSECT",VERTEX,{"derivedFrom":[subQ1,subQ0]});Q223=makeQuery(id+"F2.imprint","IMPRINT",FACE,{"disambiguationData":[TD([[makeQuery(id+"F2.imprint","IMPRINT",EDGE,{"disambiguationData":[TD([[subQ2,-1.0]])],"derivedFrom":subQ1}),1.0]])]});}
            var Q224;
            {var subQ0=sQuery(id+"F2.wireOp",EDGE,"E60.MirrorCS");var subQ1=sQuery(id+"F2.wireOp",EDGE,"E33.MirrorCS");var subQ2=makeQuery(id+"F2.imprint","INTERSECT",VERTEX,{"derivedFrom":[subQ1,subQ0]});Q224=makeQuery(id+"F2.imprint","IMPRINT",FACE,{"disambiguationData":[TD([[makeQuery(id+"F2.imprint","IMPRINT",EDGE,{"disambiguationData":[TD([[subQ2,-1.0]])],"derivedFrom":subQ1}),1.0]])]});}
            var Q225;
            {var subQ7=sQuery(id+"F2.wireOp",EDGE,"E36.MirrorCS");var subQ10=sQuery(id+"F2.wireOp",EDGE,"E74.MirrorCS");var subQ11=makeQuery(id+"F2.imprint","INTERSECT",VERTEX,{"derivedFrom":[subQ7,subQ10]});Q225=makeQuery(id+"F2.imprint","IMPRINT",FACE,{"disambiguationData":[TD([[makeQuery(id+"F2.imprint","IMPRINT",EDGE,{"disambiguationData":[TD([[subQ11,1.0]])],"derivedFrom":subQ7}),-1.0]])]});}
            var Q226;
            {var subQ0=sQuery(id+"F2.wireOp",EDGE,"E54.MirrorCS");var subQ1=sQuery(id+"F2.wireOp",EDGE,"E33.MirrorCS");var subQ2=makeQuery(id+"F2.imprint","INTERSECT",VERTEX,{"derivedFrom":[subQ1,subQ0]});Q226=makeQuery(id+"F2.imprint","IMPRINT",FACE,{"disambiguationData":[TD([[makeQuery(id+"F2.imprint","IMPRINT",EDGE,{"disambiguationData":[TD([[subQ2,-1.0]])],"derivedFrom":subQ1}),-1.0]])]});}
            var Q227;
            {var subQ0=sQuery(id+"F2.wireOp",EDGE,"E50.MirrorCS");var subQ1=sQuery(id+"F2.wireOp",EDGE,"E45.MirrorCS");var subQ2=makeQuery(id+"F2.imprint","INTERSECT",VERTEX,{"derivedFrom":[subQ1,subQ0]});Q227=makeQuery(id+"F2.imprint","IMPRINT",FACE,{"disambiguationData":[TD([[makeQuery(id+"F2.imprint","IMPRINT",EDGE,{"disambiguationData":[TD([[subQ2,1.0]])],"derivedFrom":subQ1}),1.0]])]});}
            var Q228;
            {var subQ0=sQuery(id+"F2.wireOp",EDGE,"E63.MirrorCS");var subQ1=sQuery(id+"F2.wireOp",EDGE,"E34.MirrorCS");var subQ2=makeQuery(id+"F2.imprint","INTERSECT",VERTEX,{"derivedFrom":[subQ1,subQ0]});Q228=makeQuery(id+"F2.imprint","IMPRINT",FACE,{"disambiguationData":[TD([[makeQuery(id+"F2.imprint","IMPRINT",EDGE,{"disambiguationData":[TD([[subQ2,-1.0]])],"derivedFrom":subQ1}),1.0]])]});}
            var Q229;
            {var subQ0=sQuery(id+"F2.wireOp",EDGE,"E69.MirrorCS");var subQ1=sQuery(id+"F2.wireOp",EDGE,"E33.MirrorCS");var subQ2=makeQuery(id+"F2.imprint","INTERSECT",VERTEX,{"derivedFrom":[subQ1,subQ0]});Q229=makeQuery(id+"F2.imprint","IMPRINT",FACE,{"disambiguationData":[TD([[makeQuery(id+"F2.imprint","IMPRINT",EDGE,{"disambiguationData":[TD([[subQ2,-1.0]])],"derivedFrom":subQ1}),1.0]])]});}
            var Q230;
            {var subQ0=sQuery(id+"F2.wireOp",EDGE,"E94.MirrorCS");var subQ1=sQuery(id+"F2.wireOp",EDGE,"E35.MirrorCS");var subQ2=makeQuery(id+"F2.imprint","INTERSECT",VERTEX,{"derivedFrom":[subQ1,subQ0]});Q230=makeQuery(id+"F2.imprint","IMPRINT",FACE,{"disambiguationData":[TD([[makeQuery(id+"F2.imprint","IMPRINT",EDGE,{"disambiguationData":[TD([[subQ2,-1.0]])],"derivedFrom":subQ1}),-1.0]])]});}
            var Q231;
            {var subQ0=sQuery(id+"F2.wireOp",EDGE,"E101.MirrorCS");var subQ1=sQuery(id+"F2.wireOp",EDGE,"E43.MirrorCS");var subQ2=makeQuery(id+"F2.imprint","INTERSECT",VERTEX,{"derivedFrom":[subQ1,subQ0]});Q231=makeQuery(id+"F2.imprint","IMPRINT",FACE,{"disambiguationData":[TD([[makeQuery(id+"F2.imprint","IMPRINT",EDGE,{"disambiguationData":[TD([[subQ2,-1.0]])],"derivedFrom":subQ1}),1.0]])]});}
            var Q232;
            {var subQ0=sQuery(id+"F2.wireOp",EDGE,"E82.MirrorCS");var subQ1=sQuery(id+"F2.wireOp",EDGE,"E35.MirrorCS");var subQ2=makeQuery(id+"F2.imprint","INTERSECT",VERTEX,{"derivedFrom":[subQ1,subQ0]});Q232=makeQuery(id+"F2.imprint","IMPRINT",FACE,{"disambiguationData":[TD([[makeQuery(id+"F2.imprint","IMPRINT",EDGE,{"disambiguationData":[TD([[subQ2,-1.0]])],"derivedFrom":subQ1}),-1.0]])]});}
            var Q233;
            {var subQ0=sQuery(id+"F2.wireOp",EDGE,"E83.MirrorCS");var subQ1=sQuery(id+"F2.wireOp",EDGE,"E37.MirrorCS");var subQ2=makeQuery(id+"F2.imprint","INTERSECT",VERTEX,{"derivedFrom":[subQ1,subQ0]});Q233=makeQuery(id+"F2.imprint","IMPRINT",FACE,{"disambiguationData":[TD([[makeQuery(id+"F2.imprint","IMPRINT",EDGE,{"disambiguationData":[TD([[subQ2,-1.0]])],"derivedFrom":subQ1}),1.0]])]});}
            var Q234;
            {var subQ0=sQuery(id+"F2.wireOp",EDGE,"E96.MirrorCS");var subQ1=sQuery(id+"F2.wireOp",EDGE,"E37.MirrorCS");var subQ2=makeQuery(id+"F2.imprint","INTERSECT",VERTEX,{"derivedFrom":[subQ1,subQ0]});Q234=makeQuery(id+"F2.imprint","IMPRINT",FACE,{"disambiguationData":[TD([[makeQuery(id+"F2.imprint","IMPRINT",EDGE,{"disambiguationData":[TD([[subQ2,-1.0]])],"derivedFrom":subQ1}),1.0]])]});}
            var Q235;
            {var subQ0=sQuery(id+"F2.wireOp",EDGE,"E70.MirrorCS");var subQ1=sQuery(id+"F2.wireOp",EDGE,"E37.MirrorCS");var subQ2=makeQuery(id+"F2.imprint","INTERSECT",VERTEX,{"derivedFrom":[subQ1,subQ0]});Q235=makeQuery(id+"F2.imprint","IMPRINT",FACE,{"disambiguationData":[TD([[makeQuery(id+"F2.imprint","IMPRINT",EDGE,{"disambiguationData":[TD([[subQ2,-1.0]])],"derivedFrom":subQ1}),1.0]])]});}
            var Q236;
            {var subQ0=sQuery(id+"F2.wireOp",EDGE,"E83.MirrorCS");var subQ1=sQuery(id+"F2.wireOp",EDGE,"E43.MirrorCS");var subQ2=makeQuery(id+"F2.imprint","INTERSECT",VERTEX,{"derivedFrom":[subQ1,subQ0]});Q236=makeQuery(id+"F2.imprint","IMPRINT",FACE,{"disambiguationData":[TD([[makeQuery(id+"F2.imprint","IMPRINT",EDGE,{"disambiguationData":[TD([[subQ2,-1.0]])],"derivedFrom":subQ1}),1.0]])]});}
            var Q237;
            {var subQ0=sQuery(id+"F2.wireOp",EDGE,"E67.MirrorCS");var subQ1=sQuery(id+"F2.wireOp",EDGE,"E35.MirrorCS");var subQ2=makeQuery(id+"F2.imprint","INTERSECT",VERTEX,{"derivedFrom":[subQ1,subQ0]});Q237=makeQuery(id+"F2.imprint","IMPRINT",FACE,{"disambiguationData":[TD([[makeQuery(id+"F2.imprint","IMPRINT",EDGE,{"disambiguationData":[TD([[subQ2,1.0]])],"derivedFrom":subQ1}),1.0]])]});}
            var Q238;
            {var subQ0=sQuery(id+"F2.wireOp",EDGE,"E95.MirrorCS");var subQ1=sQuery(id+"F2.wireOp",EDGE,"E41.MirrorCS");var subQ2=makeQuery(id+"F2.imprint","INTERSECT",VERTEX,{"derivedFrom":[subQ1,subQ0]});Q238=makeQuery(id+"F2.imprint","IMPRINT",FACE,{"disambiguationData":[TD([[makeQuery(id+"F2.imprint","IMPRINT",EDGE,{"disambiguationData":[TD([[subQ2,-1.0]])],"derivedFrom":subQ1}),1.0]])]});}
            var Q239;
            {var subQ0=sQuery(id+"F2.wireOp",EDGE,"E54.MirrorCS");var subQ1=sQuery(id+"F2.wireOp",EDGE,"E33.MirrorCS");var subQ2=makeQuery(id+"F2.imprint","INTERSECT",VERTEX,{"derivedFrom":[subQ1,subQ0]});Q239=makeQuery(id+"F2.imprint","IMPRINT",FACE,{"disambiguationData":[TD([[makeQuery(id+"F2.imprint","IMPRINT",EDGE,{"disambiguationData":[TD([[subQ2,-1.0]])],"derivedFrom":subQ1}),1.0]])]});}
            var Q240;
            {var subQ0=sQuery(id+"F2.wireOp",EDGE,"E69.MirrorCS");var subQ1=sQuery(id+"F2.wireOp",EDGE,"E36.MirrorCS");var subQ2=makeQuery(id+"F2.imprint","INTERSECT",VERTEX,{"derivedFrom":[subQ1,subQ0]});Q240=makeQuery(id+"F2.imprint","IMPRINT",FACE,{"disambiguationData":[TD([[makeQuery(id+"F2.imprint","IMPRINT",EDGE,{"disambiguationData":[TD([[subQ2,-1.0]])],"derivedFrom":subQ1}),1.0]])]});}
            var Q241;
            {var subQ0=sQuery(id+"F2.wireOp",EDGE,"E101.MirrorCS");var subQ1=sQuery(id+"F2.wireOp",EDGE,"E42.MirrorCS");var subQ2=makeQuery(id+"F2.imprint","INTERSECT",VERTEX,{"derivedFrom":[subQ1,subQ0]});Q241=makeQuery(id+"F2.imprint","IMPRINT",FACE,{"disambiguationData":[TD([[makeQuery(id+"F2.imprint","IMPRINT",EDGE,{"disambiguationData":[TD([[subQ2,-1.0]])],"derivedFrom":subQ1}),1.0]])]});}
            var Q242;
            {var subQ0=sQuery(id+"F2.wireOp",EDGE,"E70.MirrorCS");var subQ1=sQuery(id+"F2.wireOp",EDGE,"E41.MirrorCS");var subQ2=makeQuery(id+"F2.imprint","INTERSECT",VERTEX,{"derivedFrom":[subQ1,subQ0]});Q242=makeQuery(id+"F2.imprint","IMPRINT",FACE,{"disambiguationData":[TD([[makeQuery(id+"F2.imprint","IMPRINT",EDGE,{"disambiguationData":[TD([[subQ2,-1.0]])],"derivedFrom":subQ1}),1.0]])]});}
            var Q243;
            {var subQ0=sQuery(id+"F2.wireOp",EDGE,"E100.MirrorCS");var subQ1=sQuery(id+"F2.wireOp",EDGE,"E36.MirrorCS");var subQ2=makeQuery(id+"F2.imprint","INTERSECT",VERTEX,{"derivedFrom":[subQ1,subQ0]});Q243=makeQuery(id+"F2.imprint","IMPRINT",FACE,{"disambiguationData":[TD([[makeQuery(id+"F2.imprint","IMPRINT",EDGE,{"disambiguationData":[TD([[subQ2,-1.0]])],"derivedFrom":subQ1}),1.0]])]});}
            var Q244;
            {var subQ0=sQuery(id+"F2.wireOp",EDGE,"E94.MirrorCS");var subQ1=sQuery(id+"F2.wireOp",EDGE,"E33.MirrorCS");var subQ2=makeQuery(id+"F2.imprint","INTERSECT",VERTEX,{"derivedFrom":[subQ1,subQ0]});Q244=makeQuery(id+"F2.imprint","IMPRINT",FACE,{"disambiguationData":[TD([[makeQuery(id+"F2.imprint","IMPRINT",EDGE,{"disambiguationData":[TD([[subQ2,-1.0]])],"derivedFrom":subQ1}),1.0]])]});}
            var Q245;
            {var subQ0=sQuery(id+"F2.wireOp",EDGE,"E95.MirrorCS");var subQ1=sQuery(id+"F2.wireOp",EDGE,"E36.MirrorCS");var subQ2=makeQuery(id+"F2.imprint","INTERSECT",VERTEX,{"derivedFrom":[subQ1,subQ0]});Q245=makeQuery(id+"F2.imprint","IMPRINT",FACE,{"disambiguationData":[TD([[makeQuery(id+"F2.imprint","IMPRINT",EDGE,{"disambiguationData":[TD([[subQ2,-1.0]])],"derivedFrom":subQ1}),1.0]])]});}
            var Q246;
            {var subQ0=sQuery(id+"F2.wireOp",EDGE,"E58.MirrorCS");var subQ1=sQuery(id+"F2.wireOp",EDGE,"E33.MirrorCS");var subQ2=makeQuery(id+"F2.imprint","INTERSECT",VERTEX,{"derivedFrom":[subQ1,subQ0]});Q246=makeQuery(id+"F2.imprint","IMPRINT",FACE,{"disambiguationData":[TD([[makeQuery(id+"F2.imprint","IMPRINT",EDGE,{"disambiguationData":[TD([[subQ2,1.0]])],"derivedFrom":subQ1}),1.0]])]});}
            var Q247;
            {var subQ0=sQuery(id+"F2.wireOp",EDGE,"E100.MirrorCS");var subQ1=sQuery(id+"F2.wireOp",EDGE,"E33.MirrorCS");var subQ2=makeQuery(id+"F2.imprint","INTERSECT",VERTEX,{"derivedFrom":[subQ1,subQ0]});Q247=makeQuery(id+"F2.imprint","IMPRINT",FACE,{"disambiguationData":[TD([[makeQuery(id+"F2.imprint","IMPRINT",EDGE,{"disambiguationData":[TD([[subQ2,-1.0]])],"derivedFrom":subQ1}),-1.0]])]});}
            var Q248;
            {var subQ0=sQuery(id+"F2.wireOp",EDGE,"E70.MirrorCS");var subQ1=sQuery(id+"F2.wireOp",EDGE,"E37.MirrorCS");var subQ2=makeQuery(id+"F2.imprint","INTERSECT",VERTEX,{"derivedFrom":[subQ1,subQ0]});Q248=makeQuery(id+"F2.imprint","IMPRINT",FACE,{"disambiguationData":[TD([[makeQuery(id+"F2.imprint","IMPRINT",EDGE,{"disambiguationData":[TD([[subQ2,-1.0]])],"derivedFrom":subQ1}),-1.0]])]});}
            var Q249;
            {var subQ0=sQuery(id+"F2.wireOp",EDGE,"E96.MirrorCS");var subQ1=sQuery(id+"F2.wireOp",EDGE,"E37.MirrorCS");var subQ2=makeQuery(id+"F2.imprint","INTERSECT",VERTEX,{"derivedFrom":[subQ1,subQ0]});Q249=makeQuery(id+"F2.imprint","IMPRINT",FACE,{"disambiguationData":[TD([[makeQuery(id+"F2.imprint","IMPRINT",EDGE,{"disambiguationData":[TD([[subQ2,-1.0]])],"derivedFrom":subQ1}),-1.0]])]});}
            var Q250;
            {var subQ0=sQuery(id+"F2.wireOp",EDGE,"E101.MirrorCS");var subQ1=sQuery(id+"F2.wireOp",EDGE,"E37.MirrorCS");var subQ2=makeQuery(id+"F2.imprint","INTERSECT",VERTEX,{"derivedFrom":[subQ1,subQ0]});Q250=makeQuery(id+"F2.imprint","IMPRINT",FACE,{"disambiguationData":[TD([[makeQuery(id+"F2.imprint","IMPRINT",EDGE,{"disambiguationData":[TD([[subQ2,-1.0]])],"derivedFrom":subQ1}),1.0]])]});}
            var Q251;
            {var subQ0=sQuery(id+"F2.wireOp",EDGE,"E83.MirrorCS");var subQ1=sQuery(id+"F2.wireOp",EDGE,"E41.MirrorCS");var subQ2=makeQuery(id+"F2.imprint","INTERSECT",VERTEX,{"derivedFrom":[subQ1,subQ0]});Q251=makeQuery(id+"F2.imprint","IMPRINT",FACE,{"disambiguationData":[TD([[makeQuery(id+"F2.imprint","IMPRINT",EDGE,{"disambiguationData":[TD([[subQ2,-1.0]])],"derivedFrom":subQ1}),1.0]])]});}
            var Q252;
            {var subQ0=sQuery(id+"F2.wireOp",EDGE,"E100.MirrorCS");var subQ1=sQuery(id+"F2.wireOp",EDGE,"E36.MirrorCS");var subQ2=makeQuery(id+"F2.imprint","INTERSECT",VERTEX,{"derivedFrom":[subQ1,subQ0]});Q252=makeQuery(id+"F2.imprint","IMPRINT",FACE,{"disambiguationData":[TD([[makeQuery(id+"F2.imprint","IMPRINT",EDGE,{"disambiguationData":[TD([[subQ2,-1.0]])],"derivedFrom":subQ1}),-1.0]])]});}
            var Q253;
            {var subQ0=sQuery(id+"F2.wireOp",EDGE,"E94.MirrorCS");var subQ1=sQuery(id+"F2.wireOp",EDGE,"E33.MirrorCS");var subQ2=makeQuery(id+"F2.imprint","INTERSECT",VERTEX,{"derivedFrom":[subQ1,subQ0]});Q253=makeQuery(id+"F2.imprint","IMPRINT",FACE,{"disambiguationData":[TD([[makeQuery(id+"F2.imprint","IMPRINT",EDGE,{"disambiguationData":[TD([[subQ2,-1.0]])],"derivedFrom":subQ1}),-1.0]])]});}
            var Q254;
            {var subQ0=sQuery(id+"F2.wireOp",EDGE,"E96.MirrorCS");var subQ1=sQuery(id+"F2.wireOp",EDGE,"E41.MirrorCS");var subQ2=makeQuery(id+"F2.imprint","INTERSECT",VERTEX,{"derivedFrom":[subQ1,subQ0]});Q254=makeQuery(id+"F2.imprint","IMPRINT",FACE,{"disambiguationData":[TD([[makeQuery(id+"F2.imprint","IMPRINT",EDGE,{"disambiguationData":[TD([[subQ2,-1.0]])],"derivedFrom":subQ1}),1.0]])]});}
            var Q255;
            {var subQ0=sQuery(id+"F2.wireOp",EDGE,"E82.MirrorCS");var subQ1=sQuery(id+"F2.wireOp",EDGE,"E33.MirrorCS");var subQ2=makeQuery(id+"F2.imprint","INTERSECT",VERTEX,{"derivedFrom":[subQ1,subQ0]});Q255=makeQuery(id+"F2.imprint","IMPRINT",FACE,{"disambiguationData":[TD([[makeQuery(id+"F2.imprint","IMPRINT",EDGE,{"disambiguationData":[TD([[subQ2,-1.0]])],"derivedFrom":subQ1}),1.0]])]});}
            var Q256;
            {var subQ0=sQuery(id+"F2.wireOp",EDGE,"E95.MirrorCS");var subQ1=sQuery(id+"F2.wireOp",EDGE,"E36.MirrorCS");var subQ2=makeQuery(id+"F2.imprint","INTERSECT",VERTEX,{"derivedFrom":[subQ1,subQ0]});Q256=makeQuery(id+"F2.imprint","IMPRINT",FACE,{"disambiguationData":[TD([[makeQuery(id+"F2.imprint","IMPRINT",EDGE,{"disambiguationData":[TD([[subQ2,-1.0]])],"derivedFrom":subQ1}),-1.0]])]});}
            var Q257;
            {var subQ0=sQuery(id+"F2.wireOp",EDGE,"E82.MirrorCS");var subQ1=sQuery(id+"F2.wireOp",EDGE,"E33.MirrorCS");var subQ2=makeQuery(id+"F2.imprint","INTERSECT",VERTEX,{"derivedFrom":[subQ1,subQ0]});Q257=makeQuery(id+"F2.imprint","IMPRINT",FACE,{"disambiguationData":[TD([[makeQuery(id+"F2.imprint","IMPRINT",EDGE,{"disambiguationData":[TD([[subQ2,-1.0]])],"derivedFrom":subQ1}),-1.0]])]});}
            var Q258;
            {var subQ0=sQuery(id+"F2.wireOp",EDGE,"E96.MirrorCS");var subQ1=sQuery(id+"F2.wireOp",EDGE,"E42.MirrorCS");var subQ2=makeQuery(id+"F2.imprint","INTERSECT",VERTEX,{"derivedFrom":[subQ1,subQ0]});Q258=makeQuery(id+"F2.imprint","IMPRINT",FACE,{"disambiguationData":[TD([[makeQuery(id+"F2.imprint","IMPRINT",EDGE,{"disambiguationData":[TD([[subQ2,-1.0]])],"derivedFrom":subQ1}),1.0]])]});}
            var Q259;
            {var subQ0=sQuery(id+"F2.wireOp",EDGE,"E83.MirrorCS");var subQ1=sQuery(id+"F2.wireOp",EDGE,"E36.MirrorCS");var subQ2=makeQuery(id+"F2.imprint","INTERSECT",VERTEX,{"derivedFrom":[subQ1,subQ0]});Q259=makeQuery(id+"F2.imprint","IMPRINT",FACE,{"disambiguationData":[TD([[makeQuery(id+"F2.imprint","IMPRINT",EDGE,{"disambiguationData":[TD([[subQ2,-1.0]])],"derivedFrom":subQ1}),1.0]])]});}
            var Q260;
            {var subQ0=sQuery(id+"F2.wireOp",EDGE,"E83.MirrorCS");var subQ1=sQuery(id+"F2.wireOp",EDGE,"E36.MirrorCS");var subQ2=makeQuery(id+"F2.imprint","INTERSECT",VERTEX,{"derivedFrom":[subQ1,subQ0]});Q260=makeQuery(id+"F2.imprint","IMPRINT",FACE,{"disambiguationData":[TD([[makeQuery(id+"F2.imprint","IMPRINT",EDGE,{"disambiguationData":[TD([[subQ2,-1.0]])],"derivedFrom":subQ1}),-1.0]])]});}
            var Q261;
            {var subQ0=sQuery(id+"F2.wireOp",EDGE,"E69.MirrorCS");var subQ1=sQuery(id+"F2.wireOp",EDGE,"E33.MirrorCS");var subQ2=makeQuery(id+"F2.imprint","INTERSECT",VERTEX,{"derivedFrom":[subQ1,subQ0]});Q261=makeQuery(id+"F2.imprint","IMPRINT",FACE,{"disambiguationData":[TD([[makeQuery(id+"F2.imprint","IMPRINT",EDGE,{"disambiguationData":[TD([[subQ2,-1.0]])],"derivedFrom":subQ1}),-1.0]])]});}
            var Q262;
            {var subQ0=sQuery(id+"F2.wireOp",EDGE,"E70.MirrorCS");var subQ1=sQuery(id+"F2.wireOp",EDGE,"E36.MirrorCS");var subQ2=makeQuery(id+"F2.imprint","INTERSECT",VERTEX,{"derivedFrom":[subQ1,subQ0]});Q262=makeQuery(id+"F2.imprint","IMPRINT",FACE,{"disambiguationData":[TD([[makeQuery(id+"F2.imprint","IMPRINT",EDGE,{"disambiguationData":[TD([[subQ2,-1.0]])],"derivedFrom":subQ1}),-1.0]])]});}
            var Q263;
            {var subQ0=sQuery(id+"F2.wireOp",EDGE,"E101.MirrorCS");var subQ1=sQuery(id+"F2.wireOp",EDGE,"E41.MirrorCS");var subQ2=makeQuery(id+"F2.imprint","INTERSECT",VERTEX,{"derivedFrom":[subQ1,subQ0]});Q263=makeQuery(id+"F2.imprint","IMPRINT",FACE,{"disambiguationData":[TD([[makeQuery(id+"F2.imprint","IMPRINT",EDGE,{"disambiguationData":[TD([[subQ2,-1.0]])],"derivedFrom":subQ1}),1.0]])]});}
            var Q264;
            {var subQ0=sQuery(id+"F2.wireOp",EDGE,"E100.MirrorCS");var subQ1=sQuery(id+"F2.wireOp",EDGE,"E43.MirrorCS");var subQ2=makeQuery(id+"F2.imprint","INTERSECT",VERTEX,{"derivedFrom":[subQ1,subQ0]});Q264=makeQuery(id+"F2.imprint","IMPRINT",FACE,{"disambiguationData":[TD([[makeQuery(id+"F2.imprint","IMPRINT",EDGE,{"disambiguationData":[TD([[subQ2,-1.0]])],"derivedFrom":subQ1}),1.0]])]});}
            var Q265;
            {var subQ0=sQuery(id+"F2.wireOp",EDGE,"E95.MirrorCS");var subQ1=sQuery(id+"F2.wireOp",EDGE,"E43.MirrorCS");var subQ2=makeQuery(id+"F2.imprint","INTERSECT",VERTEX,{"derivedFrom":[subQ1,subQ0]});Q265=makeQuery(id+"F2.imprint","IMPRINT",FACE,{"disambiguationData":[TD([[makeQuery(id+"F2.imprint","IMPRINT",EDGE,{"disambiguationData":[TD([[subQ2,-1.0]])],"derivedFrom":subQ1}),1.0]])]});}
            extrude(context, id + "F3", {"entities" : qUnion([Q0, Q1, Q2, Q3, Q4, Q5, Q6, Q7, Q8, Q9, Q10, Q11, Q12, Q13, Q14, Q15, Q16, Q17, Q18, Q19, Q20, Q21, Q22, Q23, Q24, Q25, Q26, Q27, Q28, Q29, Q30, Q31, Q32, Q33, Q34, Q35, Q36, Q37, Q38, Q39, Q40, Q41, Q42, Q43, Q44, Q45, Q46, Q47, Q48, Q49, Q50, Q51, Q52, Q53, Q54, Q55, Q56, Q57, Q58, Q59, Q60, Q61, Q62, Q63, Q64, Q65, Q66, Q67, Q68, Q69, Q70, Q71, Q72, Q73, Q74, Q75, Q76, Q77, Q78, Q79, Q80, Q81, Q82, Q83, Q84, Q85, Q86, Q87, Q88, Q89, Q90, Q91, Q92, Q93, Q94, Q95, Q96, Q97, Q98, Q99, Q100, Q101, Q102, Q103, Q104, Q105, Q106, Q107, Q108, Q109, Q110, Q111, Q112, Q113, Q114, Q115, Q116, Q117, Q118, Q119, Q120, Q121, Q122, Q123, Q124, Q125, Q126, Q127, Q128, Q129, Q130, Q131, Q132, Q133, Q134, Q135, Q136, Q137, Q138, Q139, Q140, Q141, Q142, Q143, Q144, Q145, Q146, Q147, Q148, Q149, Q150, Q151, Q152, Q153, Q154, Q155, Q156, Q157, Q158, Q159, Q160, Q161, Q162, Q163, Q164, Q165, Q166, Q167, Q168, Q169, Q170, Q171, Q172, Q173, Q174, Q175, Q176, Q177, Q178, Q179, Q180, Q181, Q182, Q183, Q184, Q185, Q186, Q187, Q188, Q189, Q190, Q191, Q192, Q193, Q194, Q195, Q196, Q197, Q198, Q199, Q200, Q201, Q202, Q203, Q204, Q205, Q206, Q207, Q208, Q209, Q210, Q211, Q212, Q213, Q214, Q215, Q216, Q217, Q218, Q219, Q220, Q221, Q222, Q223, Q224, Q225, Q226, Q227, Q228, Q229, Q230, Q231, Q232, Q233, Q234, Q235, Q236, Q237, Q238, Q239, Q240, Q241, Q242, Q243, Q244, Q245, Q246, Q247, Q248, Q249, Q250, Q251, Q252, Q253, Q254, Q255, Q256, Q257, Q258, Q259, Q260, Q261, Q262, Q263, Q264, Q265]), "operationType" : NewBodyOperationType.REMOVE, "oppositeDirection" : true, "depth" : 25 * mm, "symmetric" : true});
        }
        {
            var Q0;
            Q0=makeQuery(id+"F1.opExtrude","CAP_FACE",FACE,{"disambiguationData":[OSD([sQuery(id+"F0.wireOp",EDGE,"E0"),sQuery(id+"F0.wireOp",EDGE,"E1"),sQuery(id+"F0.wireOp",EDGE,"E3.trimOffspring"),sQuery(id+"F0.wireOp",EDGE,"E4.MirrorCS"),sQuery(id+"F0.wireOp",EDGE,"E5.MirrorCS"),sQuery(id+"F0.wireOp",EDGE,"E6.MirrorCS"),sQuery(id+"F0.wireOp",EDGE,"E7.MirrorCS"),sQuery(id+"F0.wireOp",EDGE,"E8.trimOffspring"),sQuery(id+"F0.wireOp",EDGE,"E9.trimOffspring"),sQuery(id+"F0.wireOp",EDGE,"E10"),sQuery(id+"F0.wireOp",EDGE,"E13"),sQuery(id+"F0.wireOp",EDGE,"E14.0"),sQuery(id+"F0.wireOp",EDGE,"E14.2"),sQuery(id+"F0.wireOp",EDGE,"E15.1.1"),sQuery(id+"F0.wireOp",EDGE,"E15.1.2"),sQuery(id+"F0.wireOp",EDGE,"E15.2.1"),sQuery(id+"F0.wireOp",EDGE,"E15.2.2"),sQuery(id+"F0.wireOp",EDGE,"E15.3.1"),sQuery(id+"F0.wireOp",EDGE,"E15.3.2"),sQuery(id+"F0.wireOp",EDGE,"E15.4.1"),sQuery(id+"F0.wireOp",EDGE,"E15.4.2"),sQuery(id+"F0.wireOp",EDGE,"E15.5.1"),sQuery(id+"F0.wireOp",EDGE,"E15.5.2"),sQuery(id+"F0.wireOp",EDGE,"E15.6.1"),sQuery(id+"F0.wireOp",EDGE,"E15.6.2"),sQuery(id+"F0.wireOp",EDGE,"E15.7.1"),sQuery(id+"F0.wireOp",EDGE,"E15.7.2"),sQuery(id+"F0.wireOp",EDGE,"E15.8.1"),sQuery(id+"F0.wireOp",EDGE,"E15.8.2"),sQuery(id+"F0.wireOp",EDGE,"E15.10.1"),sQuery(id+"F0.wireOp",EDGE,"E15.10.2"),sQuery(id+"F0.wireOp",EDGE,"E15.11.1"),sQuery(id+"F0.wireOp",EDGE,"E15.11.2"),sQuery(id+"F0.wireOp",EDGE,"E16.trimOffspring"),sQuery(id+"F0.wireOp",EDGE,"E17.trimOffspring"),sQuery(id+"F0.wireOp",EDGE,"E18.trimOffspring"),sQuery(id+"F0.wireOp",EDGE,"E19.trimOffspring"),sQuery(id+"F0.wireOp",EDGE,"E20.trimOffspring"),sQuery(id+"F0.wireOp",EDGE,"E21.trimOffspring"),sQuery(id+"F0.wireOp",EDGE,"E22.trimOffspring"),sQuery(id+"F0.wireOp",EDGE,"E23.trimOffspring"),sQuery(id+"F0.wireOp",EDGE,"E24.trimOffspring"),sQuery(id+"F0.wireOp",EDGE,"E25.trimOffspring"),sQuery(id+"F0.wireOp",EDGE,"E26.trimOffspring"),sQuery(id+"F0.wireOp",EDGE,"E28"),sQuery(id+"F0.wireOp",EDGE,"E29")])],"isStart":false});
            var Q1;
            Q1=makeQuery(id+"F1.opExtrude","CAP_FACE",FACE,{"disambiguationData":[OSD([sQuery(id+"F0.wireOp",EDGE,"E0"),sQuery(id+"F0.wireOp",EDGE,"E1"),sQuery(id+"F0.wireOp",EDGE,"E3.trimOffspring"),sQuery(id+"F0.wireOp",EDGE,"E4.MirrorCS"),sQuery(id+"F0.wireOp",EDGE,"E5.MirrorCS"),sQuery(id+"F0.wireOp",EDGE,"E6.MirrorCS"),sQuery(id+"F0.wireOp",EDGE,"E7.MirrorCS"),sQuery(id+"F0.wireOp",EDGE,"E8.trimOffspring"),sQuery(id+"F0.wireOp",EDGE,"E9.trimOffspring"),sQuery(id+"F0.wireOp",EDGE,"E10"),sQuery(id+"F0.wireOp",EDGE,"E13"),sQuery(id+"F0.wireOp",EDGE,"E14.0"),sQuery(id+"F0.wireOp",EDGE,"E14.2"),sQuery(id+"F0.wireOp",EDGE,"E15.1.1"),sQuery(id+"F0.wireOp",EDGE,"E15.1.2"),sQuery(id+"F0.wireOp",EDGE,"E15.2.1"),sQuery(id+"F0.wireOp",EDGE,"E15.2.2"),sQuery(id+"F0.wireOp",EDGE,"E15.3.1"),sQuery(id+"F0.wireOp",EDGE,"E15.3.2"),sQuery(id+"F0.wireOp",EDGE,"E15.4.1"),sQuery(id+"F0.wireOp",EDGE,"E15.4.2"),sQuery(id+"F0.wireOp",EDGE,"E15.5.1"),sQuery(id+"F0.wireOp",EDGE,"E15.5.2"),sQuery(id+"F0.wireOp",EDGE,"E15.6.1"),sQuery(id+"F0.wireOp",EDGE,"E15.6.2"),sQuery(id+"F0.wireOp",EDGE,"E15.7.1"),sQuery(id+"F0.wireOp",EDGE,"E15.7.2"),sQuery(id+"F0.wireOp",EDGE,"E15.8.1"),sQuery(id+"F0.wireOp",EDGE,"E15.8.2"),sQuery(id+"F0.wireOp",EDGE,"E15.10.1"),sQuery(id+"F0.wireOp",EDGE,"E15.10.2"),sQuery(id+"F0.wireOp",EDGE,"E15.11.1"),sQuery(id+"F0.wireOp",EDGE,"E15.11.2"),sQuery(id+"F0.wireOp",EDGE,"E16.trimOffspring"),sQuery(id+"F0.wireOp",EDGE,"E17.trimOffspring"),sQuery(id+"F0.wireOp",EDGE,"E18.trimOffspring"),sQuery(id+"F0.wireOp",EDGE,"E19.trimOffspring"),sQuery(id+"F0.wireOp",EDGE,"E20.trimOffspring"),sQuery(id+"F0.wireOp",EDGE,"E21.trimOffspring"),sQuery(id+"F0.wireOp",EDGE,"E22.trimOffspring"),sQuery(id+"F0.wireOp",EDGE,"E23.trimOffspring"),sQuery(id+"F0.wireOp",EDGE,"E24.trimOffspring"),sQuery(id+"F0.wireOp",EDGE,"E25.trimOffspring"),sQuery(id+"F0.wireOp",EDGE,"E26.trimOffspring"),sQuery(id+"F0.wireOp",EDGE,"E28"),sQuery(id+"F0.wireOp",EDGE,"E29")])],"isStart":true});
            fillet(context, id + "F4", {"entities" : qUnion([Q0, Q1]), "radius" : 1 * mm, "tangentPropagation" : true, "allowEdgeOverflow" : false});
        }
    });
